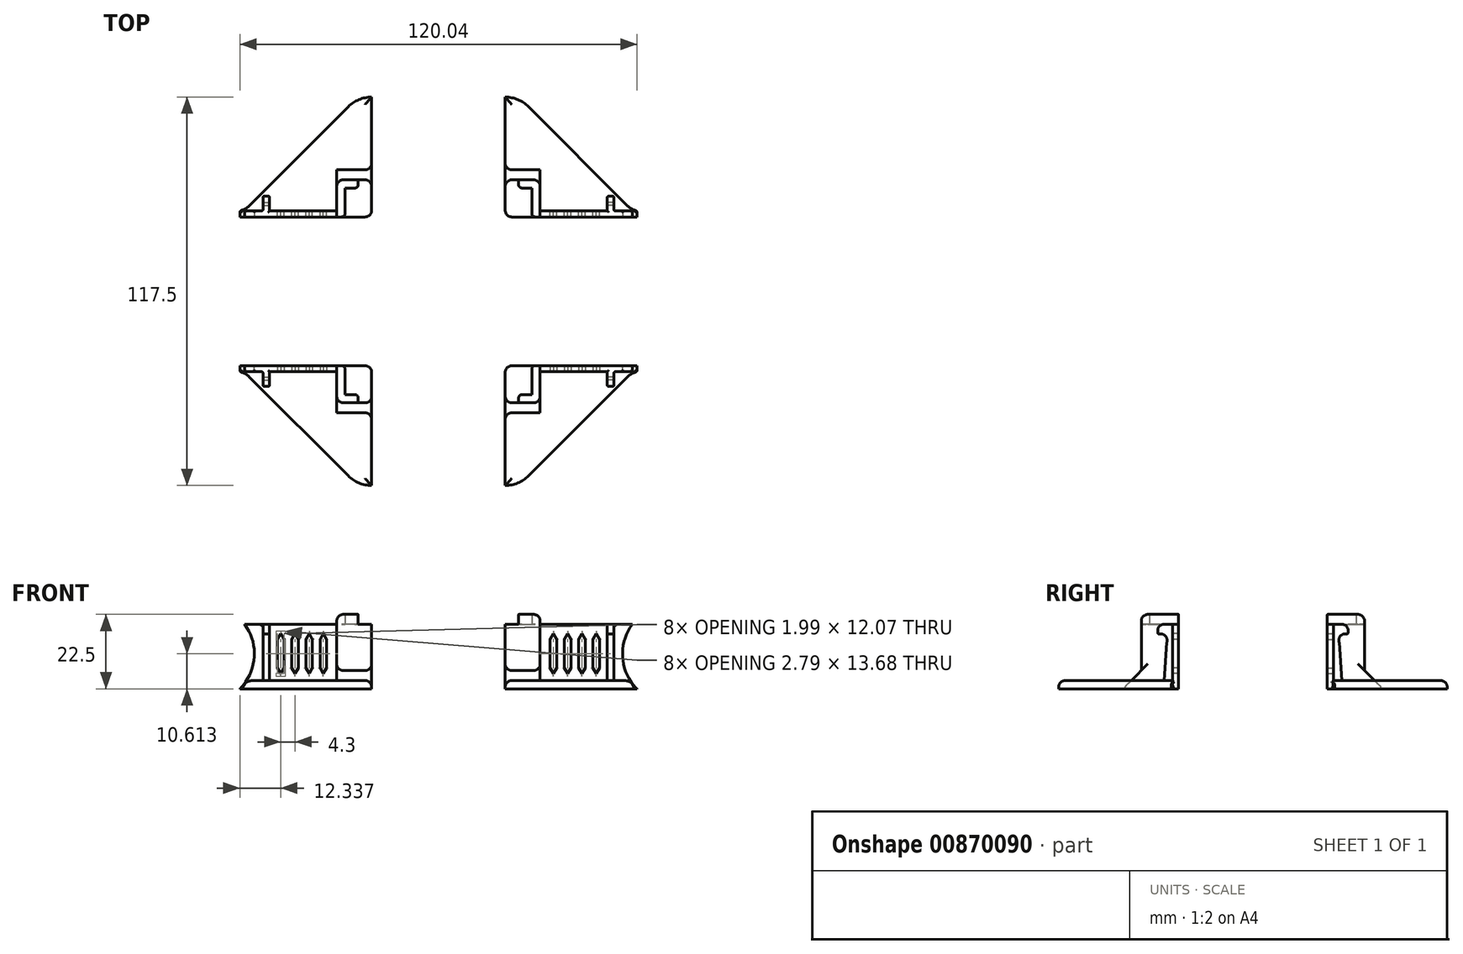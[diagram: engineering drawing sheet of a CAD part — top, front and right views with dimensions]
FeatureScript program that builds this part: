
annotation { "Feature Type Name" : "Feature", "Feature Type Description" : "" }
export const myFeature = defineFeature(function(context is Context, id is Id, definition is map)
    precondition{}
    {
        {
            var Q0;
            Q0=qCreatedBy(makeId("Top.planeOp"),FACE);
            var sketch = newSketch(context, id + "F0", { "sketchPlane" : qUnion([Q0])});
            skCircle(sketch, "E0.cCircle", {"center": v(0, 0) * mm, "radius": 58.75 * mm, "construction": true});
            skLineSegment(sketch, "E0.0", {"start": v(58.75, 24.34) * mm, "end": v(58.75, -24.34) * mm});
            skLineSegment(sketch, "E0.1", {"start": v(57.29, -25.8) * mm, "end": v(27.26, -55.82) * mm});
            skLineSegment(sketch, "E0.2", {"start": v(20.2, -58.75) * mm, "end": v(-20.2, -58.75) * mm});
            skLineSegment(sketch, "E0.3", {"start": v(-27.26, -55.82) * mm, "end": v(-57.29, -25.8) * mm});
            skLineSegment(sketch, "E0.4", {"start": v(-58.75, -24.34) * mm, "end": v(-58.75, 24.34) * mm});
            skLineSegment(sketch, "E0.5", {"start": v(-57.29, 25.8) * mm, "end": v(-27.26, 55.82) * mm});
            skLineSegment(sketch, "E0.6", {"start": v(-20.2, 58.75) * mm, "end": v(20.2, 58.75) * mm});
            skLineSegment(sketch, "E0.7", {"start": v(27.26, 55.82) * mm, "end": v(57.29, 25.8) * mm});
            skPoint(sketch, "E0.0.midPoint", {"position": v(58.75, 0) * mm});
            skLineSegment(sketch, "E1.bottom", {"start": v(60.82, 24.34) * mm, "end": v(85.75, 24.34) * mm});
            skLineSegment(sketch, "E1.top", {"start": v(60.82, -24.34) * mm, "end": v(85.75, -24.34) * mm});
            skLineSegment(sketch, "E1.right", {"start": v(90.75, 19.34) * mm, "end": v(90.75, -19.34) * mm});
            skLineSegment(sketch, "E2.bottom", {"start": v(-60.82, 24.34) * mm, "end": v(-85.75, 24.34) * mm});
            skLineSegment(sketch, "E2.top", {"start": v(-60.82, -24.34) * mm, "end": v(-85.75, -24.34) * mm});
            skLineSegment(sketch, "E2.left", {"start": v(-58.75, 24.34) * mm, "end": v(-58.75, -24.34) * mm});
            skLineSegment(sketch, "E2.right", {"start": v(-90.75, 19.34) * mm, "end": v(-90.75, -19.34) * mm});
            skPoint(sketch, "E3.visualSharp", {"position": v(-58.75, 24.34) * mm});
            skArc(sketch, "E3.filletArc", {"start": v(-60.82, 24.34) * mm, "mid": v(-58.9, 24.72) * mm, "end": v(-57.29, 25.8) * mm});
            skPoint(sketch, "E4.visualSharp", {"position": v(58.75, 24.34) * mm});
            skArc(sketch, "E4.filletArc", {"start": v(57.29, 25.8) * mm, "mid": v(58.9, 24.72) * mm, "end": v(60.82, 24.34) * mm});
            skPoint(sketch, "E5.visualSharp", {"position": v(24.34, 58.75) * mm});
            skArc(sketch, "E5.filletArc", {"start": v(27.26, 55.82) * mm, "mid": v(24.02, 57.99) * mm, "end": v(20.2, 58.75) * mm});
            skPoint(sketch, "E6.visualSharp", {"position": v(-24.34, 58.75) * mm});
            skArc(sketch, "E6.filletArc", {"start": v(-20.2, 58.75) * mm, "mid": v(-24.02, 57.99) * mm, "end": v(-27.26, 55.82) * mm});
            skPoint(sketch, "E7.visualSharp", {"position": v(24.34, -58.75) * mm});
            skArc(sketch, "E7.filletArc", {"start": v(20.2, -58.75) * mm, "mid": v(24.02, -57.99) * mm, "end": v(27.26, -55.82) * mm});
            skPoint(sketch, "E8.visualSharp", {"position": v(-24.34, -58.75) * mm});
            skArc(sketch, "E8.filletArc", {"start": v(-27.26, -55.82) * mm, "mid": v(-24.02, -57.99) * mm, "end": v(-20.2, -58.75) * mm});
            skPoint(sketch, "E9.visualSharp", {"position": v(-58.75, -24.34) * mm});
            skArc(sketch, "E9.filletArc", {"start": v(-57.29, -25.8) * mm, "mid": v(-58.9, -24.72) * mm, "end": v(-60.82, -24.34) * mm});
            skPoint(sketch, "E10.visualSharp", {"position": v(58.75, -24.34) * mm});
            skArc(sketch, "E10.filletArc", {"start": v(60.82, -24.34) * mm, "mid": v(58.9, -24.72) * mm, "end": v(57.29, -25.8) * mm});
            skPoint(sketch, "E11.visualSharp", {"position": v(90.75, -24.34) * mm});
            skArc(sketch, "E11.filletArc", {"start": v(85.75, -24.34) * mm, "mid": v(89.29, -22.87) * mm, "end": v(90.75, -19.34) * mm});
            skPoint(sketch, "E12.visualSharp", {"position": v(90.75, 24.34) * mm});
            skArc(sketch, "E12.filletArc", {"start": v(90.75, 19.34) * mm, "mid": v(89.29, 22.87) * mm, "end": v(85.75, 24.34) * mm});
            skPoint(sketch, "E13.visualSharp", {"position": v(-90.75, 24.34) * mm});
            skArc(sketch, "E13.filletArc", {"start": v(-85.75, 24.34) * mm, "mid": v(-89.29, 22.87) * mm, "end": v(-90.75, 19.34) * mm});
            skPoint(sketch, "E14.visualSharp", {"position": v(-90.75, -24.34) * mm});
            skArc(sketch, "E14.filletArc", {"start": v(-90.75, -19.34) * mm, "mid": v(-89.29, -22.87) * mm, "end": v(-85.75, -24.34) * mm});
            skLineSegment(sketch, "E15", {"start": v(-80.5, -24.34) * mm, "end": v(-80.5, -18.09) * mm});
            skLineSegment(sketch, "E16", {"start": v(-58.25, -18.09) * mm, "end": v(-84.25, -18.09) * mm});
            skLineSegment(sketch, "E17", {"start": v(-56.25, -16.09) * mm, "end": v(-56.25, -16.09) * mm});
            skLineSegment(sketch, "E18", {"start": v(-58.25, -14.09) * mm, "end": v(-84.25, -14.09) * mm});
            skLineSegment(sketch, "E19", {"start": v(-86.25, -16.09) * mm, "end": v(-86.25, -16.09) * mm});
            skLineSegment(sketch, "E20", {"start": v(-86.25, -14.09) * mm, "end": v(-90.75, -14.09) * mm});
            skLineSegment(sketch, "E21", {"start": v(-90.75, 0) * mm, "end": v(90.75, 0) * mm});
            skLineSegment(sketch, "E22", {"start": v(0, 58.75) * mm, "end": v(0, -58.75) * mm});
            skPoint(sketch, "E23.visualSharp", {"position": v(-86.25, -14.09) * mm});
            skArc(sketch, "E23.filletArc", {"start": v(-85.7, -14.09) * mm, "mid": v(-86.09, -14.25) * mm, "end": v(-86.25, -14.63) * mm});
            skArc(sketch, "E24.filletArc", {"start": v(-84.25, -14.09) * mm, "mid": v(-85.66, -14.67) * mm, "end": v(-86.25, -16.09) * mm});
            skPoint(sketch, "E25.visualSharp", {"position": v(-86.25, -18.09) * mm});
            skArc(sketch, "E25.filletArc", {"start": v(-86.25, -16.09) * mm, "mid": v(-85.66, -17.5) * mm, "end": v(-84.25, -18.09) * mm});
            skPoint(sketch, "E26.visualSharp", {"position": v(-56.25, -18.09) * mm});
            skArc(sketch, "E26.filletArc", {"start": v(-58.25, -18.09) * mm, "mid": v(-56.84, -17.5) * mm, "end": v(-56.25, -16.09) * mm});
            skPoint(sketch, "E27.visualSharp", {"position": v(-56.25, -14.09) * mm});
            skArc(sketch, "E27.filletArc", {"start": v(-56.25, -16.09) * mm, "mid": v(-56.84, -14.67) * mm, "end": v(-58.25, -14.09) * mm});
            skLineSegment(sketch, "E28.MirrorCS", {"start": v(-58.25, 14.09) * mm, "end": v(-84.25, 14.09) * mm});
            skArc(sketch, "E29.MirrorCS", {"start": v(-56.25, 16.09) * mm, "mid": v(-56.84, 14.67) * mm, "end": v(-58.25, 14.09) * mm});
            skArc(sketch, "E30.MirrorCS", {"start": v(-58.25, 18.09) * mm, "mid": v(-56.84, 17.5) * mm, "end": v(-56.25, 16.09) * mm});
            skLineSegment(sketch, "E31.MirrorCS", {"start": v(-58.25, 18.09) * mm, "end": v(-84.25, 18.09) * mm});
            skArc(sketch, "E32.MirrorCS", {"start": v(-86.25, 16.09) * mm, "mid": v(-85.66, 17.5) * mm, "end": v(-84.25, 18.09) * mm});
            skArc(sketch, "E33.MirrorCS", {"start": v(-84.25, 14.09) * mm, "mid": v(-85.66, 14.67) * mm, "end": v(-86.25, 16.09) * mm});
            skArc(sketch, "E34.MirrorCS", {"start": v(58.25, -18.09) * mm, "mid": v(56.84, -17.5) * mm, "end": v(56.25, -16.09) * mm});
            skArc(sketch, "E35.MirrorCS", {"start": v(56.25, -16.09) * mm, "mid": v(56.84, -14.67) * mm, "end": v(58.25, -14.09) * mm});
            skLineSegment(sketch, "E36.MirrorCS", {"start": v(58.25, -14.09) * mm, "end": v(84.25, -14.09) * mm});
            skArc(sketch, "E37.MirrorCS", {"start": v(84.25, -14.09) * mm, "mid": v(85.66, -14.67) * mm, "end": v(86.25, -16.09) * mm});
            skArc(sketch, "E38.MirrorCS", {"start": v(86.25, -16.09) * mm, "mid": v(85.66, -17.5) * mm, "end": v(84.25, -18.09) * mm});
            skLineSegment(sketch, "E39.MirrorCS", {"start": v(58.25, -18.09) * mm, "end": v(84.25, -18.09) * mm});
            skArc(sketch, "E40.MirrorCS", {"start": v(56.25, 16.09) * mm, "mid": v(56.84, 14.67) * mm, "end": v(58.25, 14.09) * mm});
            skArc(sketch, "E41.MirrorCS", {"start": v(58.25, 18.09) * mm, "mid": v(56.84, 17.5) * mm, "end": v(56.25, 16.09) * mm});
            skLineSegment(sketch, "E42.MirrorCS", {"start": v(58.25, 18.09) * mm, "end": v(84.25, 18.09) * mm});
            skArc(sketch, "E43.MirrorCS", {"start": v(86.25, 16.09) * mm, "mid": v(85.66, 17.5) * mm, "end": v(84.25, 18.09) * mm});
            skArc(sketch, "E44.MirrorCS", {"start": v(84.25, 14.09) * mm, "mid": v(85.66, 14.67) * mm, "end": v(86.25, 16.09) * mm});
            skLineSegment(sketch, "E45.MirrorCS", {"start": v(58.25, 14.09) * mm, "end": v(84.25, 14.09) * mm});
            skLineSegment(sketch, "E46.bottom", {"start": v(-41.75, -16) * mm, "end": v(-49.75, -16) * mm});
            skLineSegment(sketch, "E46.top", {"start": v(-41.75, 16) * mm, "end": v(-49.75, 16) * mm});
            skLineSegment(sketch, "E46.left", {"start": v(-39.75, -14) * mm, "end": v(-39.75, 14) * mm});
            skLineSegment(sketch, "E46.right", {"start": v(-51.75, -14) * mm, "end": v(-51.75, 14) * mm});
            skPoint(sketch, "E46.middle", {"position": v(-45.75, 0) * mm});
            skLineSegment(sketch, "E47", {"start": v(-51.75, 0) * mm, "end": v(-90.75, 0) * mm});
            skPoint(sketch, "E48.visualSharp", {"position": v(-51.75, 16) * mm});
            skArc(sketch, "E48.filletArc", {"start": v(-49.75, 16) * mm, "mid": v(-51.16, 15.41) * mm, "end": v(-51.75, 14) * mm});
            skPoint(sketch, "E49.visualSharp", {"position": v(-39.75, 16) * mm});
            skArc(sketch, "E49.filletArc", {"start": v(-39.75, 14) * mm, "mid": v(-40.34, 15.41) * mm, "end": v(-41.75, 16) * mm});
            skPoint(sketch, "E50.visualSharp", {"position": v(-39.75, -16) * mm});
            skArc(sketch, "E50.filletArc", {"start": v(-41.75, -16) * mm, "mid": v(-40.34, -15.41) * mm, "end": v(-39.75, -14) * mm});
            skPoint(sketch, "E51.visualSharp", {"position": v(-51.75, -16) * mm});
            skArc(sketch, "E51.filletArc", {"start": v(-51.75, -14) * mm, "mid": v(-51.16, -15.41) * mm, "end": v(-49.75, -16) * mm});
            skLineSegment(sketch, "E52.MirrorCS", {"start": v(39.75, -14) * mm, "end": v(39.75, 14) * mm});
            skArc(sketch, "E53.MirrorCS", {"start": v(39.75, 14) * mm, "mid": v(40.34, 15.41) * mm, "end": v(41.75, 16) * mm});
            skLineSegment(sketch, "E54.MirrorCS", {"start": v(41.75, 16) * mm, "end": v(49.75, 16) * mm});
            skArc(sketch, "E55.MirrorCS", {"start": v(49.75, 16) * mm, "mid": v(51.16, 15.41) * mm, "end": v(51.75, 14) * mm});
            skLineSegment(sketch, "E56.MirrorCS", {"start": v(51.75, -14) * mm, "end": v(51.75, 14) * mm});
            skArc(sketch, "E57.MirrorCS", {"start": v(51.75, -14) * mm, "mid": v(51.16, -15.41) * mm, "end": v(49.75, -16) * mm});
            skLineSegment(sketch, "E58.MirrorCS", {"start": v(41.75, -16) * mm, "end": v(49.75, -16) * mm});
            skArc(sketch, "E59.MirrorCS", {"start": v(41.75, -16) * mm, "mid": v(40.34, -15.41) * mm, "end": v(39.75, -14) * mm});
            skCircle(sketch, "E60", {"center": v(0, 0) * mm, "radius": 7.5 * mm});
            skLineSegment(sketch, "E61.bottom", {"start": v(68.5, -22.5) * mm, "end": v(-68.5, -22.5) * mm});
            skLineSegment(sketch, "E61.top", {"start": v(68.5, 22.5) * mm, "end": v(-68.5, 22.5) * mm});
            skLineSegment(sketch, "E61.left", {"start": v(68.5, -22.5) * mm, "end": v(68.5, 22.5) * mm});
            skLineSegment(sketch, "E61.right", {"start": v(-68.5, -22.5) * mm, "end": v(-68.5, 22.5) * mm});
            skLineSegment(sketch, "E62", {"start": v(-20.2, 58.75) * mm, "end": v(-20.2, -58.75) * mm});
            skLineSegment(sketch, "E63", {"start": v(20.2, 58.75) * mm, "end": v(20.2, -58.75) * mm});
            skLineSegment(sketch, "E64", {"start": v(-60.82, 24.34) * mm, "end": v(-20.2, 24.34) * mm});
            skLineSegment(sketch, "E65", {"start": v(-68.5, 22.5) * mm, "end": v(-71, 22.5) * mm});
            skLineSegment(sketch, "E66", {"start": v(-71, 22.5) * mm, "end": v(-71, 0) * mm});
            skLineSegment(sketch, "E67", {"start": v(-71, 22.34) * mm, "end": v(-71, 22.5) * mm});
            skLineSegment(sketch, "E68", {"start": v(-69, 24.34) * mm, "end": v(-60.82, 24.34) * mm});
            skPoint(sketch, "E69.visualSharp", {"position": v(-71, 24.34) * mm});
            skArc(sketch, "E69.filletArc", {"start": v(-69, 24.34) * mm, "mid": v(-70.41, 23.75) * mm, "end": v(-71, 22.34) * mm});
            skLineSegment(sketch, "E70.bottom", {"start": v(28.25, -31.25) * mm, "end": v(-28.25, -31.25) * mm});
            skLineSegment(sketch, "E70.top", {"start": v(28.25, 31.25) * mm, "end": v(-28.25, 31.25) * mm});
            skLineSegment(sketch, "E70.left", {"start": v(28.25, -31.25) * mm, "end": v(28.25, 31.25) * mm});
            skLineSegment(sketch, "E70.right", {"start": v(-28.25, -31.25) * mm, "end": v(-28.25, 31.25) * mm});
            skLineSegment(sketch, "E71", {"start": v(-28.25, 31.25) * mm, "end": v(-30.75, 31.25) * mm});
            skLineSegment(sketch, "E72", {"start": v(-28.25, 31.25) * mm, "end": v(-28.25, 33.75) * mm});
            skLineSegment(sketch, "E73", {"start": v(-30.75, 33.75) * mm, "end": v(-30.75, 24.34) * mm});
            skLineSegment(sketch, "E74", {"start": v(-30.75, 33.75) * mm, "end": v(0, 33.75) * mm});
            skLineSegment(sketch, "E75", {"start": v(-28.25, 34.5) * mm, "end": v(-24.25, 34.5) * mm});
            skLineSegment(sketch, "E76", {"start": v(-24.25, 33.75) * mm, "end": v(-24.25, 31.25) * mm});
            skLineSegment(sketch, "E77", {"start": v(-30.75, 24.34) * mm, "end": v(-30.75, 22.5) * mm});
            skLineSegment(sketch, "E78", {"start": v(-60.82, 24.34) * mm, "end": v(-60.82, 22.5) * mm});
            skSolve(sketch);
        }
        {
            var Q0;
            Q0=qCreatedBy(makeId("Top.planeOp"),FACE);
            var sketch = newSketch(context, id + "F1", { "sketchPlane" : qUnion([Q0])});
            skLineSegment(sketch, "E79.bottom", {"start": v(68.5, 22.5) * mm, "end": v(-68.5, 22.5) * mm});
            skLineSegment(sketch, "E79.top", {"start": v(68.5, -22.5) * mm, "end": v(-68.5, -22.5) * mm});
            skLineSegment(sketch, "E79.left", {"start": v(68.5, 22.5) * mm, "end": v(68.5, -22.5) * mm});
            skLineSegment(sketch, "E79.right", {"start": v(-68.5, 22.5) * mm, "end": v(-68.5, -22.5) * mm});
            skPoint(sketch, "E79.middle", {"position": v(0, 0) * mm});
            skSolve(sketch);
        }
        {
            var Q0;
            Q0=makeQuery(id+"F0.imprint","IMPRINT",FACE,{"disambiguationData":[TD([[makeQuery(id+"F0.imprint","IMPRINT",EDGE,{"derivedFrom":sQuery(id+"F0.wireOp",EDGE,"E0.5")}),-1.0]])]});
            extrude(context, id + "F2", {"entities" : qUnion([Q0]), "depth" : 2.5 * mm, "offsetDistance" : 25 * mm});
        }
        {
            var Q0;
            {var subQ5=sQuery(id+"F0.wireOp",EDGE,"E77");Q0=makeQuery(id+"F0.imprint","IMPRINT",FACE,{"disambiguationData":[TD([[makeQuery(id+"F0.imprint","IMPRINT",EDGE,{"derivedFrom":subQ5}),-1.0]])]});}
            var Q1;
            {var subQ4=sQuery(id+"F0.wireOp",EDGE,"E62");var subQ6=sQuery(id+"F0.wireOp",EDGE,"E64");var subQ8=makeQuery(id+"F0.imprint","INTERSECT",VERTEX,{"derivedFrom":[subQ4,subQ6]});Q1=makeQuery(id+"F0.imprint","IMPRINT",FACE,{"disambiguationData":[TD([[makeQuery(id+"F0.imprint","IMPRINT",EDGE,{"disambiguationData":[TD([[subQ8,1.0]])],"derivedFrom":subQ4}),-1.0]])]});}
            var Q2;
            {var subQ0=sQuery(id+"F0.wireOp",EDGE,"E62");var subQ1=sQuery(id+"F0.wireOp",EDGE,"E61.top");var subQ2=makeQuery(id+"F0.imprint","INTERSECT",VERTEX,{"derivedFrom":[subQ1,subQ0]});Q2=makeQuery(id+"F0.imprint","IMPRINT",FACE,{"disambiguationData":[TD([[makeQuery(id+"F0.imprint","IMPRINT",EDGE,{"disambiguationData":[TD([[subQ2,-1.0]])],"derivedFrom":subQ1}),-1.0]])]});}
            var Q3;
            {var subQ5=sQuery(id+"F0.wireOp",EDGE,"E76");Q3=makeQuery(id+"F0.imprint","IMPRINT",FACE,{"disambiguationData":[TD([[makeQuery(id+"F0.imprint","IMPRINT",EDGE,{"derivedFrom":subQ5}),1.0]])]});}
            var Q4;
            {var subQ5=sQuery(id+"F0.wireOp",EDGE,"E78");Q4=makeQuery(id+"F0.imprint","IMPRINT",FACE,{"disambiguationData":[TD([[makeQuery(id+"F0.imprint","IMPRINT",EDGE,{"derivedFrom":subQ5}),1.0]])]});}
            extrude(context, id + "F3", {"entities" : qUnion([Q0, Q1, Q2, Q3, Q4]), "operationType" : NewBodyOperationType.ADD, "depth" : 19.5 * mm, "offsetDistance" : 25 * mm});
        }
        {
            var Q0;
            {var subQ0=sQuery(id+"F0.wireOp",EDGE,"E72");Q0=makeQuery(id+"F0.imprint","IMPRINT",FACE,{"disambiguationData":[TD([[makeQuery(id+"F0.imprint","IMPRINT",EDGE,{"derivedFrom":subQ0}),-1.0]])]});}
            var Q1;
            {var subQ0=sQuery(id+"F0.wireOp",EDGE,"E71");Q1=makeQuery(id+"F0.imprint","IMPRINT",FACE,{"disambiguationData":[TD([[makeQuery(id+"F0.imprint","IMPRINT",EDGE,{"derivedFrom":subQ0}),-1.0]])]});}
            var Q2;
            {var subQ5=sQuery(id+"F0.wireOp",EDGE,"E71");Q2=makeQuery(id+"F0.imprint","IMPRINT",FACE,{"disambiguationData":[TD([[makeQuery(id+"F0.imprint","IMPRINT",EDGE,{"derivedFrom":subQ5}),1.0]])]});}
            var Q3;
            {var subQ0=sQuery(id+"F0.wireOp",EDGE,"E77");Q3=makeQuery(id+"F0.imprint","IMPRINT",FACE,{"disambiguationData":[TD([[makeQuery(id+"F0.imprint","IMPRINT",EDGE,{"derivedFrom":subQ0}),1.0]])]});}
            extrude(context, id + "F4", {"entities" : qUnion([Q0, Q1, Q2, Q3]), "operationType" : NewBodyOperationType.ADD, "depth" : 22.5 * mm, "offsetDistance" : 25 * mm});
        }
        {
            var Q0;
            Q0=makeQuery(id+"F4.opExtrude","SWEPT_FACE",FACE,{"disambiguationData":[OSD([sQuery(id+"F0.wireOp",EDGE,"E73"),sQuery(id+"F0.wireOp",EDGE,"E77")])]});
            var sketch = newSketch(context, id + "F5", { "sketchPlane" : qUnion([Q0])});
            skLineSegment(sketch, "E80", {"start": v(-24.34, 19.5) * mm, "end": v(-24.34, 0) * mm});
            skLineSegment(sketch, "E81", {"start": v(-24.34, 0) * mm, "end": v(-24.34, 0) * mm});
            skLineSegment(sketch, "E82", {"start": v(-28.78, 16.41) * mm, "end": v(-28.78, 19.5) * mm});
            skLineSegment(sketch, "E83", {"start": v(-28.78, 19.5) * mm, "end": v(-24.34, 19.5) * mm});
            skCircle(sketch, "E84", {"center": v(-27.9, 14.67) * mm, "radius": 1.95 * mm});
            skCircle(sketch, "E85", {"center": v(-26.92, 17.64) * mm, "radius": 1.86 * mm});
            skLineSegment(sketch, "E86", {"start": v(-26.06, 14.04) * mm, "end": v(-27.04, 0) * mm});
            skLineSegment(sketch, "E87", {"start": v(-27.04, 0) * mm, "end": v(-24.34, 0) * mm});
            skSolve(sketch);
        }
        {
            var Q0;
            {var subQ0=sQuery(id+"F5.wireOp",EDGE,"euI4lTT9-Io7a-ZlEk-LRN0-sRpwTMsxyult");var subQ1=sQuery(id+"F5.wireOp",EDGE,"E84");var subQ2=makeQuery(id+"F5.imprint","INTERSECT",VERTEX,{"derivedFrom":[subQ1,subQ0]});Q0=makeQuery(id+"F5.imprint","IMPRINT",FACE,{"disambiguationData":[TD([[makeQuery(id+"F5.imprint","IMPRINT",EDGE,{"disambiguationData":[TD([[subQ2,-1.0]])],"derivedFrom":subQ1}),-1.0]])]});}
            var Q1;
            {var subQ0=sQuery(id+"F5.wireOp",EDGE,"E85");var subQ1=sQuery(id+"F5.wireOp",EDGE,"E84");var subQ2=makeQuery(id+"F5.imprint","INTERSECT",VERTEX,{"disambiguationData":[OD(0.0)],"derivedFrom":[subQ1,subQ0]});Q1=makeQuery(id+"F5.imprint","IMPRINT",FACE,{"disambiguationData":[TD([[makeQuery(id+"F5.imprint","IMPRINT",EDGE,{"disambiguationData":[TD([[subQ2,1.0]])],"derivedFrom":subQ1}),-1.0]])]});}
            var Q2;
            {var subQ0=sQuery(id+"F5.wireOp",EDGE,"E85");var subQ1=sQuery(id+"F5.wireOp",EDGE,"E84");var subQ2=makeQuery(id+"F5.imprint","INTERSECT",VERTEX,{"disambiguationData":[OD(0.0)],"derivedFrom":[subQ1,subQ0]});Q2=makeQuery(id+"F5.imprint","IMPRINT",FACE,{"disambiguationData":[TD([[makeQuery(id+"F5.imprint","IMPRINT",EDGE,{"disambiguationData":[TD([[subQ2,-1.0]])],"derivedFrom":subQ1}),-1.0]])]});}
            var Q3;
            {var subQ3=sQuery(id+"F5.wireOp",EDGE,"E84");var subQ5=sQuery(id+"F5.wireOp",EDGE,"E86");var subQ6=makeQuery(id+"F5.imprint","INTERSECT",VERTEX,{"derivedFrom":[subQ3,subQ5]});Q3=makeQuery(id+"F5.imprint","IMPRINT",FACE,{"disambiguationData":[TD([[makeQuery(id+"F5.imprint","IMPRINT",EDGE,{"disambiguationData":[TD([[subQ6,-1.0]])],"derivedFrom":subQ3}),-1.0]])]});}
            extrude(context, id + "F6", {"entities" : qUnion([Q0, Q1, Q2, Q3]), "operationType" : NewBodyOperationType.ADD, "depth" : 22.3 * mm, "offsetDistance" : 25 * mm, "hasSecondDirection" : true, "secondDirectionOppositeDirection" : false, "secondDirectionDepth" : 20.3 * mm});
        }
        {
            var Q0;
            Q0=makeQuery(id+"F6.opExtrude","CAP_EDGE",EDGE,{"disambiguationData":[OSD([sQuery(id+"F5.wireOp",EDGE,"E85")])],"isStart":false});
            var Q1;
            Q1=makeQuery(id+"F6.opExtrude","CAP_EDGE",EDGE,{"disambiguationData":[OSD([sQuery(id+"F5.wireOp",EDGE,"E80")])],"isStart":false});
            var Q2;
            Q2=makeQuery(id+"F6.opExtrude","CAP_EDGE",EDGE,{"disambiguationData":[OSD([sQuery(id+"F5.wireOp",EDGE,"E86")])],"isStart":false});
            var Q3;
            Q3=makeQuery(id+"F6.opExtrude","CAP_EDGE",EDGE,{"disambiguationData":[OSD([sQuery(id+"F5.wireOp",EDGE,"E84")])],"isStart":false});
            var Q4;
            Q4=makeQuery(id+"F6.opExtrude","CAP_EDGE",EDGE,{"disambiguationData":[OSD([sQuery(id+"F5.wireOp",EDGE,"E84")])],"isStart":true});
            var Q5;
            Q5=makeQuery(id+"F6.opExtrude","CAP_EDGE",EDGE,{"disambiguationData":[OSD([sQuery(id+"F5.wireOp",EDGE,"E86")])],"isStart":true});
            var Q6;
            Q6=makeQuery(id+"F6.opExtrude","SWEPT_EDGE",EDGE,{"disambiguationData":[OSD([sQuery(id+"F0.wireOp",EDGE,"E73"),sQuery(id+"F5.wireOp",EDGE,"E86")])]});
            var Q7;
            Q7=makeQuery(id+"F6.opExtrude","SWEPT_EDGE",EDGE,{"disambiguationData":[OSD([sQuery(id+"F5.wireOp",EDGE,"E84"),sQuery(id+"F5.wireOp",EDGE,"E86")])]});
            var Q8;
            Q8=makeQuery(id+"F6.opExtrude","SWEPT_EDGE",EDGE,{"disambiguationData":[OSD([sQuery(id+"F5.wireOp",EDGE,"E82"),sQuery(id+"F5.wireOp",EDGE,"E84")])]});
            var Q9;
            Q9=makeQuery(id+"F6.opExtrude","CAP_EDGE",EDGE,{"disambiguationData":[OSD([sQuery(id+"F5.wireOp",EDGE,"E83")])],"isStart":true});
            var Q10;
            {var subQ1=sQuery(id+"F0.wireOp",EDGE,"E73");var subQ2=sQuery(id+"F0.wireOp",EDGE,"E77");var subQ3=sQuery(id+"F0.wireOp",EDGE,"E64");Q10=makeQuery(id+"F6.boolean.opBoolean","SPLIT",EDGE,{"disambiguationData":[TD([makeQuery(id+"F4.opExtrude","SWEPT_FACE",FACE,{"disambiguationData":[OSD([subQ1,subQ2])]})])],"derivedFrom":makeQuery(id+"F3.opExtrude","CAP_EDGE",EDGE,{"disambiguationData":[OSD([subQ3])],"isStart":false})});}
            fillet(context, id + "F7", {"entities" : qUnion([Q0, Q1, Q2, Q3, Q4, Q5, Q6, Q7, Q8, Q9, Q10]), "radius" : .4 * mm, "tangentPropagation" : true, "allowEdgeOverflow" : false});
        }
        {
            var Q0;
            {var subQ0=sQuery(id+"F0.wireOp",EDGE,"E74");var subQ2=makeQuery(id+"F2.opExtrude","CAP_EDGE",EDGE,{"disambiguationData":[OSD([subQ0])],"isStart":false});Q0=makeQuery(id+"F4.boolean.opBoolean","MERGE",EDGE,{"derivedFrom":[makeQuery(id+"F3.boolean.opBoolean","SPLIT",EDGE,{"disambiguationData":[topologyDisambiguationEdgeConnected([makeQuery(id+"F2.opExtrude","SWEPT_FACE",FACE,{"disambiguationData":[OSD([subQ0])]})])],"derivedFrom":subQ2}),makeQuery(id+"F3.boolean.opBoolean","SPLIT",EDGE,{"disambiguationData":[topologyDisambiguationEdgeConnected([makeQuery(id+"F3.opExtrude","SWEPT_FACE",FACE,{"disambiguationData":[OSD([subQ0])]})])],"derivedFrom":subQ2})]});}
            var Q1;
            Q1=makeQuery(id+"F2.opExtrude","CAP_EDGE",EDGE,{"disambiguationData":[OSD([sQuery(id+"F0.wireOp",EDGE,"E73")])],"isStart":false});
            var Q2;
            Q2=makeQuery(id+"FH1p5v7uj7fFukZ_1.opPattern","COPY",EDGE,{"derivedFrom":makeQuery(id+"F2.opExtrude","CAP_EDGE",EDGE,{"disambiguationData":[OSD([sQuery(id+"F0.wireOp",EDGE,"E73")])],"isStart":false}),"instanceName":"1"});
            var Q3;
            {var subQ0=sQuery(id+"F0.wireOp",EDGE,"E74");var subQ2=makeQuery(id+"F2.opExtrude","CAP_EDGE",EDGE,{"disambiguationData":[OSD([subQ0])],"isStart":false});Q3=makeQuery(id+"FH1p5v7uj7fFukZ_1.opPattern","COPY",EDGE,{"derivedFrom":makeQuery(id+"F4.boolean.opBoolean","MERGE",EDGE,{"derivedFrom":[makeQuery(id+"F3.boolean.opBoolean","SPLIT",EDGE,{"disambiguationData":[topologyDisambiguationEdgeConnected([makeQuery(id+"F2.opExtrude","SWEPT_FACE",FACE,{"disambiguationData":[OSD([subQ0])]})])],"derivedFrom":subQ2}),makeQuery(id+"F3.boolean.opBoolean","SPLIT",EDGE,{"disambiguationData":[topologyDisambiguationEdgeConnected([makeQuery(id+"F3.opExtrude","SWEPT_FACE",FACE,{"disambiguationData":[OSD([subQ0])]})])],"derivedFrom":subQ2})]}),"instanceName":"1"});}
            chamfer(context, id + "F8", {"entities" : qUnion([Q0, Q1, Q2, Q3]), "width" : 3 * mm, "tangentPropagation" : true});
        }
        {
            var Q0;
            Q0=makeQuery(id+"F4.opExtrude","SWEPT_EDGE",EDGE,{"disambiguationData":[OSD([sQuery(id+"F0.wireOp",EDGE,"E73"),sQuery(id+"F0.wireOp",EDGE,"E74")])]});
            var Q1;
            Q1=makeQuery(id+"F4.opExtrude","CAP_EDGE",EDGE,{"disambiguationData":[OSD([sQuery(id+"F0.wireOp",EDGE,"E73"),sQuery(id+"F0.wireOp",EDGE,"E77")])],"isStart":false});
            var Q2;
            Q2=makeQuery(id+"F4.opExtrude","CAP_EDGE",EDGE,{"disambiguationData":[OSD([sQuery(id+"F0.wireOp",EDGE,"E74")])],"isStart":false});
            var Q3;
            Q3=makeQuery(id+"F3.opExtrude","SWEPT_EDGE",EDGE,{"disambiguationData":[OSD([sQuery(id+"F0.wireOp",EDGE,"E62"),sQuery(id+"F0.wireOp",EDGE,"E74")])]});
            var Q4;
            Q4=makeQuery(id+"F3.opExtrude","SWEPT_EDGE",EDGE,{"disambiguationData":[OSD([sQuery(id+"F0.wireOp",EDGE,"E61.top"),sQuery(id+"F0.wireOp",EDGE,"E62")])]});
            var Q5;
            Q5=makeQuery(id+"F2.opExtrude","CAP_EDGE",EDGE,{"disambiguationData":[OSD([sQuery(id+"F0.wireOp",EDGE,"E62")])],"isStart":false});
            var Q6;
            Q6=makeQuery(id+"F2.opExtrude","CAP_EDGE",EDGE,{"disambiguationData":[OSD([sQuery(id+"F0.wireOp",EDGE,"E0.5")])],"isStart":false});
            fillet(context, id + "F9", {"entities" : qUnion([Q0, Q1, Q2, Q3, Q4, Q5, Q6]), "radius" : 2 * mm, "tangentPropagation" : true, "allowEdgeOverflow" : false});
        }
        {
            var Q0;
            Q0=makeQuery(id+"FH1p5v7uj7fFukZ_1.opPattern","COPY",EDGE,{"derivedFrom":makeQuery(id+"F3.opExtrude","CAP_EDGE",EDGE,{"disambiguationData":[OSD([sQuery(id+"F0.wireOp",EDGE,"E64"),sQuery(id+"F0.wireOp",EDGE,"E68")])],"isStart":false}),"instanceName":"1"});
            var Q1;
            Q1=makeQuery(id+"F3.opExtrude","CAP_EDGE",EDGE,{"disambiguationData":[OSD([sQuery(id+"F0.wireOp",EDGE,"E66")])],"isStart":false});
            var Q2;
            Q2=makeQuery(id+"FH1p5v7uj7fFukZ_1.opPattern","COPY",EDGE,{"derivedFrom":makeQuery(id+"F4.opExtrude","SWEPT_EDGE",EDGE,{"disambiguationData":[OSD([sQuery(id+"F0.wireOp",EDGE,"E61.top"),sQuery(id+"F0.wireOp",EDGE,"E70.right")])]}),"instanceName":"1"});
            var Q3;
            Q3=makeQuery(id+"F4.opExtrude","SWEPT_EDGE",EDGE,{"disambiguationData":[OSD([sQuery(id+"F0.wireOp",EDGE,"E61.top"),sQuery(id+"F0.wireOp",EDGE,"E70.right")])]});
            var Q4;
            Q4=makeQuery(id+"FH1p5v7uj7fFukZ_1.opPattern","COPY",EDGE,{"derivedFrom":makeQuery(id+"F4.opExtrude","SWEPT_EDGE",EDGE,{"disambiguationData":[OSD([sQuery(id+"F0.wireOp",EDGE,"E70.top"),sQuery(id+"F0.wireOp",EDGE,"E76")])]}),"instanceName":"1"});
            var Q5;
            Q5=makeQuery(id+"F4.opExtrude","SWEPT_EDGE",EDGE,{"disambiguationData":[OSD([sQuery(id+"F0.wireOp",EDGE,"E70.top"),sQuery(id+"F0.wireOp",EDGE,"E76")])]});
            fillet(context, id + "F10", {"entities" : qUnion([Q0, Q1, Q2, Q3, Q4, Q5]), "radius" : 1 * mm, "tangentPropagation" : true, "allowEdgeOverflow" : false});
        }
        {
            var Q0;
            {var subQ0=sQuery(id+"F0.wireOp",EDGE,"E61.top");Q0=makeQuery(id+"F4.boolean.opBoolean","MERGE",FACE,{"derivedFrom":[makeQuery(id+"F3.opExtrude","SWEPT_FACE",FACE,{"disambiguationData":[OSD([subQ0]),TDD([makeQuery(id+"F0.imprint","IMPRINT",EDGE,{"disambiguationData":[TD([[makeQuery(id+"F0.imprint","INTERSECT",VERTEX,{"derivedFrom":[subQ0,sQuery(id+"F0.wireOp",EDGE,"E77")]}),-1.0]])],"derivedFrom":subQ0}),makeQuery(id+"F0.imprint","IMPRINT",EDGE,{"disambiguationData":[TD([[makeQuery(id+"F0.imprint","INTERSECT",VERTEX,{"derivedFrom":[subQ0,sQuery(id+"F0.wireOp",EDGE,"E78")]}),1.0]])],"derivedFrom":subQ0})])]}),makeQuery(id+"F3.opExtrude","SWEPT_FACE",FACE,{"disambiguationData":[OSD([subQ0]),TDD([makeQuery(id+"F0.imprint","IMPRINT",EDGE,{"disambiguationData":[TD([[makeQuery(id+"F0.imprint","INTERSECT",VERTEX,{"derivedFrom":[subQ0,sQuery(id+"F0.wireOp",EDGE,"E62")]}),-1.0]])],"derivedFrom":subQ0})])]}),makeQuery(id+"F4.opExtrude","SWEPT_FACE",FACE,{"disambiguationData":[OSD([subQ0])]})]});}
            var sketch = newSketch(context, id + "F11", { "sketchPlane" : qUnion([Q0])});
            skCircle(sketch, "E88", {"center": v(-70.66, 10.57) * mm, "radius": 15 * mm});
            skPoint(sketch, "E88.centerSnap0", {"position": v(-70.66, 10.57) * mm});
            skSolve(sketch);
        }
        {
            var Q0;
            {var subQ1=sQuery(id+"F0.wireOp",EDGE,"E78");var subQ2=sQuery(id+"F0.wireOp",EDGE,"E61.top");var subQ10=makeQuery(id+"F3.opExtrude","SWEPT_EDGE",EDGE,{"disambiguationData":[OSD([subQ2,subQ1])]});Q0=makeQuery(id+"F11.imprint","IMPRINT",FACE,{"disambiguationData":[TD([[makeQuery(id+"F11.imprint","IMPRINT",EDGE,{"derivedFrom":subQ10}),1.0]])]});}
            extrude(context, id + "F12", {"entities" : qUnion([Q0]), "operationType" : NewBodyOperationType.REMOVE, "oppositeDirection" : true, "depth" : 2 * mm, "offsetDistance" : 25 * mm});
        }
        {
            var Q0;
            {var subQ1=sQuery(id+"F0.wireOp",EDGE,"E77");var subQ2=sQuery(id+"F0.wireOp",EDGE,"E64");var subQ4=sQuery(id+"F0.wireOp",EDGE,"E3.filletArc");var subQ5=sQuery(id+"F0.wireOp",EDGE,"E73");var subQ14=makeQuery(id+"F3.opExtrude","SWEPT_FACE",FACE,{"disambiguationData":[OSD([subQ2])]});Q0=qUnion([makeQuery(id+"F6.boolean.opBoolean","SPLIT",FACE,{"disambiguationData":[TD([makeQuery(id+"F4.opExtrude","SWEPT_FACE",FACE,{"disambiguationData":[OSD([subQ5,subQ1])]})])],"derivedFrom":subQ14}),makeQuery(id+"F6.boolean.opBoolean","SPLIT",FACE,{"disambiguationData":[TD([makeQuery(id+"F2.opExtrude","SWEPT_FACE",FACE,{"disambiguationData":[OSD([subQ4])]})])],"derivedFrom":subQ14})]);}
            var sketch = newSketch(context, id + "F13", { "sketchPlane" : qUnion([Q0])});
            skLineSegment(sketch, "E89", {"start": v(35.78, 14.91) * mm, "end": v(35.78, 6.31) * mm});
            skLineSegment(sketch, "E90", {"start": v(33.79, 14.91) * mm, "end": v(33.79, 6.31) * mm});
            skLineSegment(sketch, "E91", {"start": v(35.78, 14.91) * mm, "end": v(33.79, 14.91) * mm});
            skLineSegment(sketch, "E92", {"start": v(35.78, 14.91) * mm, "end": v(34.78, 16.65) * mm});
            skPoint(sketch, "E92.endSnap0", {"position": v(34.78, 14.91) * mm});
            skLineSegment(sketch, "E93", {"start": v(34.78, 16.65) * mm, "end": v(33.79, 14.91) * mm});
            skLineSegment(sketch, "E94", {"start": v(35.78, 6.31) * mm, "end": v(33.79, 6.31) * mm});
            skLineSegment(sketch, "E95", {"start": v(35.78, 6.31) * mm, "end": v(34.78, 6.31) * mm});
            skLineSegment(sketch, "E96", {"start": v(35.78, 6.31) * mm, "end": v(34.78, 4.58) * mm});
            skLineSegment(sketch, "E97", {"start": v(34.78, 4.58) * mm, "end": v(33.79, 6.31) * mm});
            skLineSegment(sketch, "E98.1.0.0", {"start": v(38.09, 14.91) * mm, "end": v(38.09, 6.31) * mm});
            skLineSegment(sketch, "E98.1.0.1", {"start": v(39.08, 4.58) * mm, "end": v(38.09, 6.31) * mm});
            skPoint(sketch, "E98.1.0.2", {"position": v(39.08, 14.91) * mm});
            skLineSegment(sketch, "E98.1.0.3", {"start": v(40.08, 14.91) * mm, "end": v(40.08, 6.31) * mm});
            skLineSegment(sketch, "E98.1.0.4", {"start": v(39.08, 16.65) * mm, "end": v(38.09, 14.91) * mm});
            skLineSegment(sketch, "E98.1.0.5", {"start": v(40.08, 6.31) * mm, "end": v(39.08, 4.58) * mm});
            skLineSegment(sketch, "E98.1.0.6", {"start": v(40.08, 14.91) * mm, "end": v(39.08, 16.65) * mm});
            skLineSegment(sketch, "E98.1.0.7", {"start": v(40.08, 6.31) * mm, "end": v(38.09, 6.31) * mm});
            skLineSegment(sketch, "E98.1.0.8", {"start": v(40.08, 6.31) * mm, "end": v(39.08, 6.31) * mm});
            skLineSegment(sketch, "E98.1.0.9", {"start": v(40.08, 14.91) * mm, "end": v(38.09, 14.91) * mm});
            skLineSegment(sketch, "E98.2.0.0", {"start": v(42.39, 14.91) * mm, "end": v(42.39, 6.31) * mm});
            skLineSegment(sketch, "E98.2.0.1", {"start": v(43.38, 4.58) * mm, "end": v(42.39, 6.31) * mm});
            skPoint(sketch, "E98.2.0.2", {"position": v(43.38, 14.91) * mm});
            skLineSegment(sketch, "E98.2.0.3", {"start": v(44.38, 14.91) * mm, "end": v(44.38, 6.31) * mm});
            skLineSegment(sketch, "E98.2.0.4", {"start": v(43.38, 16.65) * mm, "end": v(42.39, 14.91) * mm});
            skLineSegment(sketch, "E98.2.0.5", {"start": v(44.38, 6.31) * mm, "end": v(43.38, 4.58) * mm});
            skLineSegment(sketch, "E98.2.0.6", {"start": v(44.38, 14.91) * mm, "end": v(43.38, 16.65) * mm});
            skLineSegment(sketch, "E98.2.0.7", {"start": v(44.38, 6.31) * mm, "end": v(42.39, 6.31) * mm});
            skLineSegment(sketch, "E98.2.0.8", {"start": v(44.38, 6.31) * mm, "end": v(43.38, 6.31) * mm});
            skLineSegment(sketch, "E98.2.0.9", {"start": v(44.38, 14.91) * mm, "end": v(42.39, 14.91) * mm});
            skLineSegment(sketch, "E98.3.0.0", {"start": v(46.69, 14.91) * mm, "end": v(46.69, 6.31) * mm});
            skLineSegment(sketch, "E98.3.0.1", {"start": v(47.68, 4.58) * mm, "end": v(46.69, 6.31) * mm});
            skPoint(sketch, "E98.3.0.2", {"position": v(47.68, 14.91) * mm});
            skLineSegment(sketch, "E98.3.0.3", {"start": v(48.68, 14.91) * mm, "end": v(48.68, 6.31) * mm});
            skLineSegment(sketch, "E98.3.0.4", {"start": v(47.68, 16.65) * mm, "end": v(46.69, 14.91) * mm});
            skLineSegment(sketch, "E98.3.0.5", {"start": v(48.68, 6.31) * mm, "end": v(47.68, 4.58) * mm});
            skLineSegment(sketch, "E98.3.0.6", {"start": v(48.68, 14.91) * mm, "end": v(47.68, 16.65) * mm});
            skLineSegment(sketch, "E98.3.0.7", {"start": v(48.68, 6.31) * mm, "end": v(46.69, 6.31) * mm});
            skLineSegment(sketch, "E98.3.0.8", {"start": v(48.68, 6.31) * mm, "end": v(47.68, 6.31) * mm});
            skLineSegment(sketch, "E98.3.0.9", {"start": v(48.68, 14.91) * mm, "end": v(46.69, 14.91) * mm});
            skLineSegment(sketch, "E98.direction1", {"start": v(34.78, 4.58) * mm, "end": v(39.08, 4.58) * mm, "construction": true});
            skSolve(sketch);
        }
        {
            var Q0;
            Q0=makeQuery(id+"F13.imprint","IMPRINT",FACE,{"disambiguationData":[TD([[makeQuery(id+"F13.imprint","IMPRINT",EDGE,{"derivedFrom":sQuery(id+"F13.wireOp",EDGE,"E91")}),-1.0]])]});
            var Q1;
            {var subQ3=sQuery(id+"F13.wireOp",EDGE,"E89");Q1=makeQuery(id+"F13.imprint","IMPRINT",FACE,{"disambiguationData":[TD([[makeQuery(id+"F13.imprint","IMPRINT",EDGE,{"derivedFrom":subQ3}),-1.0]])]});}
            var Q2;
            {var subQ3=sQuery(id+"F13.wireOp",EDGE,"E96");Q2=makeQuery(id+"F13.imprint","IMPRINT",FACE,{"disambiguationData":[TD([[makeQuery(id+"F13.imprint","IMPRINT",EDGE,{"derivedFrom":subQ3}),-1.0]])]});}
            var Q3;
            Q3=makeQuery(id+"F13.imprint","IMPRINT",FACE,{"disambiguationData":[TD([[makeQuery(id+"F13.imprint","IMPRINT",EDGE,{"derivedFrom":sQuery(id+"F13.wireOp",EDGE,"d3e0095a-e30d-40a6-bb55-9c31538d2f1b.1.0.0")}),-1.0]])]});
            var Q4;
            Q4=makeQuery(id+"F13.imprint","IMPRINT",FACE,{"disambiguationData":[TD([[makeQuery(id+"F13.imprint","IMPRINT",EDGE,{"derivedFrom":sQuery(id+"F13.wireOp",EDGE,"d3e0095a-e30d-40a6-bb55-9c31538d2f1b.1.0.0")}),1.0]])]});
            var Q5;
            Q5=makeQuery(id+"F13.imprint","IMPRINT",FACE,{"disambiguationData":[TD([[makeQuery(id+"F13.imprint","IMPRINT",EDGE,{"derivedFrom":sQuery(id+"F13.wireOp",EDGE,"d3e0095a-e30d-40a6-bb55-9c31538d2f1b.1.0.1")}),-1.0]])]});
            var Q6;
            Q6=makeQuery(id+"F13.imprint","IMPRINT",FACE,{"disambiguationData":[TD([[makeQuery(id+"F13.imprint","IMPRINT",EDGE,{"derivedFrom":sQuery(id+"F13.wireOp",EDGE,"d3e0095a-e30d-40a6-bb55-9c31538d2f1b.2.0.1")}),-1.0]])]});
            var Q7;
            Q7=makeQuery(id+"F13.imprint","IMPRINT",FACE,{"disambiguationData":[TD([[makeQuery(id+"F13.imprint","IMPRINT",EDGE,{"derivedFrom":sQuery(id+"F13.wireOp",EDGE,"d3e0095a-e30d-40a6-bb55-9c31538d2f1b.2.0.0")}),1.0]])]});
            var Q8;
            Q8=makeQuery(id+"F13.imprint","IMPRINT",FACE,{"disambiguationData":[TD([[makeQuery(id+"F13.imprint","IMPRINT",EDGE,{"derivedFrom":sQuery(id+"F13.wireOp",EDGE,"d3e0095a-e30d-40a6-bb55-9c31538d2f1b.2.0.0")}),-1.0]])]});
            var Q9;
            Q9=makeQuery(id+"F13.imprint","IMPRINT",FACE,{"disambiguationData":[TD([[makeQuery(id+"F13.imprint","IMPRINT",EDGE,{"derivedFrom":sQuery(id+"F13.wireOp",EDGE,"d3e0095a-e30d-40a6-bb55-9c31538d2f1b.3.0.1")}),-1.0]])]});
            var Q10;
            Q10=makeQuery(id+"F13.imprint","IMPRINT",FACE,{"disambiguationData":[TD([[makeQuery(id+"F13.imprint","IMPRINT",EDGE,{"derivedFrom":sQuery(id+"F13.wireOp",EDGE,"d3e0095a-e30d-40a6-bb55-9c31538d2f1b.3.0.0")}),1.0]])]});
            var Q11;
            Q11=makeQuery(id+"F13.imprint","IMPRINT",FACE,{"disambiguationData":[TD([[makeQuery(id+"F13.imprint","IMPRINT",EDGE,{"derivedFrom":sQuery(id+"F13.wireOp",EDGE,"d3e0095a-e30d-40a6-bb55-9c31538d2f1b.3.0.0")}),-1.0]])]});
            var Q12;
            Q12=makeQuery(id+"F13.imprint","IMPRINT",FACE,{"disambiguationData":[TD([[makeQuery(id+"F13.imprint","IMPRINT",EDGE,{"derivedFrom":sQuery(id+"F13.wireOp",EDGE,"d3e0095a-e30d-40a6-bb55-9c31538d2f1b.4.0.1")}),-1.0]])]});
            var Q13;
            Q13=makeQuery(id+"F13.imprint","IMPRINT",FACE,{"disambiguationData":[TD([[makeQuery(id+"F13.imprint","IMPRINT",EDGE,{"derivedFrom":sQuery(id+"F13.wireOp",EDGE,"d3e0095a-e30d-40a6-bb55-9c31538d2f1b.4.0.0")}),1.0]])]});
            var Q14;
            Q14=makeQuery(id+"F13.imprint","IMPRINT",FACE,{"disambiguationData":[TD([[makeQuery(id+"F13.imprint","IMPRINT",EDGE,{"derivedFrom":sQuery(id+"F13.wireOp",EDGE,"d3e0095a-e30d-40a6-bb55-9c31538d2f1b.4.0.0")}),-1.0]])]});
            var Q15;
            Q15=makeQuery(id+"F13.imprint","IMPRINT",FACE,{"disambiguationData":[TD([[makeQuery(id+"F13.imprint","IMPRINT",EDGE,{"derivedFrom":sQuery(id+"F13.wireOp",EDGE,"54823be7-8fca-406a-8078-c69425b5e832.0.3.0")}),1.0]])]});
            var Q16;
            Q16=makeQuery(id+"F13.imprint","IMPRINT",FACE,{"disambiguationData":[TD([[makeQuery(id+"F13.imprint","IMPRINT",EDGE,{"derivedFrom":sQuery(id+"F13.wireOp",EDGE,"54823be7-8fca-406a-8078-c69425b5e832.0.3.0")}),-1.0]])]});
            var Q17;
            Q17=makeQuery(id+"F13.imprint","IMPRINT",FACE,{"disambiguationData":[TD([[makeQuery(id+"F13.imprint","IMPRINT",EDGE,{"derivedFrom":sQuery(id+"F13.wireOp",EDGE,"54823be7-8fca-406a-8078-c69425b5e832.3.3.0")}),-1.0]])]});
            var Q18;
            {var subQ1=sQuery(id+"F13.wireOp",EDGE,"E98.1.0.0");Q18=makeQuery(id+"F13.imprint","IMPRINT",FACE,{"disambiguationData":[TD([[makeQuery(id+"F13.imprint","IMPRINT",EDGE,{"derivedFrom":subQ1}),1.0]])]});}
            var Q19;
            Q19=makeQuery(id+"F13.imprint","IMPRINT",FACE,{"disambiguationData":[TD([[makeQuery(id+"F13.imprint","IMPRINT",EDGE,{"derivedFrom":sQuery(id+"F13.wireOp",EDGE,"E98.1.0.4")}),1.0]])]});
            var Q20;
            {var subQ0=sQuery(id+"F13.wireOp",EDGE,"E98.1.0.1");Q20=makeQuery(id+"F13.imprint","IMPRINT",FACE,{"disambiguationData":[TD([[makeQuery(id+"F13.imprint","IMPRINT",EDGE,{"derivedFrom":subQ0}),-1.0]])]});}
            var Q21;
            {var subQ0=sQuery(id+"F13.wireOp",EDGE,"E98.2.0.1");Q21=makeQuery(id+"F13.imprint","IMPRINT",FACE,{"disambiguationData":[TD([[makeQuery(id+"F13.imprint","IMPRINT",EDGE,{"derivedFrom":subQ0}),-1.0]])]});}
            var Q22;
            {var subQ1=sQuery(id+"F13.wireOp",EDGE,"E98.2.0.0");Q22=makeQuery(id+"F13.imprint","IMPRINT",FACE,{"disambiguationData":[TD([[makeQuery(id+"F13.imprint","IMPRINT",EDGE,{"derivedFrom":subQ1}),1.0]])]});}
            var Q23;
            Q23=makeQuery(id+"F13.imprint","IMPRINT",FACE,{"disambiguationData":[TD([[makeQuery(id+"F13.imprint","IMPRINT",EDGE,{"derivedFrom":sQuery(id+"F13.wireOp",EDGE,"E98.2.0.4")}),1.0]])]});
            var Q24;
            Q24=makeQuery(id+"F13.imprint","IMPRINT",FACE,{"disambiguationData":[TD([[makeQuery(id+"F13.imprint","IMPRINT",EDGE,{"derivedFrom":sQuery(id+"F13.wireOp",EDGE,"E98.3.0.4")}),1.0]])]});
            var Q25;
            {var subQ1=sQuery(id+"F13.wireOp",EDGE,"E98.3.0.0");Q25=makeQuery(id+"F13.imprint","IMPRINT",FACE,{"disambiguationData":[TD([[makeQuery(id+"F13.imprint","IMPRINT",EDGE,{"derivedFrom":subQ1}),1.0]])]});}
            var Q26;
            {var subQ0=sQuery(id+"F13.wireOp",EDGE,"E98.3.0.1");Q26=makeQuery(id+"F13.imprint","IMPRINT",FACE,{"disambiguationData":[TD([[makeQuery(id+"F13.imprint","IMPRINT",EDGE,{"derivedFrom":subQ0}),-1.0]])]});}
            var Q27;
            Q27=makeQuery(id+"F13.imprint","IMPRINT",FACE,{"disambiguationData":[TD([[makeQuery(id+"F13.imprint","IMPRINT",EDGE,{"derivedFrom":sQuery(id+"F13.wireOp",EDGE,"E98.4.0.1")}),-1.0]])]});
            var Q28;
            Q28=makeQuery(id+"F13.imprint","IMPRINT",FACE,{"disambiguationData":[TD([[makeQuery(id+"F13.imprint","IMPRINT",EDGE,{"derivedFrom":sQuery(id+"F13.wireOp",EDGE,"E98.4.0.0")}),1.0]])]});
            var Q29;
            Q29=makeQuery(id+"F13.imprint","IMPRINT",FACE,{"disambiguationData":[TD([[makeQuery(id+"F13.imprint","IMPRINT",EDGE,{"derivedFrom":sQuery(id+"F13.wireOp",EDGE,"E98.4.0.4")}),1.0]])]});
            extrude(context, id + "F14", {"entities" : qUnion([Q0, Q1, Q2, Q3, Q4, Q5, Q6, Q7, Q8, Q9, Q10, Q11, Q12, Q13, Q14, Q15, Q16, Q17, Q18, Q19, Q20, Q21, Q22, Q23, Q24, Q25, Q26, Q27, Q28, Q29]), "operationType" : NewBodyOperationType.REMOVE, "oppositeDirection" : true, "depth" : 2 * mm, "offsetDistance" : 25 * mm});
        }
        {
            var Q0;
            Q0=makeQuery(id+"F14.boolean.opBoolean","COPY",EDGE,{"derivedFrom":makeQuery(id+"F14.opExtrude","CAP_EDGE",EDGE,{"disambiguationData":[OSD([sQuery(id+"F13.wireOp",EDGE,"E90")])],"isStart":true})});
            var Q1;
            Q1=makeQuery(id+"F14.boolean.opBoolean","COPY",EDGE,{"derivedFrom":makeQuery(id+"F14.opExtrude","CAP_EDGE",EDGE,{"disambiguationData":[OSD([sQuery(id+"F13.wireOp",EDGE,"E93")])],"isStart":true})});
            var Q2;
            Q2=makeQuery(id+"F14.boolean.opBoolean","COPY",EDGE,{"derivedFrom":makeQuery(id+"F14.opExtrude","CAP_EDGE",EDGE,{"disambiguationData":[OSD([sQuery(id+"F13.wireOp",EDGE,"E92")])],"isStart":true})});
            var Q3;
            Q3=makeQuery(id+"F14.boolean.opBoolean","COPY",EDGE,{"derivedFrom":makeQuery(id+"F14.opExtrude","CAP_EDGE",EDGE,{"disambiguationData":[OSD([sQuery(id+"F13.wireOp",EDGE,"E89")])],"isStart":true})});
            var Q4;
            Q4=makeQuery(id+"F14.boolean.opBoolean","COPY",EDGE,{"derivedFrom":makeQuery(id+"F14.opExtrude","CAP_EDGE",EDGE,{"disambiguationData":[OSD([sQuery(id+"F13.wireOp",EDGE,"E96")])],"isStart":true})});
            var Q5;
            Q5=makeQuery(id+"F14.boolean.opBoolean","COPY",EDGE,{"derivedFrom":makeQuery(id+"F14.opExtrude","CAP_EDGE",EDGE,{"disambiguationData":[OSD([sQuery(id+"F13.wireOp",EDGE,"E97")])],"isStart":true})});
            var Q6;
            Q6=makeQuery(id+"F14.boolean.opBoolean","COPY",EDGE,{"derivedFrom":makeQuery(id+"F14.opExtrude","CAP_EDGE",EDGE,{"disambiguationData":[OSD([sQuery(id+"F13.wireOp",EDGE,"d3e0095a-e30d-40a6-bb55-9c31538d2f1b.1.0.3")])],"isStart":true})});
            var Q7;
            Q7=makeQuery(id+"F14.boolean.opBoolean","COPY",EDGE,{"derivedFrom":makeQuery(id+"F14.opExtrude","CAP_EDGE",EDGE,{"disambiguationData":[OSD([sQuery(id+"F13.wireOp",EDGE,"d3e0095a-e30d-40a6-bb55-9c31538d2f1b.1.0.7")])],"isStart":true})});
            var Q8;
            Q8=makeQuery(id+"F14.boolean.opBoolean","COPY",EDGE,{"derivedFrom":makeQuery(id+"F14.opExtrude","CAP_EDGE",EDGE,{"disambiguationData":[OSD([sQuery(id+"F13.wireOp",EDGE,"d3e0095a-e30d-40a6-bb55-9c31538d2f1b.1.0.2")])],"isStart":true})});
            var Q9;
            Q9=makeQuery(id+"F14.boolean.opBoolean","COPY",EDGE,{"derivedFrom":makeQuery(id+"F14.opExtrude","CAP_EDGE",EDGE,{"disambiguationData":[OSD([sQuery(id+"F13.wireOp",EDGE,"d3e0095a-e30d-40a6-bb55-9c31538d2f1b.1.0.4")])],"isStart":true})});
            var Q10;
            Q10=makeQuery(id+"F14.boolean.opBoolean","COPY",EDGE,{"derivedFrom":makeQuery(id+"F14.opExtrude","CAP_EDGE",EDGE,{"disambiguationData":[OSD([sQuery(id+"F13.wireOp",EDGE,"d3e0095a-e30d-40a6-bb55-9c31538d2f1b.1.0.1")])],"isStart":true})});
            var Q11;
            Q11=makeQuery(id+"F14.boolean.opBoolean","COPY",EDGE,{"derivedFrom":makeQuery(id+"F14.opExtrude","CAP_EDGE",EDGE,{"disambiguationData":[OSD([sQuery(id+"F13.wireOp",EDGE,"d3e0095a-e30d-40a6-bb55-9c31538d2f1b.1.0.5")])],"isStart":true})});
            var Q12;
            Q12=makeQuery(id+"F14.boolean.opBoolean","COPY",EDGE,{"derivedFrom":makeQuery(id+"F14.opExtrude","CAP_EDGE",EDGE,{"disambiguationData":[OSD([sQuery(id+"F13.wireOp",EDGE,"d3e0095a-e30d-40a6-bb55-9c31538d2f1b.2.0.5")])],"isStart":true})});
            var Q13;
            Q13=makeQuery(id+"F14.boolean.opBoolean","COPY",EDGE,{"derivedFrom":makeQuery(id+"F14.opExtrude","CAP_EDGE",EDGE,{"disambiguationData":[OSD([sQuery(id+"F13.wireOp",EDGE,"d3e0095a-e30d-40a6-bb55-9c31538d2f1b.2.0.3")])],"isStart":true})});
            var Q14;
            Q14=makeQuery(id+"F14.boolean.opBoolean","COPY",EDGE,{"derivedFrom":makeQuery(id+"F14.opExtrude","CAP_EDGE",EDGE,{"disambiguationData":[OSD([sQuery(id+"F13.wireOp",EDGE,"d3e0095a-e30d-40a6-bb55-9c31538d2f1b.2.0.4")])],"isStart":true})});
            var Q15;
            Q15=makeQuery(id+"F14.boolean.opBoolean","COPY",EDGE,{"derivedFrom":makeQuery(id+"F14.opExtrude","CAP_EDGE",EDGE,{"disambiguationData":[OSD([sQuery(id+"F13.wireOp",EDGE,"d3e0095a-e30d-40a6-bb55-9c31538d2f1b.2.0.2")])],"isStart":true})});
            var Q16;
            Q16=makeQuery(id+"F14.boolean.opBoolean","COPY",EDGE,{"derivedFrom":makeQuery(id+"F14.opExtrude","CAP_EDGE",EDGE,{"disambiguationData":[OSD([sQuery(id+"F13.wireOp",EDGE,"d3e0095a-e30d-40a6-bb55-9c31538d2f1b.2.0.7")])],"isStart":true})});
            var Q17;
            Q17=makeQuery(id+"F14.boolean.opBoolean","COPY",EDGE,{"derivedFrom":makeQuery(id+"F14.opExtrude","CAP_EDGE",EDGE,{"disambiguationData":[OSD([sQuery(id+"F13.wireOp",EDGE,"d3e0095a-e30d-40a6-bb55-9c31538d2f1b.2.0.1")])],"isStart":true})});
            var Q18;
            Q18=makeQuery(id+"F14.boolean.opBoolean","COPY",EDGE,{"derivedFrom":makeQuery(id+"F14.opExtrude","CAP_EDGE",EDGE,{"disambiguationData":[OSD([sQuery(id+"F13.wireOp",EDGE,"d3e0095a-e30d-40a6-bb55-9c31538d2f1b.3.0.5")])],"isStart":true})});
            var Q19;
            Q19=makeQuery(id+"F14.boolean.opBoolean","COPY",EDGE,{"derivedFrom":makeQuery(id+"F14.opExtrude","CAP_EDGE",EDGE,{"disambiguationData":[OSD([sQuery(id+"F13.wireOp",EDGE,"d3e0095a-e30d-40a6-bb55-9c31538d2f1b.3.0.3")])],"isStart":true})});
            var Q20;
            Q20=makeQuery(id+"F14.boolean.opBoolean","COPY",EDGE,{"derivedFrom":makeQuery(id+"F14.opExtrude","CAP_EDGE",EDGE,{"disambiguationData":[OSD([sQuery(id+"F13.wireOp",EDGE,"d3e0095a-e30d-40a6-bb55-9c31538d2f1b.3.0.4")])],"isStart":true})});
            var Q21;
            Q21=makeQuery(id+"F14.boolean.opBoolean","COPY",EDGE,{"derivedFrom":makeQuery(id+"F14.opExtrude","CAP_EDGE",EDGE,{"disambiguationData":[OSD([sQuery(id+"F13.wireOp",EDGE,"d3e0095a-e30d-40a6-bb55-9c31538d2f1b.3.0.2")])],"isStart":true})});
            var Q22;
            Q22=makeQuery(id+"F14.boolean.opBoolean","COPY",EDGE,{"derivedFrom":makeQuery(id+"F14.opExtrude","CAP_EDGE",EDGE,{"disambiguationData":[OSD([sQuery(id+"F13.wireOp",EDGE,"d3e0095a-e30d-40a6-bb55-9c31538d2f1b.3.0.7")])],"isStart":true})});
            var Q23;
            Q23=makeQuery(id+"F14.boolean.opBoolean","COPY",EDGE,{"derivedFrom":makeQuery(id+"F14.opExtrude","CAP_EDGE",EDGE,{"disambiguationData":[OSD([sQuery(id+"F13.wireOp",EDGE,"d3e0095a-e30d-40a6-bb55-9c31538d2f1b.3.0.1")])],"isStart":true})});
            var Q24;
            Q24=makeQuery(id+"F14.boolean.opBoolean","COPY",EDGE,{"derivedFrom":makeQuery(id+"F14.opExtrude","CAP_EDGE",EDGE,{"disambiguationData":[OSD([sQuery(id+"F13.wireOp",EDGE,"d3e0095a-e30d-40a6-bb55-9c31538d2f1b.4.0.5")])],"isStart":true})});
            var Q25;
            Q25=makeQuery(id+"F14.boolean.opBoolean","COPY",EDGE,{"derivedFrom":makeQuery(id+"F14.opExtrude","CAP_EDGE",EDGE,{"disambiguationData":[OSD([sQuery(id+"F13.wireOp",EDGE,"d3e0095a-e30d-40a6-bb55-9c31538d2f1b.4.0.1")])],"isStart":true})});
            var Q26;
            Q26=makeQuery(id+"F14.boolean.opBoolean","COPY",EDGE,{"derivedFrom":makeQuery(id+"F14.opExtrude","CAP_EDGE",EDGE,{"disambiguationData":[OSD([sQuery(id+"F13.wireOp",EDGE,"d3e0095a-e30d-40a6-bb55-9c31538d2f1b.4.0.7")])],"isStart":true})});
            var Q27;
            Q27=makeQuery(id+"F14.boolean.opBoolean","COPY",EDGE,{"derivedFrom":makeQuery(id+"F14.opExtrude","CAP_EDGE",EDGE,{"disambiguationData":[OSD([sQuery(id+"F13.wireOp",EDGE,"d3e0095a-e30d-40a6-bb55-9c31538d2f1b.4.0.3")])],"isStart":true})});
            var Q28;
            Q28=makeQuery(id+"F14.boolean.opBoolean","COPY",EDGE,{"derivedFrom":makeQuery(id+"F14.opExtrude","CAP_EDGE",EDGE,{"disambiguationData":[OSD([sQuery(id+"F13.wireOp",EDGE,"d3e0095a-e30d-40a6-bb55-9c31538d2f1b.4.0.4")])],"isStart":true})});
            var Q29;
            Q29=makeQuery(id+"F14.boolean.opBoolean","COPY",EDGE,{"derivedFrom":makeQuery(id+"F14.opExtrude","CAP_EDGE",EDGE,{"disambiguationData":[OSD([sQuery(id+"F13.wireOp",EDGE,"d3e0095a-e30d-40a6-bb55-9c31538d2f1b.4.0.2")])],"isStart":true})});
            var Q30;
            {var subQ0=sQuery(id+"F0.wireOp",EDGE,"E61.top");Q30=makeQuery(id+"F14.boolean.opBoolean","INTERSECT",EDGE,{"derivedFrom":[makeQuery(id+"F4.boolean.opBoolean","MERGE",FACE,{"derivedFrom":[makeQuery(id+"F3.opExtrude","SWEPT_FACE",FACE,{"disambiguationData":[OSD([subQ0]),TDD([makeQuery(id+"F0.imprint","IMPRINT",EDGE,{"disambiguationData":[TD([[makeQuery(id+"F0.imprint","INTERSECT",VERTEX,{"derivedFrom":[subQ0,sQuery(id+"F0.wireOp",EDGE,"E77")]}),-1.0]])],"derivedFrom":subQ0}),makeQuery(id+"F0.imprint","IMPRINT",EDGE,{"disambiguationData":[TD([[makeQuery(id+"F0.imprint","INTERSECT",VERTEX,{"derivedFrom":[subQ0,sQuery(id+"F0.wireOp",EDGE,"E78")]}),1.0]])],"derivedFrom":subQ0})])]}),makeQuery(id+"F3.opExtrude","SWEPT_FACE",FACE,{"disambiguationData":[OSD([subQ0]),TDD([makeQuery(id+"F0.imprint","IMPRINT",EDGE,{"disambiguationData":[TD([[makeQuery(id+"F0.imprint","INTERSECT",VERTEX,{"derivedFrom":[subQ0,sQuery(id+"F0.wireOp",EDGE,"E62")]}),-1.0]])],"derivedFrom":subQ0})])]}),makeQuery(id+"F4.opExtrude","SWEPT_FACE",FACE,{"disambiguationData":[OSD([subQ0])]})]}),makeQuery(id+"F14.opExtrude","SWEPT_FACE",FACE,{"disambiguationData":[OSD([sQuery(id+"F13.wireOp",EDGE,"E90")])]})]});}
            var Q31;
            {var subQ0=sQuery(id+"F0.wireOp",EDGE,"E61.top");Q31=makeQuery(id+"F14.boolean.opBoolean","INTERSECT",EDGE,{"derivedFrom":[makeQuery(id+"F4.boolean.opBoolean","MERGE",FACE,{"derivedFrom":[makeQuery(id+"F3.opExtrude","SWEPT_FACE",FACE,{"disambiguationData":[OSD([subQ0]),TDD([makeQuery(id+"F0.imprint","IMPRINT",EDGE,{"disambiguationData":[TD([[makeQuery(id+"F0.imprint","INTERSECT",VERTEX,{"derivedFrom":[subQ0,sQuery(id+"F0.wireOp",EDGE,"E77")]}),-1.0]])],"derivedFrom":subQ0}),makeQuery(id+"F0.imprint","IMPRINT",EDGE,{"disambiguationData":[TD([[makeQuery(id+"F0.imprint","INTERSECT",VERTEX,{"derivedFrom":[subQ0,sQuery(id+"F0.wireOp",EDGE,"E78")]}),1.0]])],"derivedFrom":subQ0})])]}),makeQuery(id+"F3.opExtrude","SWEPT_FACE",FACE,{"disambiguationData":[OSD([subQ0]),TDD([makeQuery(id+"F0.imprint","IMPRINT",EDGE,{"disambiguationData":[TD([[makeQuery(id+"F0.imprint","INTERSECT",VERTEX,{"derivedFrom":[subQ0,sQuery(id+"F0.wireOp",EDGE,"E62")]}),-1.0]])],"derivedFrom":subQ0})])]}),makeQuery(id+"F4.opExtrude","SWEPT_FACE",FACE,{"disambiguationData":[OSD([subQ0])]})]}),makeQuery(id+"F14.opExtrude","SWEPT_FACE",FACE,{"disambiguationData":[OSD([sQuery(id+"F13.wireOp",EDGE,"E93")])]})]});}
            var Q32;
            {var subQ0=sQuery(id+"F0.wireOp",EDGE,"E61.top");Q32=makeQuery(id+"F14.boolean.opBoolean","INTERSECT",EDGE,{"derivedFrom":[makeQuery(id+"F4.boolean.opBoolean","MERGE",FACE,{"derivedFrom":[makeQuery(id+"F3.opExtrude","SWEPT_FACE",FACE,{"disambiguationData":[OSD([subQ0]),TDD([makeQuery(id+"F0.imprint","IMPRINT",EDGE,{"disambiguationData":[TD([[makeQuery(id+"F0.imprint","INTERSECT",VERTEX,{"derivedFrom":[subQ0,sQuery(id+"F0.wireOp",EDGE,"E77")]}),-1.0]])],"derivedFrom":subQ0}),makeQuery(id+"F0.imprint","IMPRINT",EDGE,{"disambiguationData":[TD([[makeQuery(id+"F0.imprint","INTERSECT",VERTEX,{"derivedFrom":[subQ0,sQuery(id+"F0.wireOp",EDGE,"E78")]}),1.0]])],"derivedFrom":subQ0})])]}),makeQuery(id+"F3.opExtrude","SWEPT_FACE",FACE,{"disambiguationData":[OSD([subQ0]),TDD([makeQuery(id+"F0.imprint","IMPRINT",EDGE,{"disambiguationData":[TD([[makeQuery(id+"F0.imprint","INTERSECT",VERTEX,{"derivedFrom":[subQ0,sQuery(id+"F0.wireOp",EDGE,"E62")]}),-1.0]])],"derivedFrom":subQ0})])]}),makeQuery(id+"F4.opExtrude","SWEPT_FACE",FACE,{"disambiguationData":[OSD([subQ0])]})]}),makeQuery(id+"F14.opExtrude","SWEPT_FACE",FACE,{"disambiguationData":[OSD([sQuery(id+"F13.wireOp",EDGE,"E92")])]})]});}
            var Q33;
            {var subQ0=sQuery(id+"F0.wireOp",EDGE,"E61.top");Q33=makeQuery(id+"F14.boolean.opBoolean","INTERSECT",EDGE,{"derivedFrom":[makeQuery(id+"F4.boolean.opBoolean","MERGE",FACE,{"derivedFrom":[makeQuery(id+"F3.opExtrude","SWEPT_FACE",FACE,{"disambiguationData":[OSD([subQ0]),TDD([makeQuery(id+"F0.imprint","IMPRINT",EDGE,{"disambiguationData":[TD([[makeQuery(id+"F0.imprint","INTERSECT",VERTEX,{"derivedFrom":[subQ0,sQuery(id+"F0.wireOp",EDGE,"E77")]}),-1.0]])],"derivedFrom":subQ0}),makeQuery(id+"F0.imprint","IMPRINT",EDGE,{"disambiguationData":[TD([[makeQuery(id+"F0.imprint","INTERSECT",VERTEX,{"derivedFrom":[subQ0,sQuery(id+"F0.wireOp",EDGE,"E78")]}),1.0]])],"derivedFrom":subQ0})])]}),makeQuery(id+"F3.opExtrude","SWEPT_FACE",FACE,{"disambiguationData":[OSD([subQ0]),TDD([makeQuery(id+"F0.imprint","IMPRINT",EDGE,{"disambiguationData":[TD([[makeQuery(id+"F0.imprint","INTERSECT",VERTEX,{"derivedFrom":[subQ0,sQuery(id+"F0.wireOp",EDGE,"E62")]}),-1.0]])],"derivedFrom":subQ0})])]}),makeQuery(id+"F4.opExtrude","SWEPT_FACE",FACE,{"disambiguationData":[OSD([subQ0])]})]}),makeQuery(id+"F14.opExtrude","SWEPT_FACE",FACE,{"disambiguationData":[OSD([sQuery(id+"F13.wireOp",EDGE,"E97")])]})]});}
            var Q34;
            {var subQ0=sQuery(id+"F0.wireOp",EDGE,"E61.top");Q34=makeQuery(id+"F14.boolean.opBoolean","INTERSECT",EDGE,{"derivedFrom":[makeQuery(id+"F4.boolean.opBoolean","MERGE",FACE,{"derivedFrom":[makeQuery(id+"F3.opExtrude","SWEPT_FACE",FACE,{"disambiguationData":[OSD([subQ0]),TDD([makeQuery(id+"F0.imprint","IMPRINT",EDGE,{"disambiguationData":[TD([[makeQuery(id+"F0.imprint","INTERSECT",VERTEX,{"derivedFrom":[subQ0,sQuery(id+"F0.wireOp",EDGE,"E77")]}),-1.0]])],"derivedFrom":subQ0}),makeQuery(id+"F0.imprint","IMPRINT",EDGE,{"disambiguationData":[TD([[makeQuery(id+"F0.imprint","INTERSECT",VERTEX,{"derivedFrom":[subQ0,sQuery(id+"F0.wireOp",EDGE,"E78")]}),1.0]])],"derivedFrom":subQ0})])]}),makeQuery(id+"F3.opExtrude","SWEPT_FACE",FACE,{"disambiguationData":[OSD([subQ0]),TDD([makeQuery(id+"F0.imprint","IMPRINT",EDGE,{"disambiguationData":[TD([[makeQuery(id+"F0.imprint","INTERSECT",VERTEX,{"derivedFrom":[subQ0,sQuery(id+"F0.wireOp",EDGE,"E62")]}),-1.0]])],"derivedFrom":subQ0})])]}),makeQuery(id+"F4.opExtrude","SWEPT_FACE",FACE,{"disambiguationData":[OSD([subQ0])]})]}),makeQuery(id+"F14.opExtrude","SWEPT_FACE",FACE,{"disambiguationData":[OSD([sQuery(id+"F13.wireOp",EDGE,"E96")])]})]});}
            var Q35;
            {var subQ0=sQuery(id+"F0.wireOp",EDGE,"E61.top");Q35=makeQuery(id+"F14.boolean.opBoolean","INTERSECT",EDGE,{"derivedFrom":[makeQuery(id+"F4.boolean.opBoolean","MERGE",FACE,{"derivedFrom":[makeQuery(id+"F3.opExtrude","SWEPT_FACE",FACE,{"disambiguationData":[OSD([subQ0]),TDD([makeQuery(id+"F0.imprint","IMPRINT",EDGE,{"disambiguationData":[TD([[makeQuery(id+"F0.imprint","INTERSECT",VERTEX,{"derivedFrom":[subQ0,sQuery(id+"F0.wireOp",EDGE,"E77")]}),-1.0]])],"derivedFrom":subQ0}),makeQuery(id+"F0.imprint","IMPRINT",EDGE,{"disambiguationData":[TD([[makeQuery(id+"F0.imprint","INTERSECT",VERTEX,{"derivedFrom":[subQ0,sQuery(id+"F0.wireOp",EDGE,"E78")]}),1.0]])],"derivedFrom":subQ0})])]}),makeQuery(id+"F3.opExtrude","SWEPT_FACE",FACE,{"disambiguationData":[OSD([subQ0]),TDD([makeQuery(id+"F0.imprint","IMPRINT",EDGE,{"disambiguationData":[TD([[makeQuery(id+"F0.imprint","INTERSECT",VERTEX,{"derivedFrom":[subQ0,sQuery(id+"F0.wireOp",EDGE,"E62")]}),-1.0]])],"derivedFrom":subQ0})])]}),makeQuery(id+"F4.opExtrude","SWEPT_FACE",FACE,{"disambiguationData":[OSD([subQ0])]})]}),makeQuery(id+"F14.opExtrude","SWEPT_FACE",FACE,{"disambiguationData":[OSD([sQuery(id+"F13.wireOp",EDGE,"E89")])]})]});}
            var Q36;
            {var subQ0=sQuery(id+"F0.wireOp",EDGE,"E61.top");var subQ2=makeQuery(id+"F4.boolean.opBoolean","MERGE",FACE,{"derivedFrom":[makeQuery(id+"F3.opExtrude","SWEPT_FACE",FACE,{"disambiguationData":[OSD([subQ0]),TDD([makeQuery(id+"F0.imprint","IMPRINT",EDGE,{"disambiguationData":[TD([[makeQuery(id+"F0.imprint","INTERSECT",VERTEX,{"derivedFrom":[subQ0,sQuery(id+"F0.wireOp",EDGE,"E77")]}),-1.0]])],"derivedFrom":subQ0}),makeQuery(id+"F0.imprint","IMPRINT",EDGE,{"disambiguationData":[TD([[makeQuery(id+"F0.imprint","INTERSECT",VERTEX,{"derivedFrom":[subQ0,sQuery(id+"F0.wireOp",EDGE,"E78")]}),1.0]])],"derivedFrom":subQ0})])]}),makeQuery(id+"F3.opExtrude","SWEPT_FACE",FACE,{"disambiguationData":[OSD([subQ0]),TDD([makeQuery(id+"F0.imprint","IMPRINT",EDGE,{"disambiguationData":[TD([[makeQuery(id+"F0.imprint","INTERSECT",VERTEX,{"derivedFrom":[subQ0,sQuery(id+"F0.wireOp",EDGE,"E62")]}),-1.0]])],"derivedFrom":subQ0})])]}),makeQuery(id+"F4.opExtrude","SWEPT_FACE",FACE,{"disambiguationData":[OSD([subQ0])]})]});Q36=qUnion([makeQuery(id+"F14.boolean.opBoolean","INTERSECT",EDGE,{"derivedFrom":[subQ2,makeQuery(id+"F14.opExtrude","SWEPT_FACE",FACE,{"disambiguationData":[OSD([sQuery(id+"F13.wireOp",EDGE,"E89")])]})]}),makeQuery(id+"F14.boolean.opBoolean","INTERSECT",EDGE,{"derivedFrom":[subQ2,makeQuery(id+"F14.opExtrude","SWEPT_FACE",FACE,{"disambiguationData":[OSD([sQuery(id+"F13.wireOp",EDGE,"E90")])]})]}),makeQuery(id+"F14.boolean.opBoolean","INTERSECT",EDGE,{"derivedFrom":[subQ2,makeQuery(id+"F14.opExtrude","SWEPT_FACE",FACE,{"disambiguationData":[OSD([sQuery(id+"F13.wireOp",EDGE,"E92")])]})]}),makeQuery(id+"F14.boolean.opBoolean","INTERSECT",EDGE,{"derivedFrom":[subQ2,makeQuery(id+"F14.opExtrude","SWEPT_FACE",FACE,{"disambiguationData":[OSD([sQuery(id+"F13.wireOp",EDGE,"E93")])]})]}),makeQuery(id+"F14.boolean.opBoolean","INTERSECT",EDGE,{"derivedFrom":[subQ2,makeQuery(id+"F14.opExtrude","SWEPT_FACE",FACE,{"disambiguationData":[OSD([sQuery(id+"F13.wireOp",EDGE,"E96")])]})]}),makeQuery(id+"F14.boolean.opBoolean","INTERSECT",EDGE,{"derivedFrom":[subQ2,makeQuery(id+"F14.opExtrude","SWEPT_FACE",FACE,{"disambiguationData":[OSD([sQuery(id+"F13.wireOp",EDGE,"E97")])]})]}),makeQuery(id+"F14.boolean.opBoolean","INTERSECT",EDGE,{"derivedFrom":[subQ2,makeQuery(id+"F14.opExtrude","SWEPT_FACE",FACE,{"disambiguationData":[OSD([sQuery(id+"F13.wireOp",EDGE,"E98.1.0.0")])]})]}),makeQuery(id+"F14.boolean.opBoolean","INTERSECT",EDGE,{"derivedFrom":[subQ2,makeQuery(id+"F14.opExtrude","SWEPT_FACE",FACE,{"disambiguationData":[OSD([sQuery(id+"F13.wireOp",EDGE,"E98.1.0.1")])]})]}),makeQuery(id+"F14.boolean.opBoolean","INTERSECT",EDGE,{"derivedFrom":[subQ2,makeQuery(id+"F14.opExtrude","SWEPT_FACE",FACE,{"disambiguationData":[OSD([sQuery(id+"F13.wireOp",EDGE,"E98.1.0.3")])]})]}),makeQuery(id+"F14.boolean.opBoolean","INTERSECT",EDGE,{"derivedFrom":[subQ2,makeQuery(id+"F14.opExtrude","SWEPT_FACE",FACE,{"disambiguationData":[OSD([sQuery(id+"F13.wireOp",EDGE,"E98.1.0.4")])]})]}),makeQuery(id+"F14.boolean.opBoolean","INTERSECT",EDGE,{"derivedFrom":[subQ2,makeQuery(id+"F14.opExtrude","SWEPT_FACE",FACE,{"disambiguationData":[OSD([sQuery(id+"F13.wireOp",EDGE,"E98.1.0.5")])]})]}),makeQuery(id+"F14.boolean.opBoolean","INTERSECT",EDGE,{"derivedFrom":[subQ2,makeQuery(id+"F14.opExtrude","SWEPT_FACE",FACE,{"disambiguationData":[OSD([sQuery(id+"F13.wireOp",EDGE,"E98.1.0.6")])]})]}),makeQuery(id+"F14.boolean.opBoolean","INTERSECT",EDGE,{"derivedFrom":[subQ2,makeQuery(id+"F14.opExtrude","SWEPT_FACE",FACE,{"disambiguationData":[OSD([sQuery(id+"F13.wireOp",EDGE,"E98.2.0.0")])]})]}),makeQuery(id+"F14.boolean.opBoolean","INTERSECT",EDGE,{"derivedFrom":[subQ2,makeQuery(id+"F14.opExtrude","SWEPT_FACE",FACE,{"disambiguationData":[OSD([sQuery(id+"F13.wireOp",EDGE,"E98.2.0.1")])]})]}),makeQuery(id+"F14.boolean.opBoolean","INTERSECT",EDGE,{"derivedFrom":[subQ2,makeQuery(id+"F14.opExtrude","SWEPT_FACE",FACE,{"disambiguationData":[OSD([sQuery(id+"F13.wireOp",EDGE,"E98.2.0.3")])]})]}),makeQuery(id+"F14.boolean.opBoolean","INTERSECT",EDGE,{"derivedFrom":[subQ2,makeQuery(id+"F14.opExtrude","SWEPT_FACE",FACE,{"disambiguationData":[OSD([sQuery(id+"F13.wireOp",EDGE,"E98.2.0.4")])]})]}),makeQuery(id+"F14.boolean.opBoolean","INTERSECT",EDGE,{"derivedFrom":[subQ2,makeQuery(id+"F14.opExtrude","SWEPT_FACE",FACE,{"disambiguationData":[OSD([sQuery(id+"F13.wireOp",EDGE,"E98.2.0.5")])]})]}),makeQuery(id+"F14.boolean.opBoolean","INTERSECT",EDGE,{"derivedFrom":[subQ2,makeQuery(id+"F14.opExtrude","SWEPT_FACE",FACE,{"disambiguationData":[OSD([sQuery(id+"F13.wireOp",EDGE,"E98.2.0.6")])]})]}),makeQuery(id+"F14.boolean.opBoolean","INTERSECT",EDGE,{"derivedFrom":[subQ2,makeQuery(id+"F14.opExtrude","SWEPT_FACE",FACE,{"disambiguationData":[OSD([sQuery(id+"F13.wireOp",EDGE,"E98.3.0.0")])]})]}),makeQuery(id+"F14.boolean.opBoolean","INTERSECT",EDGE,{"derivedFrom":[subQ2,makeQuery(id+"F14.opExtrude","SWEPT_FACE",FACE,{"disambiguationData":[OSD([sQuery(id+"F13.wireOp",EDGE,"E98.3.0.1")])]})]}),makeQuery(id+"F14.boolean.opBoolean","INTERSECT",EDGE,{"derivedFrom":[subQ2,makeQuery(id+"F14.opExtrude","SWEPT_FACE",FACE,{"disambiguationData":[OSD([sQuery(id+"F13.wireOp",EDGE,"E98.3.0.3")])]})]}),makeQuery(id+"F14.boolean.opBoolean","INTERSECT",EDGE,{"derivedFrom":[subQ2,makeQuery(id+"F14.opExtrude","SWEPT_FACE",FACE,{"disambiguationData":[OSD([sQuery(id+"F13.wireOp",EDGE,"E98.3.0.4")])]})]}),makeQuery(id+"F14.boolean.opBoolean","INTERSECT",EDGE,{"derivedFrom":[subQ2,makeQuery(id+"F14.opExtrude","SWEPT_FACE",FACE,{"disambiguationData":[OSD([sQuery(id+"F13.wireOp",EDGE,"E98.3.0.5")])]})]}),makeQuery(id+"F14.boolean.opBoolean","INTERSECT",EDGE,{"derivedFrom":[subQ2,makeQuery(id+"F14.opExtrude","SWEPT_FACE",FACE,{"disambiguationData":[OSD([sQuery(id+"F13.wireOp",EDGE,"E98.3.0.6")])]})]})]);}
            var Q37;
            {var subQ0=sQuery(id+"F0.wireOp",EDGE,"E61.top");var subQ2=makeQuery(id+"F4.boolean.opBoolean","MERGE",FACE,{"derivedFrom":[makeQuery(id+"F3.opExtrude","SWEPT_FACE",FACE,{"disambiguationData":[OSD([subQ0]),TDD([makeQuery(id+"F0.imprint","IMPRINT",EDGE,{"disambiguationData":[TD([[makeQuery(id+"F0.imprint","INTERSECT",VERTEX,{"derivedFrom":[subQ0,sQuery(id+"F0.wireOp",EDGE,"E77")]}),-1.0]])],"derivedFrom":subQ0}),makeQuery(id+"F0.imprint","IMPRINT",EDGE,{"disambiguationData":[TD([[makeQuery(id+"F0.imprint","INTERSECT",VERTEX,{"derivedFrom":[subQ0,sQuery(id+"F0.wireOp",EDGE,"E78")]}),1.0]])],"derivedFrom":subQ0})])]}),makeQuery(id+"F3.opExtrude","SWEPT_FACE",FACE,{"disambiguationData":[OSD([subQ0]),TDD([makeQuery(id+"F0.imprint","IMPRINT",EDGE,{"disambiguationData":[TD([[makeQuery(id+"F0.imprint","INTERSECT",VERTEX,{"derivedFrom":[subQ0,sQuery(id+"F0.wireOp",EDGE,"E62")]}),-1.0]])],"derivedFrom":subQ0})])]}),makeQuery(id+"F4.opExtrude","SWEPT_FACE",FACE,{"disambiguationData":[OSD([subQ0])]})]});Q37=qUnion([makeQuery(id+"F14.boolean.opBoolean","INTERSECT",EDGE,{"derivedFrom":[subQ2,makeQuery(id+"F14.opExtrude","SWEPT_FACE",FACE,{"disambiguationData":[OSD([sQuery(id+"F13.wireOp",EDGE,"E89")])]})]}),makeQuery(id+"F14.boolean.opBoolean","INTERSECT",EDGE,{"derivedFrom":[subQ2,makeQuery(id+"F14.opExtrude","SWEPT_FACE",FACE,{"disambiguationData":[OSD([sQuery(id+"F13.wireOp",EDGE,"E90")])]})]}),makeQuery(id+"F14.boolean.opBoolean","INTERSECT",EDGE,{"derivedFrom":[subQ2,makeQuery(id+"F14.opExtrude","SWEPT_FACE",FACE,{"disambiguationData":[OSD([sQuery(id+"F13.wireOp",EDGE,"E92")])]})]}),makeQuery(id+"F14.boolean.opBoolean","INTERSECT",EDGE,{"derivedFrom":[subQ2,makeQuery(id+"F14.opExtrude","SWEPT_FACE",FACE,{"disambiguationData":[OSD([sQuery(id+"F13.wireOp",EDGE,"E93")])]})]}),makeQuery(id+"F14.boolean.opBoolean","INTERSECT",EDGE,{"derivedFrom":[subQ2,makeQuery(id+"F14.opExtrude","SWEPT_FACE",FACE,{"disambiguationData":[OSD([sQuery(id+"F13.wireOp",EDGE,"E96")])]})]}),makeQuery(id+"F14.boolean.opBoolean","INTERSECT",EDGE,{"derivedFrom":[subQ2,makeQuery(id+"F14.opExtrude","SWEPT_FACE",FACE,{"disambiguationData":[OSD([sQuery(id+"F13.wireOp",EDGE,"E97")])]})]}),makeQuery(id+"F14.boolean.opBoolean","INTERSECT",EDGE,{"derivedFrom":[subQ2,makeQuery(id+"F14.opExtrude","SWEPT_FACE",FACE,{"disambiguationData":[OSD([sQuery(id+"F13.wireOp",EDGE,"E98.1.0.0")])]})]}),makeQuery(id+"F14.boolean.opBoolean","INTERSECT",EDGE,{"derivedFrom":[subQ2,makeQuery(id+"F14.opExtrude","SWEPT_FACE",FACE,{"disambiguationData":[OSD([sQuery(id+"F13.wireOp",EDGE,"E98.1.0.1")])]})]}),makeQuery(id+"F14.boolean.opBoolean","INTERSECT",EDGE,{"derivedFrom":[subQ2,makeQuery(id+"F14.opExtrude","SWEPT_FACE",FACE,{"disambiguationData":[OSD([sQuery(id+"F13.wireOp",EDGE,"E98.1.0.3")])]})]}),makeQuery(id+"F14.boolean.opBoolean","INTERSECT",EDGE,{"derivedFrom":[subQ2,makeQuery(id+"F14.opExtrude","SWEPT_FACE",FACE,{"disambiguationData":[OSD([sQuery(id+"F13.wireOp",EDGE,"E98.1.0.4")])]})]}),makeQuery(id+"F14.boolean.opBoolean","INTERSECT",EDGE,{"derivedFrom":[subQ2,makeQuery(id+"F14.opExtrude","SWEPT_FACE",FACE,{"disambiguationData":[OSD([sQuery(id+"F13.wireOp",EDGE,"E98.1.0.5")])]})]}),makeQuery(id+"F14.boolean.opBoolean","INTERSECT",EDGE,{"derivedFrom":[subQ2,makeQuery(id+"F14.opExtrude","SWEPT_FACE",FACE,{"disambiguationData":[OSD([sQuery(id+"F13.wireOp",EDGE,"E98.1.0.6")])]})]}),makeQuery(id+"F14.boolean.opBoolean","INTERSECT",EDGE,{"derivedFrom":[subQ2,makeQuery(id+"F14.opExtrude","SWEPT_FACE",FACE,{"disambiguationData":[OSD([sQuery(id+"F13.wireOp",EDGE,"E98.2.0.0")])]})]}),makeQuery(id+"F14.boolean.opBoolean","INTERSECT",EDGE,{"derivedFrom":[subQ2,makeQuery(id+"F14.opExtrude","SWEPT_FACE",FACE,{"disambiguationData":[OSD([sQuery(id+"F13.wireOp",EDGE,"E98.2.0.1")])]})]}),makeQuery(id+"F14.boolean.opBoolean","INTERSECT",EDGE,{"derivedFrom":[subQ2,makeQuery(id+"F14.opExtrude","SWEPT_FACE",FACE,{"disambiguationData":[OSD([sQuery(id+"F13.wireOp",EDGE,"E98.2.0.3")])]})]}),makeQuery(id+"F14.boolean.opBoolean","INTERSECT",EDGE,{"derivedFrom":[subQ2,makeQuery(id+"F14.opExtrude","SWEPT_FACE",FACE,{"disambiguationData":[OSD([sQuery(id+"F13.wireOp",EDGE,"E98.2.0.4")])]})]}),makeQuery(id+"F14.boolean.opBoolean","INTERSECT",EDGE,{"derivedFrom":[subQ2,makeQuery(id+"F14.opExtrude","SWEPT_FACE",FACE,{"disambiguationData":[OSD([sQuery(id+"F13.wireOp",EDGE,"E98.2.0.5")])]})]}),makeQuery(id+"F14.boolean.opBoolean","INTERSECT",EDGE,{"derivedFrom":[subQ2,makeQuery(id+"F14.opExtrude","SWEPT_FACE",FACE,{"disambiguationData":[OSD([sQuery(id+"F13.wireOp",EDGE,"E98.2.0.6")])]})]}),makeQuery(id+"F14.boolean.opBoolean","INTERSECT",EDGE,{"derivedFrom":[subQ2,makeQuery(id+"F14.opExtrude","SWEPT_FACE",FACE,{"disambiguationData":[OSD([sQuery(id+"F13.wireOp",EDGE,"E98.3.0.0")])]})]}),makeQuery(id+"F14.boolean.opBoolean","INTERSECT",EDGE,{"derivedFrom":[subQ2,makeQuery(id+"F14.opExtrude","SWEPT_FACE",FACE,{"disambiguationData":[OSD([sQuery(id+"F13.wireOp",EDGE,"E98.3.0.1")])]})]}),makeQuery(id+"F14.boolean.opBoolean","INTERSECT",EDGE,{"derivedFrom":[subQ2,makeQuery(id+"F14.opExtrude","SWEPT_FACE",FACE,{"disambiguationData":[OSD([sQuery(id+"F13.wireOp",EDGE,"E98.3.0.3")])]})]}),makeQuery(id+"F14.boolean.opBoolean","INTERSECT",EDGE,{"derivedFrom":[subQ2,makeQuery(id+"F14.opExtrude","SWEPT_FACE",FACE,{"disambiguationData":[OSD([sQuery(id+"F13.wireOp",EDGE,"E98.3.0.4")])]})]}),makeQuery(id+"F14.boolean.opBoolean","INTERSECT",EDGE,{"derivedFrom":[subQ2,makeQuery(id+"F14.opExtrude","SWEPT_FACE",FACE,{"disambiguationData":[OSD([sQuery(id+"F13.wireOp",EDGE,"E98.3.0.5")])]})]}),makeQuery(id+"F14.boolean.opBoolean","INTERSECT",EDGE,{"derivedFrom":[subQ2,makeQuery(id+"F14.opExtrude","SWEPT_FACE",FACE,{"disambiguationData":[OSD([sQuery(id+"F13.wireOp",EDGE,"E98.3.0.6")])]})]})]);}
            var Q38;
            {var subQ0=sQuery(id+"F0.wireOp",EDGE,"E61.top");var subQ2=makeQuery(id+"F4.boolean.opBoolean","MERGE",FACE,{"derivedFrom":[makeQuery(id+"F3.opExtrude","SWEPT_FACE",FACE,{"disambiguationData":[OSD([subQ0]),TDD([makeQuery(id+"F0.imprint","IMPRINT",EDGE,{"disambiguationData":[TD([[makeQuery(id+"F0.imprint","INTERSECT",VERTEX,{"derivedFrom":[subQ0,sQuery(id+"F0.wireOp",EDGE,"E77")]}),-1.0]])],"derivedFrom":subQ0}),makeQuery(id+"F0.imprint","IMPRINT",EDGE,{"disambiguationData":[TD([[makeQuery(id+"F0.imprint","INTERSECT",VERTEX,{"derivedFrom":[subQ0,sQuery(id+"F0.wireOp",EDGE,"E78")]}),1.0]])],"derivedFrom":subQ0})])]}),makeQuery(id+"F3.opExtrude","SWEPT_FACE",FACE,{"disambiguationData":[OSD([subQ0]),TDD([makeQuery(id+"F0.imprint","IMPRINT",EDGE,{"disambiguationData":[TD([[makeQuery(id+"F0.imprint","INTERSECT",VERTEX,{"derivedFrom":[subQ0,sQuery(id+"F0.wireOp",EDGE,"E62")]}),-1.0]])],"derivedFrom":subQ0})])]}),makeQuery(id+"F4.opExtrude","SWEPT_FACE",FACE,{"disambiguationData":[OSD([subQ0])]})]});Q38=qUnion([makeQuery(id+"F14.boolean.opBoolean","INTERSECT",EDGE,{"derivedFrom":[subQ2,makeQuery(id+"F14.opExtrude","SWEPT_FACE",FACE,{"disambiguationData":[OSD([sQuery(id+"F13.wireOp",EDGE,"E89")])]})]}),makeQuery(id+"F14.boolean.opBoolean","INTERSECT",EDGE,{"derivedFrom":[subQ2,makeQuery(id+"F14.opExtrude","SWEPT_FACE",FACE,{"disambiguationData":[OSD([sQuery(id+"F13.wireOp",EDGE,"E90")])]})]}),makeQuery(id+"F14.boolean.opBoolean","INTERSECT",EDGE,{"derivedFrom":[subQ2,makeQuery(id+"F14.opExtrude","SWEPT_FACE",FACE,{"disambiguationData":[OSD([sQuery(id+"F13.wireOp",EDGE,"E92")])]})]}),makeQuery(id+"F14.boolean.opBoolean","INTERSECT",EDGE,{"derivedFrom":[subQ2,makeQuery(id+"F14.opExtrude","SWEPT_FACE",FACE,{"disambiguationData":[OSD([sQuery(id+"F13.wireOp",EDGE,"E93")])]})]}),makeQuery(id+"F14.boolean.opBoolean","INTERSECT",EDGE,{"derivedFrom":[subQ2,makeQuery(id+"F14.opExtrude","SWEPT_FACE",FACE,{"disambiguationData":[OSD([sQuery(id+"F13.wireOp",EDGE,"E96")])]})]}),makeQuery(id+"F14.boolean.opBoolean","INTERSECT",EDGE,{"derivedFrom":[subQ2,makeQuery(id+"F14.opExtrude","SWEPT_FACE",FACE,{"disambiguationData":[OSD([sQuery(id+"F13.wireOp",EDGE,"E97")])]})]}),makeQuery(id+"F14.boolean.opBoolean","INTERSECT",EDGE,{"derivedFrom":[subQ2,makeQuery(id+"F14.opExtrude","SWEPT_FACE",FACE,{"disambiguationData":[OSD([sQuery(id+"F13.wireOp",EDGE,"E98.1.0.0")])]})]}),makeQuery(id+"F14.boolean.opBoolean","INTERSECT",EDGE,{"derivedFrom":[subQ2,makeQuery(id+"F14.opExtrude","SWEPT_FACE",FACE,{"disambiguationData":[OSD([sQuery(id+"F13.wireOp",EDGE,"E98.1.0.1")])]})]}),makeQuery(id+"F14.boolean.opBoolean","INTERSECT",EDGE,{"derivedFrom":[subQ2,makeQuery(id+"F14.opExtrude","SWEPT_FACE",FACE,{"disambiguationData":[OSD([sQuery(id+"F13.wireOp",EDGE,"E98.1.0.3")])]})]}),makeQuery(id+"F14.boolean.opBoolean","INTERSECT",EDGE,{"derivedFrom":[subQ2,makeQuery(id+"F14.opExtrude","SWEPT_FACE",FACE,{"disambiguationData":[OSD([sQuery(id+"F13.wireOp",EDGE,"E98.1.0.4")])]})]}),makeQuery(id+"F14.boolean.opBoolean","INTERSECT",EDGE,{"derivedFrom":[subQ2,makeQuery(id+"F14.opExtrude","SWEPT_FACE",FACE,{"disambiguationData":[OSD([sQuery(id+"F13.wireOp",EDGE,"E98.1.0.5")])]})]}),makeQuery(id+"F14.boolean.opBoolean","INTERSECT",EDGE,{"derivedFrom":[subQ2,makeQuery(id+"F14.opExtrude","SWEPT_FACE",FACE,{"disambiguationData":[OSD([sQuery(id+"F13.wireOp",EDGE,"E98.1.0.6")])]})]}),makeQuery(id+"F14.boolean.opBoolean","INTERSECT",EDGE,{"derivedFrom":[subQ2,makeQuery(id+"F14.opExtrude","SWEPT_FACE",FACE,{"disambiguationData":[OSD([sQuery(id+"F13.wireOp",EDGE,"E98.2.0.0")])]})]}),makeQuery(id+"F14.boolean.opBoolean","INTERSECT",EDGE,{"derivedFrom":[subQ2,makeQuery(id+"F14.opExtrude","SWEPT_FACE",FACE,{"disambiguationData":[OSD([sQuery(id+"F13.wireOp",EDGE,"E98.2.0.1")])]})]}),makeQuery(id+"F14.boolean.opBoolean","INTERSECT",EDGE,{"derivedFrom":[subQ2,makeQuery(id+"F14.opExtrude","SWEPT_FACE",FACE,{"disambiguationData":[OSD([sQuery(id+"F13.wireOp",EDGE,"E98.2.0.3")])]})]}),makeQuery(id+"F14.boolean.opBoolean","INTERSECT",EDGE,{"derivedFrom":[subQ2,makeQuery(id+"F14.opExtrude","SWEPT_FACE",FACE,{"disambiguationData":[OSD([sQuery(id+"F13.wireOp",EDGE,"E98.2.0.4")])]})]}),makeQuery(id+"F14.boolean.opBoolean","INTERSECT",EDGE,{"derivedFrom":[subQ2,makeQuery(id+"F14.opExtrude","SWEPT_FACE",FACE,{"disambiguationData":[OSD([sQuery(id+"F13.wireOp",EDGE,"E98.2.0.5")])]})]}),makeQuery(id+"F14.boolean.opBoolean","INTERSECT",EDGE,{"derivedFrom":[subQ2,makeQuery(id+"F14.opExtrude","SWEPT_FACE",FACE,{"disambiguationData":[OSD([sQuery(id+"F13.wireOp",EDGE,"E98.2.0.6")])]})]}),makeQuery(id+"F14.boolean.opBoolean","INTERSECT",EDGE,{"derivedFrom":[subQ2,makeQuery(id+"F14.opExtrude","SWEPT_FACE",FACE,{"disambiguationData":[OSD([sQuery(id+"F13.wireOp",EDGE,"E98.3.0.0")])]})]}),makeQuery(id+"F14.boolean.opBoolean","INTERSECT",EDGE,{"derivedFrom":[subQ2,makeQuery(id+"F14.opExtrude","SWEPT_FACE",FACE,{"disambiguationData":[OSD([sQuery(id+"F13.wireOp",EDGE,"E98.3.0.1")])]})]}),makeQuery(id+"F14.boolean.opBoolean","INTERSECT",EDGE,{"derivedFrom":[subQ2,makeQuery(id+"F14.opExtrude","SWEPT_FACE",FACE,{"disambiguationData":[OSD([sQuery(id+"F13.wireOp",EDGE,"E98.3.0.3")])]})]}),makeQuery(id+"F14.boolean.opBoolean","INTERSECT",EDGE,{"derivedFrom":[subQ2,makeQuery(id+"F14.opExtrude","SWEPT_FACE",FACE,{"disambiguationData":[OSD([sQuery(id+"F13.wireOp",EDGE,"E98.3.0.4")])]})]}),makeQuery(id+"F14.boolean.opBoolean","INTERSECT",EDGE,{"derivedFrom":[subQ2,makeQuery(id+"F14.opExtrude","SWEPT_FACE",FACE,{"disambiguationData":[OSD([sQuery(id+"F13.wireOp",EDGE,"E98.3.0.5")])]})]}),makeQuery(id+"F14.boolean.opBoolean","INTERSECT",EDGE,{"derivedFrom":[subQ2,makeQuery(id+"F14.opExtrude","SWEPT_FACE",FACE,{"disambiguationData":[OSD([sQuery(id+"F13.wireOp",EDGE,"E98.3.0.6")])]})]})]);}
            var Q39;
            {var subQ0=sQuery(id+"F0.wireOp",EDGE,"E61.top");var subQ2=makeQuery(id+"F4.boolean.opBoolean","MERGE",FACE,{"derivedFrom":[makeQuery(id+"F3.opExtrude","SWEPT_FACE",FACE,{"disambiguationData":[OSD([subQ0]),TDD([makeQuery(id+"F0.imprint","IMPRINT",EDGE,{"disambiguationData":[TD([[makeQuery(id+"F0.imprint","INTERSECT",VERTEX,{"derivedFrom":[subQ0,sQuery(id+"F0.wireOp",EDGE,"E77")]}),-1.0]])],"derivedFrom":subQ0}),makeQuery(id+"F0.imprint","IMPRINT",EDGE,{"disambiguationData":[TD([[makeQuery(id+"F0.imprint","INTERSECT",VERTEX,{"derivedFrom":[subQ0,sQuery(id+"F0.wireOp",EDGE,"E78")]}),1.0]])],"derivedFrom":subQ0})])]}),makeQuery(id+"F3.opExtrude","SWEPT_FACE",FACE,{"disambiguationData":[OSD([subQ0]),TDD([makeQuery(id+"F0.imprint","IMPRINT",EDGE,{"disambiguationData":[TD([[makeQuery(id+"F0.imprint","INTERSECT",VERTEX,{"derivedFrom":[subQ0,sQuery(id+"F0.wireOp",EDGE,"E62")]}),-1.0]])],"derivedFrom":subQ0})])]}),makeQuery(id+"F4.opExtrude","SWEPT_FACE",FACE,{"disambiguationData":[OSD([subQ0])]})]});Q39=qUnion([makeQuery(id+"F14.boolean.opBoolean","INTERSECT",EDGE,{"derivedFrom":[subQ2,makeQuery(id+"F14.opExtrude","SWEPT_FACE",FACE,{"disambiguationData":[OSD([sQuery(id+"F13.wireOp",EDGE,"E89")])]})]}),makeQuery(id+"F14.boolean.opBoolean","INTERSECT",EDGE,{"derivedFrom":[subQ2,makeQuery(id+"F14.opExtrude","SWEPT_FACE",FACE,{"disambiguationData":[OSD([sQuery(id+"F13.wireOp",EDGE,"E90")])]})]}),makeQuery(id+"F14.boolean.opBoolean","INTERSECT",EDGE,{"derivedFrom":[subQ2,makeQuery(id+"F14.opExtrude","SWEPT_FACE",FACE,{"disambiguationData":[OSD([sQuery(id+"F13.wireOp",EDGE,"E92")])]})]}),makeQuery(id+"F14.boolean.opBoolean","INTERSECT",EDGE,{"derivedFrom":[subQ2,makeQuery(id+"F14.opExtrude","SWEPT_FACE",FACE,{"disambiguationData":[OSD([sQuery(id+"F13.wireOp",EDGE,"E93")])]})]}),makeQuery(id+"F14.boolean.opBoolean","INTERSECT",EDGE,{"derivedFrom":[subQ2,makeQuery(id+"F14.opExtrude","SWEPT_FACE",FACE,{"disambiguationData":[OSD([sQuery(id+"F13.wireOp",EDGE,"E96")])]})]}),makeQuery(id+"F14.boolean.opBoolean","INTERSECT",EDGE,{"derivedFrom":[subQ2,makeQuery(id+"F14.opExtrude","SWEPT_FACE",FACE,{"disambiguationData":[OSD([sQuery(id+"F13.wireOp",EDGE,"E97")])]})]}),makeQuery(id+"F14.boolean.opBoolean","INTERSECT",EDGE,{"derivedFrom":[subQ2,makeQuery(id+"F14.opExtrude","SWEPT_FACE",FACE,{"disambiguationData":[OSD([sQuery(id+"F13.wireOp",EDGE,"E98.1.0.0")])]})]}),makeQuery(id+"F14.boolean.opBoolean","INTERSECT",EDGE,{"derivedFrom":[subQ2,makeQuery(id+"F14.opExtrude","SWEPT_FACE",FACE,{"disambiguationData":[OSD([sQuery(id+"F13.wireOp",EDGE,"E98.1.0.1")])]})]}),makeQuery(id+"F14.boolean.opBoolean","INTERSECT",EDGE,{"derivedFrom":[subQ2,makeQuery(id+"F14.opExtrude","SWEPT_FACE",FACE,{"disambiguationData":[OSD([sQuery(id+"F13.wireOp",EDGE,"E98.1.0.3")])]})]}),makeQuery(id+"F14.boolean.opBoolean","INTERSECT",EDGE,{"derivedFrom":[subQ2,makeQuery(id+"F14.opExtrude","SWEPT_FACE",FACE,{"disambiguationData":[OSD([sQuery(id+"F13.wireOp",EDGE,"E98.1.0.4")])]})]}),makeQuery(id+"F14.boolean.opBoolean","INTERSECT",EDGE,{"derivedFrom":[subQ2,makeQuery(id+"F14.opExtrude","SWEPT_FACE",FACE,{"disambiguationData":[OSD([sQuery(id+"F13.wireOp",EDGE,"E98.1.0.5")])]})]}),makeQuery(id+"F14.boolean.opBoolean","INTERSECT",EDGE,{"derivedFrom":[subQ2,makeQuery(id+"F14.opExtrude","SWEPT_FACE",FACE,{"disambiguationData":[OSD([sQuery(id+"F13.wireOp",EDGE,"E98.1.0.6")])]})]}),makeQuery(id+"F14.boolean.opBoolean","INTERSECT",EDGE,{"derivedFrom":[subQ2,makeQuery(id+"F14.opExtrude","SWEPT_FACE",FACE,{"disambiguationData":[OSD([sQuery(id+"F13.wireOp",EDGE,"E98.2.0.0")])]})]}),makeQuery(id+"F14.boolean.opBoolean","INTERSECT",EDGE,{"derivedFrom":[subQ2,makeQuery(id+"F14.opExtrude","SWEPT_FACE",FACE,{"disambiguationData":[OSD([sQuery(id+"F13.wireOp",EDGE,"E98.2.0.1")])]})]}),makeQuery(id+"F14.boolean.opBoolean","INTERSECT",EDGE,{"derivedFrom":[subQ2,makeQuery(id+"F14.opExtrude","SWEPT_FACE",FACE,{"disambiguationData":[OSD([sQuery(id+"F13.wireOp",EDGE,"E98.2.0.3")])]})]}),makeQuery(id+"F14.boolean.opBoolean","INTERSECT",EDGE,{"derivedFrom":[subQ2,makeQuery(id+"F14.opExtrude","SWEPT_FACE",FACE,{"disambiguationData":[OSD([sQuery(id+"F13.wireOp",EDGE,"E98.2.0.4")])]})]}),makeQuery(id+"F14.boolean.opBoolean","INTERSECT",EDGE,{"derivedFrom":[subQ2,makeQuery(id+"F14.opExtrude","SWEPT_FACE",FACE,{"disambiguationData":[OSD([sQuery(id+"F13.wireOp",EDGE,"E98.2.0.5")])]})]}),makeQuery(id+"F14.boolean.opBoolean","INTERSECT",EDGE,{"derivedFrom":[subQ2,makeQuery(id+"F14.opExtrude","SWEPT_FACE",FACE,{"disambiguationData":[OSD([sQuery(id+"F13.wireOp",EDGE,"E98.2.0.6")])]})]}),makeQuery(id+"F14.boolean.opBoolean","INTERSECT",EDGE,{"derivedFrom":[subQ2,makeQuery(id+"F14.opExtrude","SWEPT_FACE",FACE,{"disambiguationData":[OSD([sQuery(id+"F13.wireOp",EDGE,"E98.3.0.0")])]})]}),makeQuery(id+"F14.boolean.opBoolean","INTERSECT",EDGE,{"derivedFrom":[subQ2,makeQuery(id+"F14.opExtrude","SWEPT_FACE",FACE,{"disambiguationData":[OSD([sQuery(id+"F13.wireOp",EDGE,"E98.3.0.1")])]})]}),makeQuery(id+"F14.boolean.opBoolean","INTERSECT",EDGE,{"derivedFrom":[subQ2,makeQuery(id+"F14.opExtrude","SWEPT_FACE",FACE,{"disambiguationData":[OSD([sQuery(id+"F13.wireOp",EDGE,"E98.3.0.3")])]})]}),makeQuery(id+"F14.boolean.opBoolean","INTERSECT",EDGE,{"derivedFrom":[subQ2,makeQuery(id+"F14.opExtrude","SWEPT_FACE",FACE,{"disambiguationData":[OSD([sQuery(id+"F13.wireOp",EDGE,"E98.3.0.4")])]})]}),makeQuery(id+"F14.boolean.opBoolean","INTERSECT",EDGE,{"derivedFrom":[subQ2,makeQuery(id+"F14.opExtrude","SWEPT_FACE",FACE,{"disambiguationData":[OSD([sQuery(id+"F13.wireOp",EDGE,"E98.3.0.5")])]})]}),makeQuery(id+"F14.boolean.opBoolean","INTERSECT",EDGE,{"derivedFrom":[subQ2,makeQuery(id+"F14.opExtrude","SWEPT_FACE",FACE,{"disambiguationData":[OSD([sQuery(id+"F13.wireOp",EDGE,"E98.3.0.6")])]})]})]);}
            var Q40;
            {var subQ0=sQuery(id+"F0.wireOp",EDGE,"E61.top");var subQ2=makeQuery(id+"F4.boolean.opBoolean","MERGE",FACE,{"derivedFrom":[makeQuery(id+"F3.opExtrude","SWEPT_FACE",FACE,{"disambiguationData":[OSD([subQ0]),TDD([makeQuery(id+"F0.imprint","IMPRINT",EDGE,{"disambiguationData":[TD([[makeQuery(id+"F0.imprint","INTERSECT",VERTEX,{"derivedFrom":[subQ0,sQuery(id+"F0.wireOp",EDGE,"E77")]}),-1.0]])],"derivedFrom":subQ0}),makeQuery(id+"F0.imprint","IMPRINT",EDGE,{"disambiguationData":[TD([[makeQuery(id+"F0.imprint","INTERSECT",VERTEX,{"derivedFrom":[subQ0,sQuery(id+"F0.wireOp",EDGE,"E78")]}),1.0]])],"derivedFrom":subQ0})])]}),makeQuery(id+"F3.opExtrude","SWEPT_FACE",FACE,{"disambiguationData":[OSD([subQ0]),TDD([makeQuery(id+"F0.imprint","IMPRINT",EDGE,{"disambiguationData":[TD([[makeQuery(id+"F0.imprint","INTERSECT",VERTEX,{"derivedFrom":[subQ0,sQuery(id+"F0.wireOp",EDGE,"E62")]}),-1.0]])],"derivedFrom":subQ0})])]}),makeQuery(id+"F4.opExtrude","SWEPT_FACE",FACE,{"disambiguationData":[OSD([subQ0])]})]});Q40=qUnion([makeQuery(id+"F14.boolean.opBoolean","INTERSECT",EDGE,{"derivedFrom":[subQ2,makeQuery(id+"F14.opExtrude","SWEPT_FACE",FACE,{"disambiguationData":[OSD([sQuery(id+"F13.wireOp",EDGE,"E89")])]})]}),makeQuery(id+"F14.boolean.opBoolean","INTERSECT",EDGE,{"derivedFrom":[subQ2,makeQuery(id+"F14.opExtrude","SWEPT_FACE",FACE,{"disambiguationData":[OSD([sQuery(id+"F13.wireOp",EDGE,"E90")])]})]}),makeQuery(id+"F14.boolean.opBoolean","INTERSECT",EDGE,{"derivedFrom":[subQ2,makeQuery(id+"F14.opExtrude","SWEPT_FACE",FACE,{"disambiguationData":[OSD([sQuery(id+"F13.wireOp",EDGE,"E92")])]})]}),makeQuery(id+"F14.boolean.opBoolean","INTERSECT",EDGE,{"derivedFrom":[subQ2,makeQuery(id+"F14.opExtrude","SWEPT_FACE",FACE,{"disambiguationData":[OSD([sQuery(id+"F13.wireOp",EDGE,"E93")])]})]}),makeQuery(id+"F14.boolean.opBoolean","INTERSECT",EDGE,{"derivedFrom":[subQ2,makeQuery(id+"F14.opExtrude","SWEPT_FACE",FACE,{"disambiguationData":[OSD([sQuery(id+"F13.wireOp",EDGE,"E96")])]})]}),makeQuery(id+"F14.boolean.opBoolean","INTERSECT",EDGE,{"derivedFrom":[subQ2,makeQuery(id+"F14.opExtrude","SWEPT_FACE",FACE,{"disambiguationData":[OSD([sQuery(id+"F13.wireOp",EDGE,"E97")])]})]}),makeQuery(id+"F14.boolean.opBoolean","INTERSECT",EDGE,{"derivedFrom":[subQ2,makeQuery(id+"F14.opExtrude","SWEPT_FACE",FACE,{"disambiguationData":[OSD([sQuery(id+"F13.wireOp",EDGE,"E98.1.0.0")])]})]}),makeQuery(id+"F14.boolean.opBoolean","INTERSECT",EDGE,{"derivedFrom":[subQ2,makeQuery(id+"F14.opExtrude","SWEPT_FACE",FACE,{"disambiguationData":[OSD([sQuery(id+"F13.wireOp",EDGE,"E98.1.0.1")])]})]}),makeQuery(id+"F14.boolean.opBoolean","INTERSECT",EDGE,{"derivedFrom":[subQ2,makeQuery(id+"F14.opExtrude","SWEPT_FACE",FACE,{"disambiguationData":[OSD([sQuery(id+"F13.wireOp",EDGE,"E98.1.0.3")])]})]}),makeQuery(id+"F14.boolean.opBoolean","INTERSECT",EDGE,{"derivedFrom":[subQ2,makeQuery(id+"F14.opExtrude","SWEPT_FACE",FACE,{"disambiguationData":[OSD([sQuery(id+"F13.wireOp",EDGE,"E98.1.0.4")])]})]}),makeQuery(id+"F14.boolean.opBoolean","INTERSECT",EDGE,{"derivedFrom":[subQ2,makeQuery(id+"F14.opExtrude","SWEPT_FACE",FACE,{"disambiguationData":[OSD([sQuery(id+"F13.wireOp",EDGE,"E98.1.0.5")])]})]}),makeQuery(id+"F14.boolean.opBoolean","INTERSECT",EDGE,{"derivedFrom":[subQ2,makeQuery(id+"F14.opExtrude","SWEPT_FACE",FACE,{"disambiguationData":[OSD([sQuery(id+"F13.wireOp",EDGE,"E98.1.0.6")])]})]}),makeQuery(id+"F14.boolean.opBoolean","INTERSECT",EDGE,{"derivedFrom":[subQ2,makeQuery(id+"F14.opExtrude","SWEPT_FACE",FACE,{"disambiguationData":[OSD([sQuery(id+"F13.wireOp",EDGE,"E98.2.0.0")])]})]}),makeQuery(id+"F14.boolean.opBoolean","INTERSECT",EDGE,{"derivedFrom":[subQ2,makeQuery(id+"F14.opExtrude","SWEPT_FACE",FACE,{"disambiguationData":[OSD([sQuery(id+"F13.wireOp",EDGE,"E98.2.0.1")])]})]}),makeQuery(id+"F14.boolean.opBoolean","INTERSECT",EDGE,{"derivedFrom":[subQ2,makeQuery(id+"F14.opExtrude","SWEPT_FACE",FACE,{"disambiguationData":[OSD([sQuery(id+"F13.wireOp",EDGE,"E98.2.0.3")])]})]}),makeQuery(id+"F14.boolean.opBoolean","INTERSECT",EDGE,{"derivedFrom":[subQ2,makeQuery(id+"F14.opExtrude","SWEPT_FACE",FACE,{"disambiguationData":[OSD([sQuery(id+"F13.wireOp",EDGE,"E98.2.0.4")])]})]}),makeQuery(id+"F14.boolean.opBoolean","INTERSECT",EDGE,{"derivedFrom":[subQ2,makeQuery(id+"F14.opExtrude","SWEPT_FACE",FACE,{"disambiguationData":[OSD([sQuery(id+"F13.wireOp",EDGE,"E98.2.0.5")])]})]}),makeQuery(id+"F14.boolean.opBoolean","INTERSECT",EDGE,{"derivedFrom":[subQ2,makeQuery(id+"F14.opExtrude","SWEPT_FACE",FACE,{"disambiguationData":[OSD([sQuery(id+"F13.wireOp",EDGE,"E98.2.0.6")])]})]}),makeQuery(id+"F14.boolean.opBoolean","INTERSECT",EDGE,{"derivedFrom":[subQ2,makeQuery(id+"F14.opExtrude","SWEPT_FACE",FACE,{"disambiguationData":[OSD([sQuery(id+"F13.wireOp",EDGE,"E98.3.0.0")])]})]}),makeQuery(id+"F14.boolean.opBoolean","INTERSECT",EDGE,{"derivedFrom":[subQ2,makeQuery(id+"F14.opExtrude","SWEPT_FACE",FACE,{"disambiguationData":[OSD([sQuery(id+"F13.wireOp",EDGE,"E98.3.0.1")])]})]}),makeQuery(id+"F14.boolean.opBoolean","INTERSECT",EDGE,{"derivedFrom":[subQ2,makeQuery(id+"F14.opExtrude","SWEPT_FACE",FACE,{"disambiguationData":[OSD([sQuery(id+"F13.wireOp",EDGE,"E98.3.0.3")])]})]}),makeQuery(id+"F14.boolean.opBoolean","INTERSECT",EDGE,{"derivedFrom":[subQ2,makeQuery(id+"F14.opExtrude","SWEPT_FACE",FACE,{"disambiguationData":[OSD([sQuery(id+"F13.wireOp",EDGE,"E98.3.0.4")])]})]}),makeQuery(id+"F14.boolean.opBoolean","INTERSECT",EDGE,{"derivedFrom":[subQ2,makeQuery(id+"F14.opExtrude","SWEPT_FACE",FACE,{"disambiguationData":[OSD([sQuery(id+"F13.wireOp",EDGE,"E98.3.0.5")])]})]}),makeQuery(id+"F14.boolean.opBoolean","INTERSECT",EDGE,{"derivedFrom":[subQ2,makeQuery(id+"F14.opExtrude","SWEPT_FACE",FACE,{"disambiguationData":[OSD([sQuery(id+"F13.wireOp",EDGE,"E98.3.0.6")])]})]})]);}
            var Q41;
            {var subQ0=sQuery(id+"F0.wireOp",EDGE,"E61.top");var subQ2=makeQuery(id+"F4.boolean.opBoolean","MERGE",FACE,{"derivedFrom":[makeQuery(id+"F3.opExtrude","SWEPT_FACE",FACE,{"disambiguationData":[OSD([subQ0]),TDD([makeQuery(id+"F0.imprint","IMPRINT",EDGE,{"disambiguationData":[TD([[makeQuery(id+"F0.imprint","INTERSECT",VERTEX,{"derivedFrom":[subQ0,sQuery(id+"F0.wireOp",EDGE,"E77")]}),-1.0]])],"derivedFrom":subQ0}),makeQuery(id+"F0.imprint","IMPRINT",EDGE,{"disambiguationData":[TD([[makeQuery(id+"F0.imprint","INTERSECT",VERTEX,{"derivedFrom":[subQ0,sQuery(id+"F0.wireOp",EDGE,"E78")]}),1.0]])],"derivedFrom":subQ0})])]}),makeQuery(id+"F3.opExtrude","SWEPT_FACE",FACE,{"disambiguationData":[OSD([subQ0]),TDD([makeQuery(id+"F0.imprint","IMPRINT",EDGE,{"disambiguationData":[TD([[makeQuery(id+"F0.imprint","INTERSECT",VERTEX,{"derivedFrom":[subQ0,sQuery(id+"F0.wireOp",EDGE,"E62")]}),-1.0]])],"derivedFrom":subQ0})])]}),makeQuery(id+"F4.opExtrude","SWEPT_FACE",FACE,{"disambiguationData":[OSD([subQ0])]})]});Q41=qUnion([makeQuery(id+"F14.boolean.opBoolean","INTERSECT",EDGE,{"derivedFrom":[subQ2,makeQuery(id+"F14.opExtrude","SWEPT_FACE",FACE,{"disambiguationData":[OSD([sQuery(id+"F13.wireOp",EDGE,"E89")])]})]}),makeQuery(id+"F14.boolean.opBoolean","INTERSECT",EDGE,{"derivedFrom":[subQ2,makeQuery(id+"F14.opExtrude","SWEPT_FACE",FACE,{"disambiguationData":[OSD([sQuery(id+"F13.wireOp",EDGE,"E90")])]})]}),makeQuery(id+"F14.boolean.opBoolean","INTERSECT",EDGE,{"derivedFrom":[subQ2,makeQuery(id+"F14.opExtrude","SWEPT_FACE",FACE,{"disambiguationData":[OSD([sQuery(id+"F13.wireOp",EDGE,"E92")])]})]}),makeQuery(id+"F14.boolean.opBoolean","INTERSECT",EDGE,{"derivedFrom":[subQ2,makeQuery(id+"F14.opExtrude","SWEPT_FACE",FACE,{"disambiguationData":[OSD([sQuery(id+"F13.wireOp",EDGE,"E93")])]})]}),makeQuery(id+"F14.boolean.opBoolean","INTERSECT",EDGE,{"derivedFrom":[subQ2,makeQuery(id+"F14.opExtrude","SWEPT_FACE",FACE,{"disambiguationData":[OSD([sQuery(id+"F13.wireOp",EDGE,"E96")])]})]}),makeQuery(id+"F14.boolean.opBoolean","INTERSECT",EDGE,{"derivedFrom":[subQ2,makeQuery(id+"F14.opExtrude","SWEPT_FACE",FACE,{"disambiguationData":[OSD([sQuery(id+"F13.wireOp",EDGE,"E97")])]})]}),makeQuery(id+"F14.boolean.opBoolean","INTERSECT",EDGE,{"derivedFrom":[subQ2,makeQuery(id+"F14.opExtrude","SWEPT_FACE",FACE,{"disambiguationData":[OSD([sQuery(id+"F13.wireOp",EDGE,"E98.1.0.0")])]})]}),makeQuery(id+"F14.boolean.opBoolean","INTERSECT",EDGE,{"derivedFrom":[subQ2,makeQuery(id+"F14.opExtrude","SWEPT_FACE",FACE,{"disambiguationData":[OSD([sQuery(id+"F13.wireOp",EDGE,"E98.1.0.1")])]})]}),makeQuery(id+"F14.boolean.opBoolean","INTERSECT",EDGE,{"derivedFrom":[subQ2,makeQuery(id+"F14.opExtrude","SWEPT_FACE",FACE,{"disambiguationData":[OSD([sQuery(id+"F13.wireOp",EDGE,"E98.1.0.3")])]})]}),makeQuery(id+"F14.boolean.opBoolean","INTERSECT",EDGE,{"derivedFrom":[subQ2,makeQuery(id+"F14.opExtrude","SWEPT_FACE",FACE,{"disambiguationData":[OSD([sQuery(id+"F13.wireOp",EDGE,"E98.1.0.4")])]})]}),makeQuery(id+"F14.boolean.opBoolean","INTERSECT",EDGE,{"derivedFrom":[subQ2,makeQuery(id+"F14.opExtrude","SWEPT_FACE",FACE,{"disambiguationData":[OSD([sQuery(id+"F13.wireOp",EDGE,"E98.1.0.5")])]})]}),makeQuery(id+"F14.boolean.opBoolean","INTERSECT",EDGE,{"derivedFrom":[subQ2,makeQuery(id+"F14.opExtrude","SWEPT_FACE",FACE,{"disambiguationData":[OSD([sQuery(id+"F13.wireOp",EDGE,"E98.1.0.6")])]})]}),makeQuery(id+"F14.boolean.opBoolean","INTERSECT",EDGE,{"derivedFrom":[subQ2,makeQuery(id+"F14.opExtrude","SWEPT_FACE",FACE,{"disambiguationData":[OSD([sQuery(id+"F13.wireOp",EDGE,"E98.2.0.0")])]})]}),makeQuery(id+"F14.boolean.opBoolean","INTERSECT",EDGE,{"derivedFrom":[subQ2,makeQuery(id+"F14.opExtrude","SWEPT_FACE",FACE,{"disambiguationData":[OSD([sQuery(id+"F13.wireOp",EDGE,"E98.2.0.1")])]})]}),makeQuery(id+"F14.boolean.opBoolean","INTERSECT",EDGE,{"derivedFrom":[subQ2,makeQuery(id+"F14.opExtrude","SWEPT_FACE",FACE,{"disambiguationData":[OSD([sQuery(id+"F13.wireOp",EDGE,"E98.2.0.3")])]})]}),makeQuery(id+"F14.boolean.opBoolean","INTERSECT",EDGE,{"derivedFrom":[subQ2,makeQuery(id+"F14.opExtrude","SWEPT_FACE",FACE,{"disambiguationData":[OSD([sQuery(id+"F13.wireOp",EDGE,"E98.2.0.4")])]})]}),makeQuery(id+"F14.boolean.opBoolean","INTERSECT",EDGE,{"derivedFrom":[subQ2,makeQuery(id+"F14.opExtrude","SWEPT_FACE",FACE,{"disambiguationData":[OSD([sQuery(id+"F13.wireOp",EDGE,"E98.2.0.5")])]})]}),makeQuery(id+"F14.boolean.opBoolean","INTERSECT",EDGE,{"derivedFrom":[subQ2,makeQuery(id+"F14.opExtrude","SWEPT_FACE",FACE,{"disambiguationData":[OSD([sQuery(id+"F13.wireOp",EDGE,"E98.2.0.6")])]})]}),makeQuery(id+"F14.boolean.opBoolean","INTERSECT",EDGE,{"derivedFrom":[subQ2,makeQuery(id+"F14.opExtrude","SWEPT_FACE",FACE,{"disambiguationData":[OSD([sQuery(id+"F13.wireOp",EDGE,"E98.3.0.0")])]})]}),makeQuery(id+"F14.boolean.opBoolean","INTERSECT",EDGE,{"derivedFrom":[subQ2,makeQuery(id+"F14.opExtrude","SWEPT_FACE",FACE,{"disambiguationData":[OSD([sQuery(id+"F13.wireOp",EDGE,"E98.3.0.1")])]})]}),makeQuery(id+"F14.boolean.opBoolean","INTERSECT",EDGE,{"derivedFrom":[subQ2,makeQuery(id+"F14.opExtrude","SWEPT_FACE",FACE,{"disambiguationData":[OSD([sQuery(id+"F13.wireOp",EDGE,"E98.3.0.3")])]})]}),makeQuery(id+"F14.boolean.opBoolean","INTERSECT",EDGE,{"derivedFrom":[subQ2,makeQuery(id+"F14.opExtrude","SWEPT_FACE",FACE,{"disambiguationData":[OSD([sQuery(id+"F13.wireOp",EDGE,"E98.3.0.4")])]})]}),makeQuery(id+"F14.boolean.opBoolean","INTERSECT",EDGE,{"derivedFrom":[subQ2,makeQuery(id+"F14.opExtrude","SWEPT_FACE",FACE,{"disambiguationData":[OSD([sQuery(id+"F13.wireOp",EDGE,"E98.3.0.5")])]})]}),makeQuery(id+"F14.boolean.opBoolean","INTERSECT",EDGE,{"derivedFrom":[subQ2,makeQuery(id+"F14.opExtrude","SWEPT_FACE",FACE,{"disambiguationData":[OSD([sQuery(id+"F13.wireOp",EDGE,"E98.3.0.6")])]})]})]);}
            var Q42;
            {var subQ0=sQuery(id+"F0.wireOp",EDGE,"E61.top");var subQ2=makeQuery(id+"F4.boolean.opBoolean","MERGE",FACE,{"derivedFrom":[makeQuery(id+"F3.opExtrude","SWEPT_FACE",FACE,{"disambiguationData":[OSD([subQ0]),TDD([makeQuery(id+"F0.imprint","IMPRINT",EDGE,{"disambiguationData":[TD([[makeQuery(id+"F0.imprint","INTERSECT",VERTEX,{"derivedFrom":[subQ0,sQuery(id+"F0.wireOp",EDGE,"E77")]}),-1.0]])],"derivedFrom":subQ0}),makeQuery(id+"F0.imprint","IMPRINT",EDGE,{"disambiguationData":[TD([[makeQuery(id+"F0.imprint","INTERSECT",VERTEX,{"derivedFrom":[subQ0,sQuery(id+"F0.wireOp",EDGE,"E78")]}),1.0]])],"derivedFrom":subQ0})])]}),makeQuery(id+"F3.opExtrude","SWEPT_FACE",FACE,{"disambiguationData":[OSD([subQ0]),TDD([makeQuery(id+"F0.imprint","IMPRINT",EDGE,{"disambiguationData":[TD([[makeQuery(id+"F0.imprint","INTERSECT",VERTEX,{"derivedFrom":[subQ0,sQuery(id+"F0.wireOp",EDGE,"E62")]}),-1.0]])],"derivedFrom":subQ0})])]}),makeQuery(id+"F4.opExtrude","SWEPT_FACE",FACE,{"disambiguationData":[OSD([subQ0])]})]});Q42=qUnion([makeQuery(id+"F14.boolean.opBoolean","INTERSECT",EDGE,{"derivedFrom":[subQ2,makeQuery(id+"F14.opExtrude","SWEPT_FACE",FACE,{"disambiguationData":[OSD([sQuery(id+"F13.wireOp",EDGE,"E89")])]})]}),makeQuery(id+"F14.boolean.opBoolean","INTERSECT",EDGE,{"derivedFrom":[subQ2,makeQuery(id+"F14.opExtrude","SWEPT_FACE",FACE,{"disambiguationData":[OSD([sQuery(id+"F13.wireOp",EDGE,"E90")])]})]}),makeQuery(id+"F14.boolean.opBoolean","INTERSECT",EDGE,{"derivedFrom":[subQ2,makeQuery(id+"F14.opExtrude","SWEPT_FACE",FACE,{"disambiguationData":[OSD([sQuery(id+"F13.wireOp",EDGE,"E92")])]})]}),makeQuery(id+"F14.boolean.opBoolean","INTERSECT",EDGE,{"derivedFrom":[subQ2,makeQuery(id+"F14.opExtrude","SWEPT_FACE",FACE,{"disambiguationData":[OSD([sQuery(id+"F13.wireOp",EDGE,"E93")])]})]}),makeQuery(id+"F14.boolean.opBoolean","INTERSECT",EDGE,{"derivedFrom":[subQ2,makeQuery(id+"F14.opExtrude","SWEPT_FACE",FACE,{"disambiguationData":[OSD([sQuery(id+"F13.wireOp",EDGE,"E96")])]})]}),makeQuery(id+"F14.boolean.opBoolean","INTERSECT",EDGE,{"derivedFrom":[subQ2,makeQuery(id+"F14.opExtrude","SWEPT_FACE",FACE,{"disambiguationData":[OSD([sQuery(id+"F13.wireOp",EDGE,"E97")])]})]}),makeQuery(id+"F14.boolean.opBoolean","INTERSECT",EDGE,{"derivedFrom":[subQ2,makeQuery(id+"F14.opExtrude","SWEPT_FACE",FACE,{"disambiguationData":[OSD([sQuery(id+"F13.wireOp",EDGE,"E98.1.0.0")])]})]}),makeQuery(id+"F14.boolean.opBoolean","INTERSECT",EDGE,{"derivedFrom":[subQ2,makeQuery(id+"F14.opExtrude","SWEPT_FACE",FACE,{"disambiguationData":[OSD([sQuery(id+"F13.wireOp",EDGE,"E98.1.0.1")])]})]}),makeQuery(id+"F14.boolean.opBoolean","INTERSECT",EDGE,{"derivedFrom":[subQ2,makeQuery(id+"F14.opExtrude","SWEPT_FACE",FACE,{"disambiguationData":[OSD([sQuery(id+"F13.wireOp",EDGE,"E98.1.0.3")])]})]}),makeQuery(id+"F14.boolean.opBoolean","INTERSECT",EDGE,{"derivedFrom":[subQ2,makeQuery(id+"F14.opExtrude","SWEPT_FACE",FACE,{"disambiguationData":[OSD([sQuery(id+"F13.wireOp",EDGE,"E98.1.0.4")])]})]}),makeQuery(id+"F14.boolean.opBoolean","INTERSECT",EDGE,{"derivedFrom":[subQ2,makeQuery(id+"F14.opExtrude","SWEPT_FACE",FACE,{"disambiguationData":[OSD([sQuery(id+"F13.wireOp",EDGE,"E98.1.0.5")])]})]}),makeQuery(id+"F14.boolean.opBoolean","INTERSECT",EDGE,{"derivedFrom":[subQ2,makeQuery(id+"F14.opExtrude","SWEPT_FACE",FACE,{"disambiguationData":[OSD([sQuery(id+"F13.wireOp",EDGE,"E98.1.0.6")])]})]}),makeQuery(id+"F14.boolean.opBoolean","INTERSECT",EDGE,{"derivedFrom":[subQ2,makeQuery(id+"F14.opExtrude","SWEPT_FACE",FACE,{"disambiguationData":[OSD([sQuery(id+"F13.wireOp",EDGE,"E98.2.0.0")])]})]}),makeQuery(id+"F14.boolean.opBoolean","INTERSECT",EDGE,{"derivedFrom":[subQ2,makeQuery(id+"F14.opExtrude","SWEPT_FACE",FACE,{"disambiguationData":[OSD([sQuery(id+"F13.wireOp",EDGE,"E98.2.0.1")])]})]}),makeQuery(id+"F14.boolean.opBoolean","INTERSECT",EDGE,{"derivedFrom":[subQ2,makeQuery(id+"F14.opExtrude","SWEPT_FACE",FACE,{"disambiguationData":[OSD([sQuery(id+"F13.wireOp",EDGE,"E98.2.0.3")])]})]}),makeQuery(id+"F14.boolean.opBoolean","INTERSECT",EDGE,{"derivedFrom":[subQ2,makeQuery(id+"F14.opExtrude","SWEPT_FACE",FACE,{"disambiguationData":[OSD([sQuery(id+"F13.wireOp",EDGE,"E98.2.0.4")])]})]}),makeQuery(id+"F14.boolean.opBoolean","INTERSECT",EDGE,{"derivedFrom":[subQ2,makeQuery(id+"F14.opExtrude","SWEPT_FACE",FACE,{"disambiguationData":[OSD([sQuery(id+"F13.wireOp",EDGE,"E98.2.0.5")])]})]}),makeQuery(id+"F14.boolean.opBoolean","INTERSECT",EDGE,{"derivedFrom":[subQ2,makeQuery(id+"F14.opExtrude","SWEPT_FACE",FACE,{"disambiguationData":[OSD([sQuery(id+"F13.wireOp",EDGE,"E98.2.0.6")])]})]}),makeQuery(id+"F14.boolean.opBoolean","INTERSECT",EDGE,{"derivedFrom":[subQ2,makeQuery(id+"F14.opExtrude","SWEPT_FACE",FACE,{"disambiguationData":[OSD([sQuery(id+"F13.wireOp",EDGE,"E98.3.0.0")])]})]}),makeQuery(id+"F14.boolean.opBoolean","INTERSECT",EDGE,{"derivedFrom":[subQ2,makeQuery(id+"F14.opExtrude","SWEPT_FACE",FACE,{"disambiguationData":[OSD([sQuery(id+"F13.wireOp",EDGE,"E98.3.0.1")])]})]}),makeQuery(id+"F14.boolean.opBoolean","INTERSECT",EDGE,{"derivedFrom":[subQ2,makeQuery(id+"F14.opExtrude","SWEPT_FACE",FACE,{"disambiguationData":[OSD([sQuery(id+"F13.wireOp",EDGE,"E98.3.0.3")])]})]}),makeQuery(id+"F14.boolean.opBoolean","INTERSECT",EDGE,{"derivedFrom":[subQ2,makeQuery(id+"F14.opExtrude","SWEPT_FACE",FACE,{"disambiguationData":[OSD([sQuery(id+"F13.wireOp",EDGE,"E98.3.0.4")])]})]}),makeQuery(id+"F14.boolean.opBoolean","INTERSECT",EDGE,{"derivedFrom":[subQ2,makeQuery(id+"F14.opExtrude","SWEPT_FACE",FACE,{"disambiguationData":[OSD([sQuery(id+"F13.wireOp",EDGE,"E98.3.0.5")])]})]}),makeQuery(id+"F14.boolean.opBoolean","INTERSECT",EDGE,{"derivedFrom":[subQ2,makeQuery(id+"F14.opExtrude","SWEPT_FACE",FACE,{"disambiguationData":[OSD([sQuery(id+"F13.wireOp",EDGE,"E98.3.0.6")])]})]})]);}
            var Q43;
            {var subQ0=sQuery(id+"F0.wireOp",EDGE,"E61.top");var subQ2=makeQuery(id+"F4.boolean.opBoolean","MERGE",FACE,{"derivedFrom":[makeQuery(id+"F3.opExtrude","SWEPT_FACE",FACE,{"disambiguationData":[OSD([subQ0]),TDD([makeQuery(id+"F0.imprint","IMPRINT",EDGE,{"disambiguationData":[TD([[makeQuery(id+"F0.imprint","INTERSECT",VERTEX,{"derivedFrom":[subQ0,sQuery(id+"F0.wireOp",EDGE,"E77")]}),-1.0]])],"derivedFrom":subQ0}),makeQuery(id+"F0.imprint","IMPRINT",EDGE,{"disambiguationData":[TD([[makeQuery(id+"F0.imprint","INTERSECT",VERTEX,{"derivedFrom":[subQ0,sQuery(id+"F0.wireOp",EDGE,"E78")]}),1.0]])],"derivedFrom":subQ0})])]}),makeQuery(id+"F3.opExtrude","SWEPT_FACE",FACE,{"disambiguationData":[OSD([subQ0]),TDD([makeQuery(id+"F0.imprint","IMPRINT",EDGE,{"disambiguationData":[TD([[makeQuery(id+"F0.imprint","INTERSECT",VERTEX,{"derivedFrom":[subQ0,sQuery(id+"F0.wireOp",EDGE,"E62")]}),-1.0]])],"derivedFrom":subQ0})])]}),makeQuery(id+"F4.opExtrude","SWEPT_FACE",FACE,{"disambiguationData":[OSD([subQ0])]})]});Q43=qUnion([makeQuery(id+"F14.boolean.opBoolean","INTERSECT",EDGE,{"derivedFrom":[subQ2,makeQuery(id+"F14.opExtrude","SWEPT_FACE",FACE,{"disambiguationData":[OSD([sQuery(id+"F13.wireOp",EDGE,"E89")])]})]}),makeQuery(id+"F14.boolean.opBoolean","INTERSECT",EDGE,{"derivedFrom":[subQ2,makeQuery(id+"F14.opExtrude","SWEPT_FACE",FACE,{"disambiguationData":[OSD([sQuery(id+"F13.wireOp",EDGE,"E90")])]})]}),makeQuery(id+"F14.boolean.opBoolean","INTERSECT",EDGE,{"derivedFrom":[subQ2,makeQuery(id+"F14.opExtrude","SWEPT_FACE",FACE,{"disambiguationData":[OSD([sQuery(id+"F13.wireOp",EDGE,"E92")])]})]}),makeQuery(id+"F14.boolean.opBoolean","INTERSECT",EDGE,{"derivedFrom":[subQ2,makeQuery(id+"F14.opExtrude","SWEPT_FACE",FACE,{"disambiguationData":[OSD([sQuery(id+"F13.wireOp",EDGE,"E93")])]})]}),makeQuery(id+"F14.boolean.opBoolean","INTERSECT",EDGE,{"derivedFrom":[subQ2,makeQuery(id+"F14.opExtrude","SWEPT_FACE",FACE,{"disambiguationData":[OSD([sQuery(id+"F13.wireOp",EDGE,"E96")])]})]}),makeQuery(id+"F14.boolean.opBoolean","INTERSECT",EDGE,{"derivedFrom":[subQ2,makeQuery(id+"F14.opExtrude","SWEPT_FACE",FACE,{"disambiguationData":[OSD([sQuery(id+"F13.wireOp",EDGE,"E97")])]})]}),makeQuery(id+"F14.boolean.opBoolean","INTERSECT",EDGE,{"derivedFrom":[subQ2,makeQuery(id+"F14.opExtrude","SWEPT_FACE",FACE,{"disambiguationData":[OSD([sQuery(id+"F13.wireOp",EDGE,"E98.1.0.0")])]})]}),makeQuery(id+"F14.boolean.opBoolean","INTERSECT",EDGE,{"derivedFrom":[subQ2,makeQuery(id+"F14.opExtrude","SWEPT_FACE",FACE,{"disambiguationData":[OSD([sQuery(id+"F13.wireOp",EDGE,"E98.1.0.1")])]})]}),makeQuery(id+"F14.boolean.opBoolean","INTERSECT",EDGE,{"derivedFrom":[subQ2,makeQuery(id+"F14.opExtrude","SWEPT_FACE",FACE,{"disambiguationData":[OSD([sQuery(id+"F13.wireOp",EDGE,"E98.1.0.3")])]})]}),makeQuery(id+"F14.boolean.opBoolean","INTERSECT",EDGE,{"derivedFrom":[subQ2,makeQuery(id+"F14.opExtrude","SWEPT_FACE",FACE,{"disambiguationData":[OSD([sQuery(id+"F13.wireOp",EDGE,"E98.1.0.4")])]})]}),makeQuery(id+"F14.boolean.opBoolean","INTERSECT",EDGE,{"derivedFrom":[subQ2,makeQuery(id+"F14.opExtrude","SWEPT_FACE",FACE,{"disambiguationData":[OSD([sQuery(id+"F13.wireOp",EDGE,"E98.1.0.5")])]})]}),makeQuery(id+"F14.boolean.opBoolean","INTERSECT",EDGE,{"derivedFrom":[subQ2,makeQuery(id+"F14.opExtrude","SWEPT_FACE",FACE,{"disambiguationData":[OSD([sQuery(id+"F13.wireOp",EDGE,"E98.1.0.6")])]})]}),makeQuery(id+"F14.boolean.opBoolean","INTERSECT",EDGE,{"derivedFrom":[subQ2,makeQuery(id+"F14.opExtrude","SWEPT_FACE",FACE,{"disambiguationData":[OSD([sQuery(id+"F13.wireOp",EDGE,"E98.2.0.0")])]})]}),makeQuery(id+"F14.boolean.opBoolean","INTERSECT",EDGE,{"derivedFrom":[subQ2,makeQuery(id+"F14.opExtrude","SWEPT_FACE",FACE,{"disambiguationData":[OSD([sQuery(id+"F13.wireOp",EDGE,"E98.2.0.1")])]})]}),makeQuery(id+"F14.boolean.opBoolean","INTERSECT",EDGE,{"derivedFrom":[subQ2,makeQuery(id+"F14.opExtrude","SWEPT_FACE",FACE,{"disambiguationData":[OSD([sQuery(id+"F13.wireOp",EDGE,"E98.2.0.3")])]})]}),makeQuery(id+"F14.boolean.opBoolean","INTERSECT",EDGE,{"derivedFrom":[subQ2,makeQuery(id+"F14.opExtrude","SWEPT_FACE",FACE,{"disambiguationData":[OSD([sQuery(id+"F13.wireOp",EDGE,"E98.2.0.4")])]})]}),makeQuery(id+"F14.boolean.opBoolean","INTERSECT",EDGE,{"derivedFrom":[subQ2,makeQuery(id+"F14.opExtrude","SWEPT_FACE",FACE,{"disambiguationData":[OSD([sQuery(id+"F13.wireOp",EDGE,"E98.2.0.5")])]})]}),makeQuery(id+"F14.boolean.opBoolean","INTERSECT",EDGE,{"derivedFrom":[subQ2,makeQuery(id+"F14.opExtrude","SWEPT_FACE",FACE,{"disambiguationData":[OSD([sQuery(id+"F13.wireOp",EDGE,"E98.2.0.6")])]})]}),makeQuery(id+"F14.boolean.opBoolean","INTERSECT",EDGE,{"derivedFrom":[subQ2,makeQuery(id+"F14.opExtrude","SWEPT_FACE",FACE,{"disambiguationData":[OSD([sQuery(id+"F13.wireOp",EDGE,"E98.3.0.0")])]})]}),makeQuery(id+"F14.boolean.opBoolean","INTERSECT",EDGE,{"derivedFrom":[subQ2,makeQuery(id+"F14.opExtrude","SWEPT_FACE",FACE,{"disambiguationData":[OSD([sQuery(id+"F13.wireOp",EDGE,"E98.3.0.1")])]})]}),makeQuery(id+"F14.boolean.opBoolean","INTERSECT",EDGE,{"derivedFrom":[subQ2,makeQuery(id+"F14.opExtrude","SWEPT_FACE",FACE,{"disambiguationData":[OSD([sQuery(id+"F13.wireOp",EDGE,"E98.3.0.3")])]})]}),makeQuery(id+"F14.boolean.opBoolean","INTERSECT",EDGE,{"derivedFrom":[subQ2,makeQuery(id+"F14.opExtrude","SWEPT_FACE",FACE,{"disambiguationData":[OSD([sQuery(id+"F13.wireOp",EDGE,"E98.3.0.4")])]})]}),makeQuery(id+"F14.boolean.opBoolean","INTERSECT",EDGE,{"derivedFrom":[subQ2,makeQuery(id+"F14.opExtrude","SWEPT_FACE",FACE,{"disambiguationData":[OSD([sQuery(id+"F13.wireOp",EDGE,"E98.3.0.5")])]})]}),makeQuery(id+"F14.boolean.opBoolean","INTERSECT",EDGE,{"derivedFrom":[subQ2,makeQuery(id+"F14.opExtrude","SWEPT_FACE",FACE,{"disambiguationData":[OSD([sQuery(id+"F13.wireOp",EDGE,"E98.3.0.6")])]})]})]);}
            var Q44;
            {var subQ0=sQuery(id+"F0.wireOp",EDGE,"E61.top");var subQ2=makeQuery(id+"F4.boolean.opBoolean","MERGE",FACE,{"derivedFrom":[makeQuery(id+"F3.opExtrude","SWEPT_FACE",FACE,{"disambiguationData":[OSD([subQ0]),TDD([makeQuery(id+"F0.imprint","IMPRINT",EDGE,{"disambiguationData":[TD([[makeQuery(id+"F0.imprint","INTERSECT",VERTEX,{"derivedFrom":[subQ0,sQuery(id+"F0.wireOp",EDGE,"E77")]}),-1.0]])],"derivedFrom":subQ0}),makeQuery(id+"F0.imprint","IMPRINT",EDGE,{"disambiguationData":[TD([[makeQuery(id+"F0.imprint","INTERSECT",VERTEX,{"derivedFrom":[subQ0,sQuery(id+"F0.wireOp",EDGE,"E78")]}),1.0]])],"derivedFrom":subQ0})])]}),makeQuery(id+"F3.opExtrude","SWEPT_FACE",FACE,{"disambiguationData":[OSD([subQ0]),TDD([makeQuery(id+"F0.imprint","IMPRINT",EDGE,{"disambiguationData":[TD([[makeQuery(id+"F0.imprint","INTERSECT",VERTEX,{"derivedFrom":[subQ0,sQuery(id+"F0.wireOp",EDGE,"E62")]}),-1.0]])],"derivedFrom":subQ0})])]}),makeQuery(id+"F4.opExtrude","SWEPT_FACE",FACE,{"disambiguationData":[OSD([subQ0])]})]});Q44=qUnion([makeQuery(id+"F14.boolean.opBoolean","INTERSECT",EDGE,{"derivedFrom":[subQ2,makeQuery(id+"F14.opExtrude","SWEPT_FACE",FACE,{"disambiguationData":[OSD([sQuery(id+"F13.wireOp",EDGE,"E89")])]})]}),makeQuery(id+"F14.boolean.opBoolean","INTERSECT",EDGE,{"derivedFrom":[subQ2,makeQuery(id+"F14.opExtrude","SWEPT_FACE",FACE,{"disambiguationData":[OSD([sQuery(id+"F13.wireOp",EDGE,"E90")])]})]}),makeQuery(id+"F14.boolean.opBoolean","INTERSECT",EDGE,{"derivedFrom":[subQ2,makeQuery(id+"F14.opExtrude","SWEPT_FACE",FACE,{"disambiguationData":[OSD([sQuery(id+"F13.wireOp",EDGE,"E92")])]})]}),makeQuery(id+"F14.boolean.opBoolean","INTERSECT",EDGE,{"derivedFrom":[subQ2,makeQuery(id+"F14.opExtrude","SWEPT_FACE",FACE,{"disambiguationData":[OSD([sQuery(id+"F13.wireOp",EDGE,"E93")])]})]}),makeQuery(id+"F14.boolean.opBoolean","INTERSECT",EDGE,{"derivedFrom":[subQ2,makeQuery(id+"F14.opExtrude","SWEPT_FACE",FACE,{"disambiguationData":[OSD([sQuery(id+"F13.wireOp",EDGE,"E96")])]})]}),makeQuery(id+"F14.boolean.opBoolean","INTERSECT",EDGE,{"derivedFrom":[subQ2,makeQuery(id+"F14.opExtrude","SWEPT_FACE",FACE,{"disambiguationData":[OSD([sQuery(id+"F13.wireOp",EDGE,"E97")])]})]}),makeQuery(id+"F14.boolean.opBoolean","INTERSECT",EDGE,{"derivedFrom":[subQ2,makeQuery(id+"F14.opExtrude","SWEPT_FACE",FACE,{"disambiguationData":[OSD([sQuery(id+"F13.wireOp",EDGE,"E98.1.0.0")])]})]}),makeQuery(id+"F14.boolean.opBoolean","INTERSECT",EDGE,{"derivedFrom":[subQ2,makeQuery(id+"F14.opExtrude","SWEPT_FACE",FACE,{"disambiguationData":[OSD([sQuery(id+"F13.wireOp",EDGE,"E98.1.0.1")])]})]}),makeQuery(id+"F14.boolean.opBoolean","INTERSECT",EDGE,{"derivedFrom":[subQ2,makeQuery(id+"F14.opExtrude","SWEPT_FACE",FACE,{"disambiguationData":[OSD([sQuery(id+"F13.wireOp",EDGE,"E98.1.0.3")])]})]}),makeQuery(id+"F14.boolean.opBoolean","INTERSECT",EDGE,{"derivedFrom":[subQ2,makeQuery(id+"F14.opExtrude","SWEPT_FACE",FACE,{"disambiguationData":[OSD([sQuery(id+"F13.wireOp",EDGE,"E98.1.0.4")])]})]}),makeQuery(id+"F14.boolean.opBoolean","INTERSECT",EDGE,{"derivedFrom":[subQ2,makeQuery(id+"F14.opExtrude","SWEPT_FACE",FACE,{"disambiguationData":[OSD([sQuery(id+"F13.wireOp",EDGE,"E98.1.0.5")])]})]}),makeQuery(id+"F14.boolean.opBoolean","INTERSECT",EDGE,{"derivedFrom":[subQ2,makeQuery(id+"F14.opExtrude","SWEPT_FACE",FACE,{"disambiguationData":[OSD([sQuery(id+"F13.wireOp",EDGE,"E98.1.0.6")])]})]}),makeQuery(id+"F14.boolean.opBoolean","INTERSECT",EDGE,{"derivedFrom":[subQ2,makeQuery(id+"F14.opExtrude","SWEPT_FACE",FACE,{"disambiguationData":[OSD([sQuery(id+"F13.wireOp",EDGE,"E98.2.0.0")])]})]}),makeQuery(id+"F14.boolean.opBoolean","INTERSECT",EDGE,{"derivedFrom":[subQ2,makeQuery(id+"F14.opExtrude","SWEPT_FACE",FACE,{"disambiguationData":[OSD([sQuery(id+"F13.wireOp",EDGE,"E98.2.0.1")])]})]}),makeQuery(id+"F14.boolean.opBoolean","INTERSECT",EDGE,{"derivedFrom":[subQ2,makeQuery(id+"F14.opExtrude","SWEPT_FACE",FACE,{"disambiguationData":[OSD([sQuery(id+"F13.wireOp",EDGE,"E98.2.0.3")])]})]}),makeQuery(id+"F14.boolean.opBoolean","INTERSECT",EDGE,{"derivedFrom":[subQ2,makeQuery(id+"F14.opExtrude","SWEPT_FACE",FACE,{"disambiguationData":[OSD([sQuery(id+"F13.wireOp",EDGE,"E98.2.0.4")])]})]}),makeQuery(id+"F14.boolean.opBoolean","INTERSECT",EDGE,{"derivedFrom":[subQ2,makeQuery(id+"F14.opExtrude","SWEPT_FACE",FACE,{"disambiguationData":[OSD([sQuery(id+"F13.wireOp",EDGE,"E98.2.0.5")])]})]}),makeQuery(id+"F14.boolean.opBoolean","INTERSECT",EDGE,{"derivedFrom":[subQ2,makeQuery(id+"F14.opExtrude","SWEPT_FACE",FACE,{"disambiguationData":[OSD([sQuery(id+"F13.wireOp",EDGE,"E98.2.0.6")])]})]}),makeQuery(id+"F14.boolean.opBoolean","INTERSECT",EDGE,{"derivedFrom":[subQ2,makeQuery(id+"F14.opExtrude","SWEPT_FACE",FACE,{"disambiguationData":[OSD([sQuery(id+"F13.wireOp",EDGE,"E98.3.0.0")])]})]}),makeQuery(id+"F14.boolean.opBoolean","INTERSECT",EDGE,{"derivedFrom":[subQ2,makeQuery(id+"F14.opExtrude","SWEPT_FACE",FACE,{"disambiguationData":[OSD([sQuery(id+"F13.wireOp",EDGE,"E98.3.0.1")])]})]}),makeQuery(id+"F14.boolean.opBoolean","INTERSECT",EDGE,{"derivedFrom":[subQ2,makeQuery(id+"F14.opExtrude","SWEPT_FACE",FACE,{"disambiguationData":[OSD([sQuery(id+"F13.wireOp",EDGE,"E98.3.0.3")])]})]}),makeQuery(id+"F14.boolean.opBoolean","INTERSECT",EDGE,{"derivedFrom":[subQ2,makeQuery(id+"F14.opExtrude","SWEPT_FACE",FACE,{"disambiguationData":[OSD([sQuery(id+"F13.wireOp",EDGE,"E98.3.0.4")])]})]}),makeQuery(id+"F14.boolean.opBoolean","INTERSECT",EDGE,{"derivedFrom":[subQ2,makeQuery(id+"F14.opExtrude","SWEPT_FACE",FACE,{"disambiguationData":[OSD([sQuery(id+"F13.wireOp",EDGE,"E98.3.0.5")])]})]}),makeQuery(id+"F14.boolean.opBoolean","INTERSECT",EDGE,{"derivedFrom":[subQ2,makeQuery(id+"F14.opExtrude","SWEPT_FACE",FACE,{"disambiguationData":[OSD([sQuery(id+"F13.wireOp",EDGE,"E98.3.0.6")])]})]})]);}
            var Q45;
            {var subQ0=sQuery(id+"F0.wireOp",EDGE,"E61.top");var subQ2=makeQuery(id+"F4.boolean.opBoolean","MERGE",FACE,{"derivedFrom":[makeQuery(id+"F3.opExtrude","SWEPT_FACE",FACE,{"disambiguationData":[OSD([subQ0]),TDD([makeQuery(id+"F0.imprint","IMPRINT",EDGE,{"disambiguationData":[TD([[makeQuery(id+"F0.imprint","INTERSECT",VERTEX,{"derivedFrom":[subQ0,sQuery(id+"F0.wireOp",EDGE,"E77")]}),-1.0]])],"derivedFrom":subQ0}),makeQuery(id+"F0.imprint","IMPRINT",EDGE,{"disambiguationData":[TD([[makeQuery(id+"F0.imprint","INTERSECT",VERTEX,{"derivedFrom":[subQ0,sQuery(id+"F0.wireOp",EDGE,"E78")]}),1.0]])],"derivedFrom":subQ0})])]}),makeQuery(id+"F3.opExtrude","SWEPT_FACE",FACE,{"disambiguationData":[OSD([subQ0]),TDD([makeQuery(id+"F0.imprint","IMPRINT",EDGE,{"disambiguationData":[TD([[makeQuery(id+"F0.imprint","INTERSECT",VERTEX,{"derivedFrom":[subQ0,sQuery(id+"F0.wireOp",EDGE,"E62")]}),-1.0]])],"derivedFrom":subQ0})])]}),makeQuery(id+"F4.opExtrude","SWEPT_FACE",FACE,{"disambiguationData":[OSD([subQ0])]})]});Q45=qUnion([makeQuery(id+"F14.boolean.opBoolean","INTERSECT",EDGE,{"derivedFrom":[subQ2,makeQuery(id+"F14.opExtrude","SWEPT_FACE",FACE,{"disambiguationData":[OSD([sQuery(id+"F13.wireOp",EDGE,"E89")])]})]}),makeQuery(id+"F14.boolean.opBoolean","INTERSECT",EDGE,{"derivedFrom":[subQ2,makeQuery(id+"F14.opExtrude","SWEPT_FACE",FACE,{"disambiguationData":[OSD([sQuery(id+"F13.wireOp",EDGE,"E90")])]})]}),makeQuery(id+"F14.boolean.opBoolean","INTERSECT",EDGE,{"derivedFrom":[subQ2,makeQuery(id+"F14.opExtrude","SWEPT_FACE",FACE,{"disambiguationData":[OSD([sQuery(id+"F13.wireOp",EDGE,"E92")])]})]}),makeQuery(id+"F14.boolean.opBoolean","INTERSECT",EDGE,{"derivedFrom":[subQ2,makeQuery(id+"F14.opExtrude","SWEPT_FACE",FACE,{"disambiguationData":[OSD([sQuery(id+"F13.wireOp",EDGE,"E93")])]})]}),makeQuery(id+"F14.boolean.opBoolean","INTERSECT",EDGE,{"derivedFrom":[subQ2,makeQuery(id+"F14.opExtrude","SWEPT_FACE",FACE,{"disambiguationData":[OSD([sQuery(id+"F13.wireOp",EDGE,"E96")])]})]}),makeQuery(id+"F14.boolean.opBoolean","INTERSECT",EDGE,{"derivedFrom":[subQ2,makeQuery(id+"F14.opExtrude","SWEPT_FACE",FACE,{"disambiguationData":[OSD([sQuery(id+"F13.wireOp",EDGE,"E97")])]})]}),makeQuery(id+"F14.boolean.opBoolean","INTERSECT",EDGE,{"derivedFrom":[subQ2,makeQuery(id+"F14.opExtrude","SWEPT_FACE",FACE,{"disambiguationData":[OSD([sQuery(id+"F13.wireOp",EDGE,"E98.1.0.0")])]})]}),makeQuery(id+"F14.boolean.opBoolean","INTERSECT",EDGE,{"derivedFrom":[subQ2,makeQuery(id+"F14.opExtrude","SWEPT_FACE",FACE,{"disambiguationData":[OSD([sQuery(id+"F13.wireOp",EDGE,"E98.1.0.1")])]})]}),makeQuery(id+"F14.boolean.opBoolean","INTERSECT",EDGE,{"derivedFrom":[subQ2,makeQuery(id+"F14.opExtrude","SWEPT_FACE",FACE,{"disambiguationData":[OSD([sQuery(id+"F13.wireOp",EDGE,"E98.1.0.3")])]})]}),makeQuery(id+"F14.boolean.opBoolean","INTERSECT",EDGE,{"derivedFrom":[subQ2,makeQuery(id+"F14.opExtrude","SWEPT_FACE",FACE,{"disambiguationData":[OSD([sQuery(id+"F13.wireOp",EDGE,"E98.1.0.4")])]})]}),makeQuery(id+"F14.boolean.opBoolean","INTERSECT",EDGE,{"derivedFrom":[subQ2,makeQuery(id+"F14.opExtrude","SWEPT_FACE",FACE,{"disambiguationData":[OSD([sQuery(id+"F13.wireOp",EDGE,"E98.1.0.5")])]})]}),makeQuery(id+"F14.boolean.opBoolean","INTERSECT",EDGE,{"derivedFrom":[subQ2,makeQuery(id+"F14.opExtrude","SWEPT_FACE",FACE,{"disambiguationData":[OSD([sQuery(id+"F13.wireOp",EDGE,"E98.1.0.6")])]})]}),makeQuery(id+"F14.boolean.opBoolean","INTERSECT",EDGE,{"derivedFrom":[subQ2,makeQuery(id+"F14.opExtrude","SWEPT_FACE",FACE,{"disambiguationData":[OSD([sQuery(id+"F13.wireOp",EDGE,"E98.2.0.0")])]})]}),makeQuery(id+"F14.boolean.opBoolean","INTERSECT",EDGE,{"derivedFrom":[subQ2,makeQuery(id+"F14.opExtrude","SWEPT_FACE",FACE,{"disambiguationData":[OSD([sQuery(id+"F13.wireOp",EDGE,"E98.2.0.1")])]})]}),makeQuery(id+"F14.boolean.opBoolean","INTERSECT",EDGE,{"derivedFrom":[subQ2,makeQuery(id+"F14.opExtrude","SWEPT_FACE",FACE,{"disambiguationData":[OSD([sQuery(id+"F13.wireOp",EDGE,"E98.2.0.3")])]})]}),makeQuery(id+"F14.boolean.opBoolean","INTERSECT",EDGE,{"derivedFrom":[subQ2,makeQuery(id+"F14.opExtrude","SWEPT_FACE",FACE,{"disambiguationData":[OSD([sQuery(id+"F13.wireOp",EDGE,"E98.2.0.4")])]})]}),makeQuery(id+"F14.boolean.opBoolean","INTERSECT",EDGE,{"derivedFrom":[subQ2,makeQuery(id+"F14.opExtrude","SWEPT_FACE",FACE,{"disambiguationData":[OSD([sQuery(id+"F13.wireOp",EDGE,"E98.2.0.5")])]})]}),makeQuery(id+"F14.boolean.opBoolean","INTERSECT",EDGE,{"derivedFrom":[subQ2,makeQuery(id+"F14.opExtrude","SWEPT_FACE",FACE,{"disambiguationData":[OSD([sQuery(id+"F13.wireOp",EDGE,"E98.2.0.6")])]})]}),makeQuery(id+"F14.boolean.opBoolean","INTERSECT",EDGE,{"derivedFrom":[subQ2,makeQuery(id+"F14.opExtrude","SWEPT_FACE",FACE,{"disambiguationData":[OSD([sQuery(id+"F13.wireOp",EDGE,"E98.3.0.0")])]})]}),makeQuery(id+"F14.boolean.opBoolean","INTERSECT",EDGE,{"derivedFrom":[subQ2,makeQuery(id+"F14.opExtrude","SWEPT_FACE",FACE,{"disambiguationData":[OSD([sQuery(id+"F13.wireOp",EDGE,"E98.3.0.1")])]})]}),makeQuery(id+"F14.boolean.opBoolean","INTERSECT",EDGE,{"derivedFrom":[subQ2,makeQuery(id+"F14.opExtrude","SWEPT_FACE",FACE,{"disambiguationData":[OSD([sQuery(id+"F13.wireOp",EDGE,"E98.3.0.3")])]})]}),makeQuery(id+"F14.boolean.opBoolean","INTERSECT",EDGE,{"derivedFrom":[subQ2,makeQuery(id+"F14.opExtrude","SWEPT_FACE",FACE,{"disambiguationData":[OSD([sQuery(id+"F13.wireOp",EDGE,"E98.3.0.4")])]})]}),makeQuery(id+"F14.boolean.opBoolean","INTERSECT",EDGE,{"derivedFrom":[subQ2,makeQuery(id+"F14.opExtrude","SWEPT_FACE",FACE,{"disambiguationData":[OSD([sQuery(id+"F13.wireOp",EDGE,"E98.3.0.5")])]})]}),makeQuery(id+"F14.boolean.opBoolean","INTERSECT",EDGE,{"derivedFrom":[subQ2,makeQuery(id+"F14.opExtrude","SWEPT_FACE",FACE,{"disambiguationData":[OSD([sQuery(id+"F13.wireOp",EDGE,"E98.3.0.6")])]})]})]);}
            var Q46;
            {var subQ0=sQuery(id+"F0.wireOp",EDGE,"E61.top");var subQ2=makeQuery(id+"F4.boolean.opBoolean","MERGE",FACE,{"derivedFrom":[makeQuery(id+"F3.opExtrude","SWEPT_FACE",FACE,{"disambiguationData":[OSD([subQ0]),TDD([makeQuery(id+"F0.imprint","IMPRINT",EDGE,{"disambiguationData":[TD([[makeQuery(id+"F0.imprint","INTERSECT",VERTEX,{"derivedFrom":[subQ0,sQuery(id+"F0.wireOp",EDGE,"E77")]}),-1.0]])],"derivedFrom":subQ0}),makeQuery(id+"F0.imprint","IMPRINT",EDGE,{"disambiguationData":[TD([[makeQuery(id+"F0.imprint","INTERSECT",VERTEX,{"derivedFrom":[subQ0,sQuery(id+"F0.wireOp",EDGE,"E78")]}),1.0]])],"derivedFrom":subQ0})])]}),makeQuery(id+"F3.opExtrude","SWEPT_FACE",FACE,{"disambiguationData":[OSD([subQ0]),TDD([makeQuery(id+"F0.imprint","IMPRINT",EDGE,{"disambiguationData":[TD([[makeQuery(id+"F0.imprint","INTERSECT",VERTEX,{"derivedFrom":[subQ0,sQuery(id+"F0.wireOp",EDGE,"E62")]}),-1.0]])],"derivedFrom":subQ0})])]}),makeQuery(id+"F4.opExtrude","SWEPT_FACE",FACE,{"disambiguationData":[OSD([subQ0])]})]});Q46=qUnion([makeQuery(id+"F14.boolean.opBoolean","INTERSECT",EDGE,{"derivedFrom":[subQ2,makeQuery(id+"F14.opExtrude","SWEPT_FACE",FACE,{"disambiguationData":[OSD([sQuery(id+"F13.wireOp",EDGE,"E89")])]})]}),makeQuery(id+"F14.boolean.opBoolean","INTERSECT",EDGE,{"derivedFrom":[subQ2,makeQuery(id+"F14.opExtrude","SWEPT_FACE",FACE,{"disambiguationData":[OSD([sQuery(id+"F13.wireOp",EDGE,"E90")])]})]}),makeQuery(id+"F14.boolean.opBoolean","INTERSECT",EDGE,{"derivedFrom":[subQ2,makeQuery(id+"F14.opExtrude","SWEPT_FACE",FACE,{"disambiguationData":[OSD([sQuery(id+"F13.wireOp",EDGE,"E92")])]})]}),makeQuery(id+"F14.boolean.opBoolean","INTERSECT",EDGE,{"derivedFrom":[subQ2,makeQuery(id+"F14.opExtrude","SWEPT_FACE",FACE,{"disambiguationData":[OSD([sQuery(id+"F13.wireOp",EDGE,"E93")])]})]}),makeQuery(id+"F14.boolean.opBoolean","INTERSECT",EDGE,{"derivedFrom":[subQ2,makeQuery(id+"F14.opExtrude","SWEPT_FACE",FACE,{"disambiguationData":[OSD([sQuery(id+"F13.wireOp",EDGE,"E96")])]})]}),makeQuery(id+"F14.boolean.opBoolean","INTERSECT",EDGE,{"derivedFrom":[subQ2,makeQuery(id+"F14.opExtrude","SWEPT_FACE",FACE,{"disambiguationData":[OSD([sQuery(id+"F13.wireOp",EDGE,"E97")])]})]}),makeQuery(id+"F14.boolean.opBoolean","INTERSECT",EDGE,{"derivedFrom":[subQ2,makeQuery(id+"F14.opExtrude","SWEPT_FACE",FACE,{"disambiguationData":[OSD([sQuery(id+"F13.wireOp",EDGE,"E98.1.0.0")])]})]}),makeQuery(id+"F14.boolean.opBoolean","INTERSECT",EDGE,{"derivedFrom":[subQ2,makeQuery(id+"F14.opExtrude","SWEPT_FACE",FACE,{"disambiguationData":[OSD([sQuery(id+"F13.wireOp",EDGE,"E98.1.0.1")])]})]}),makeQuery(id+"F14.boolean.opBoolean","INTERSECT",EDGE,{"derivedFrom":[subQ2,makeQuery(id+"F14.opExtrude","SWEPT_FACE",FACE,{"disambiguationData":[OSD([sQuery(id+"F13.wireOp",EDGE,"E98.1.0.3")])]})]}),makeQuery(id+"F14.boolean.opBoolean","INTERSECT",EDGE,{"derivedFrom":[subQ2,makeQuery(id+"F14.opExtrude","SWEPT_FACE",FACE,{"disambiguationData":[OSD([sQuery(id+"F13.wireOp",EDGE,"E98.1.0.4")])]})]}),makeQuery(id+"F14.boolean.opBoolean","INTERSECT",EDGE,{"derivedFrom":[subQ2,makeQuery(id+"F14.opExtrude","SWEPT_FACE",FACE,{"disambiguationData":[OSD([sQuery(id+"F13.wireOp",EDGE,"E98.1.0.5")])]})]}),makeQuery(id+"F14.boolean.opBoolean","INTERSECT",EDGE,{"derivedFrom":[subQ2,makeQuery(id+"F14.opExtrude","SWEPT_FACE",FACE,{"disambiguationData":[OSD([sQuery(id+"F13.wireOp",EDGE,"E98.1.0.6")])]})]}),makeQuery(id+"F14.boolean.opBoolean","INTERSECT",EDGE,{"derivedFrom":[subQ2,makeQuery(id+"F14.opExtrude","SWEPT_FACE",FACE,{"disambiguationData":[OSD([sQuery(id+"F13.wireOp",EDGE,"E98.2.0.0")])]})]}),makeQuery(id+"F14.boolean.opBoolean","INTERSECT",EDGE,{"derivedFrom":[subQ2,makeQuery(id+"F14.opExtrude","SWEPT_FACE",FACE,{"disambiguationData":[OSD([sQuery(id+"F13.wireOp",EDGE,"E98.2.0.1")])]})]}),makeQuery(id+"F14.boolean.opBoolean","INTERSECT",EDGE,{"derivedFrom":[subQ2,makeQuery(id+"F14.opExtrude","SWEPT_FACE",FACE,{"disambiguationData":[OSD([sQuery(id+"F13.wireOp",EDGE,"E98.2.0.3")])]})]}),makeQuery(id+"F14.boolean.opBoolean","INTERSECT",EDGE,{"derivedFrom":[subQ2,makeQuery(id+"F14.opExtrude","SWEPT_FACE",FACE,{"disambiguationData":[OSD([sQuery(id+"F13.wireOp",EDGE,"E98.2.0.4")])]})]}),makeQuery(id+"F14.boolean.opBoolean","INTERSECT",EDGE,{"derivedFrom":[subQ2,makeQuery(id+"F14.opExtrude","SWEPT_FACE",FACE,{"disambiguationData":[OSD([sQuery(id+"F13.wireOp",EDGE,"E98.2.0.5")])]})]}),makeQuery(id+"F14.boolean.opBoolean","INTERSECT",EDGE,{"derivedFrom":[subQ2,makeQuery(id+"F14.opExtrude","SWEPT_FACE",FACE,{"disambiguationData":[OSD([sQuery(id+"F13.wireOp",EDGE,"E98.2.0.6")])]})]}),makeQuery(id+"F14.boolean.opBoolean","INTERSECT",EDGE,{"derivedFrom":[subQ2,makeQuery(id+"F14.opExtrude","SWEPT_FACE",FACE,{"disambiguationData":[OSD([sQuery(id+"F13.wireOp",EDGE,"E98.3.0.0")])]})]}),makeQuery(id+"F14.boolean.opBoolean","INTERSECT",EDGE,{"derivedFrom":[subQ2,makeQuery(id+"F14.opExtrude","SWEPT_FACE",FACE,{"disambiguationData":[OSD([sQuery(id+"F13.wireOp",EDGE,"E98.3.0.1")])]})]}),makeQuery(id+"F14.boolean.opBoolean","INTERSECT",EDGE,{"derivedFrom":[subQ2,makeQuery(id+"F14.opExtrude","SWEPT_FACE",FACE,{"disambiguationData":[OSD([sQuery(id+"F13.wireOp",EDGE,"E98.3.0.3")])]})]}),makeQuery(id+"F14.boolean.opBoolean","INTERSECT",EDGE,{"derivedFrom":[subQ2,makeQuery(id+"F14.opExtrude","SWEPT_FACE",FACE,{"disambiguationData":[OSD([sQuery(id+"F13.wireOp",EDGE,"E98.3.0.4")])]})]}),makeQuery(id+"F14.boolean.opBoolean","INTERSECT",EDGE,{"derivedFrom":[subQ2,makeQuery(id+"F14.opExtrude","SWEPT_FACE",FACE,{"disambiguationData":[OSD([sQuery(id+"F13.wireOp",EDGE,"E98.3.0.5")])]})]}),makeQuery(id+"F14.boolean.opBoolean","INTERSECT",EDGE,{"derivedFrom":[subQ2,makeQuery(id+"F14.opExtrude","SWEPT_FACE",FACE,{"disambiguationData":[OSD([sQuery(id+"F13.wireOp",EDGE,"E98.3.0.6")])]})]})]);}
            var Q47;
            {var subQ0=sQuery(id+"F0.wireOp",EDGE,"E61.top");var subQ2=makeQuery(id+"F4.boolean.opBoolean","MERGE",FACE,{"derivedFrom":[makeQuery(id+"F3.opExtrude","SWEPT_FACE",FACE,{"disambiguationData":[OSD([subQ0]),TDD([makeQuery(id+"F0.imprint","IMPRINT",EDGE,{"disambiguationData":[TD([[makeQuery(id+"F0.imprint","INTERSECT",VERTEX,{"derivedFrom":[subQ0,sQuery(id+"F0.wireOp",EDGE,"E77")]}),-1.0]])],"derivedFrom":subQ0}),makeQuery(id+"F0.imprint","IMPRINT",EDGE,{"disambiguationData":[TD([[makeQuery(id+"F0.imprint","INTERSECT",VERTEX,{"derivedFrom":[subQ0,sQuery(id+"F0.wireOp",EDGE,"E78")]}),1.0]])],"derivedFrom":subQ0})])]}),makeQuery(id+"F3.opExtrude","SWEPT_FACE",FACE,{"disambiguationData":[OSD([subQ0]),TDD([makeQuery(id+"F0.imprint","IMPRINT",EDGE,{"disambiguationData":[TD([[makeQuery(id+"F0.imprint","INTERSECT",VERTEX,{"derivedFrom":[subQ0,sQuery(id+"F0.wireOp",EDGE,"E62")]}),-1.0]])],"derivedFrom":subQ0})])]}),makeQuery(id+"F4.opExtrude","SWEPT_FACE",FACE,{"disambiguationData":[OSD([subQ0])]})]});Q47=qUnion([makeQuery(id+"F14.boolean.opBoolean","INTERSECT",EDGE,{"derivedFrom":[subQ2,makeQuery(id+"F14.opExtrude","SWEPT_FACE",FACE,{"disambiguationData":[OSD([sQuery(id+"F13.wireOp",EDGE,"E89")])]})]}),makeQuery(id+"F14.boolean.opBoolean","INTERSECT",EDGE,{"derivedFrom":[subQ2,makeQuery(id+"F14.opExtrude","SWEPT_FACE",FACE,{"disambiguationData":[OSD([sQuery(id+"F13.wireOp",EDGE,"E90")])]})]}),makeQuery(id+"F14.boolean.opBoolean","INTERSECT",EDGE,{"derivedFrom":[subQ2,makeQuery(id+"F14.opExtrude","SWEPT_FACE",FACE,{"disambiguationData":[OSD([sQuery(id+"F13.wireOp",EDGE,"E92")])]})]}),makeQuery(id+"F14.boolean.opBoolean","INTERSECT",EDGE,{"derivedFrom":[subQ2,makeQuery(id+"F14.opExtrude","SWEPT_FACE",FACE,{"disambiguationData":[OSD([sQuery(id+"F13.wireOp",EDGE,"E93")])]})]}),makeQuery(id+"F14.boolean.opBoolean","INTERSECT",EDGE,{"derivedFrom":[subQ2,makeQuery(id+"F14.opExtrude","SWEPT_FACE",FACE,{"disambiguationData":[OSD([sQuery(id+"F13.wireOp",EDGE,"E96")])]})]}),makeQuery(id+"F14.boolean.opBoolean","INTERSECT",EDGE,{"derivedFrom":[subQ2,makeQuery(id+"F14.opExtrude","SWEPT_FACE",FACE,{"disambiguationData":[OSD([sQuery(id+"F13.wireOp",EDGE,"E97")])]})]}),makeQuery(id+"F14.boolean.opBoolean","INTERSECT",EDGE,{"derivedFrom":[subQ2,makeQuery(id+"F14.opExtrude","SWEPT_FACE",FACE,{"disambiguationData":[OSD([sQuery(id+"F13.wireOp",EDGE,"E98.1.0.0")])]})]}),makeQuery(id+"F14.boolean.opBoolean","INTERSECT",EDGE,{"derivedFrom":[subQ2,makeQuery(id+"F14.opExtrude","SWEPT_FACE",FACE,{"disambiguationData":[OSD([sQuery(id+"F13.wireOp",EDGE,"E98.1.0.1")])]})]}),makeQuery(id+"F14.boolean.opBoolean","INTERSECT",EDGE,{"derivedFrom":[subQ2,makeQuery(id+"F14.opExtrude","SWEPT_FACE",FACE,{"disambiguationData":[OSD([sQuery(id+"F13.wireOp",EDGE,"E98.1.0.3")])]})]}),makeQuery(id+"F14.boolean.opBoolean","INTERSECT",EDGE,{"derivedFrom":[subQ2,makeQuery(id+"F14.opExtrude","SWEPT_FACE",FACE,{"disambiguationData":[OSD([sQuery(id+"F13.wireOp",EDGE,"E98.1.0.4")])]})]}),makeQuery(id+"F14.boolean.opBoolean","INTERSECT",EDGE,{"derivedFrom":[subQ2,makeQuery(id+"F14.opExtrude","SWEPT_FACE",FACE,{"disambiguationData":[OSD([sQuery(id+"F13.wireOp",EDGE,"E98.1.0.5")])]})]}),makeQuery(id+"F14.boolean.opBoolean","INTERSECT",EDGE,{"derivedFrom":[subQ2,makeQuery(id+"F14.opExtrude","SWEPT_FACE",FACE,{"disambiguationData":[OSD([sQuery(id+"F13.wireOp",EDGE,"E98.1.0.6")])]})]}),makeQuery(id+"F14.boolean.opBoolean","INTERSECT",EDGE,{"derivedFrom":[subQ2,makeQuery(id+"F14.opExtrude","SWEPT_FACE",FACE,{"disambiguationData":[OSD([sQuery(id+"F13.wireOp",EDGE,"E98.2.0.0")])]})]}),makeQuery(id+"F14.boolean.opBoolean","INTERSECT",EDGE,{"derivedFrom":[subQ2,makeQuery(id+"F14.opExtrude","SWEPT_FACE",FACE,{"disambiguationData":[OSD([sQuery(id+"F13.wireOp",EDGE,"E98.2.0.1")])]})]}),makeQuery(id+"F14.boolean.opBoolean","INTERSECT",EDGE,{"derivedFrom":[subQ2,makeQuery(id+"F14.opExtrude","SWEPT_FACE",FACE,{"disambiguationData":[OSD([sQuery(id+"F13.wireOp",EDGE,"E98.2.0.3")])]})]}),makeQuery(id+"F14.boolean.opBoolean","INTERSECT",EDGE,{"derivedFrom":[subQ2,makeQuery(id+"F14.opExtrude","SWEPT_FACE",FACE,{"disambiguationData":[OSD([sQuery(id+"F13.wireOp",EDGE,"E98.2.0.4")])]})]}),makeQuery(id+"F14.boolean.opBoolean","INTERSECT",EDGE,{"derivedFrom":[subQ2,makeQuery(id+"F14.opExtrude","SWEPT_FACE",FACE,{"disambiguationData":[OSD([sQuery(id+"F13.wireOp",EDGE,"E98.2.0.5")])]})]}),makeQuery(id+"F14.boolean.opBoolean","INTERSECT",EDGE,{"derivedFrom":[subQ2,makeQuery(id+"F14.opExtrude","SWEPT_FACE",FACE,{"disambiguationData":[OSD([sQuery(id+"F13.wireOp",EDGE,"E98.2.0.6")])]})]}),makeQuery(id+"F14.boolean.opBoolean","INTERSECT",EDGE,{"derivedFrom":[subQ2,makeQuery(id+"F14.opExtrude","SWEPT_FACE",FACE,{"disambiguationData":[OSD([sQuery(id+"F13.wireOp",EDGE,"E98.3.0.0")])]})]}),makeQuery(id+"F14.boolean.opBoolean","INTERSECT",EDGE,{"derivedFrom":[subQ2,makeQuery(id+"F14.opExtrude","SWEPT_FACE",FACE,{"disambiguationData":[OSD([sQuery(id+"F13.wireOp",EDGE,"E98.3.0.1")])]})]}),makeQuery(id+"F14.boolean.opBoolean","INTERSECT",EDGE,{"derivedFrom":[subQ2,makeQuery(id+"F14.opExtrude","SWEPT_FACE",FACE,{"disambiguationData":[OSD([sQuery(id+"F13.wireOp",EDGE,"E98.3.0.3")])]})]}),makeQuery(id+"F14.boolean.opBoolean","INTERSECT",EDGE,{"derivedFrom":[subQ2,makeQuery(id+"F14.opExtrude","SWEPT_FACE",FACE,{"disambiguationData":[OSD([sQuery(id+"F13.wireOp",EDGE,"E98.3.0.4")])]})]}),makeQuery(id+"F14.boolean.opBoolean","INTERSECT",EDGE,{"derivedFrom":[subQ2,makeQuery(id+"F14.opExtrude","SWEPT_FACE",FACE,{"disambiguationData":[OSD([sQuery(id+"F13.wireOp",EDGE,"E98.3.0.5")])]})]}),makeQuery(id+"F14.boolean.opBoolean","INTERSECT",EDGE,{"derivedFrom":[subQ2,makeQuery(id+"F14.opExtrude","SWEPT_FACE",FACE,{"disambiguationData":[OSD([sQuery(id+"F13.wireOp",EDGE,"E98.3.0.6")])]})]})]);}
            var Q48;
            {var subQ0=sQuery(id+"F0.wireOp",EDGE,"E61.top");var subQ2=makeQuery(id+"F4.boolean.opBoolean","MERGE",FACE,{"derivedFrom":[makeQuery(id+"F3.opExtrude","SWEPT_FACE",FACE,{"disambiguationData":[OSD([subQ0]),TDD([makeQuery(id+"F0.imprint","IMPRINT",EDGE,{"disambiguationData":[TD([[makeQuery(id+"F0.imprint","INTERSECT",VERTEX,{"derivedFrom":[subQ0,sQuery(id+"F0.wireOp",EDGE,"E77")]}),-1.0]])],"derivedFrom":subQ0}),makeQuery(id+"F0.imprint","IMPRINT",EDGE,{"disambiguationData":[TD([[makeQuery(id+"F0.imprint","INTERSECT",VERTEX,{"derivedFrom":[subQ0,sQuery(id+"F0.wireOp",EDGE,"E78")]}),1.0]])],"derivedFrom":subQ0})])]}),makeQuery(id+"F3.opExtrude","SWEPT_FACE",FACE,{"disambiguationData":[OSD([subQ0]),TDD([makeQuery(id+"F0.imprint","IMPRINT",EDGE,{"disambiguationData":[TD([[makeQuery(id+"F0.imprint","INTERSECT",VERTEX,{"derivedFrom":[subQ0,sQuery(id+"F0.wireOp",EDGE,"E62")]}),-1.0]])],"derivedFrom":subQ0})])]}),makeQuery(id+"F4.opExtrude","SWEPT_FACE",FACE,{"disambiguationData":[OSD([subQ0])]})]});Q48=qUnion([makeQuery(id+"F14.boolean.opBoolean","INTERSECT",EDGE,{"derivedFrom":[subQ2,makeQuery(id+"F14.opExtrude","SWEPT_FACE",FACE,{"disambiguationData":[OSD([sQuery(id+"F13.wireOp",EDGE,"E89")])]})]}),makeQuery(id+"F14.boolean.opBoolean","INTERSECT",EDGE,{"derivedFrom":[subQ2,makeQuery(id+"F14.opExtrude","SWEPT_FACE",FACE,{"disambiguationData":[OSD([sQuery(id+"F13.wireOp",EDGE,"E90")])]})]}),makeQuery(id+"F14.boolean.opBoolean","INTERSECT",EDGE,{"derivedFrom":[subQ2,makeQuery(id+"F14.opExtrude","SWEPT_FACE",FACE,{"disambiguationData":[OSD([sQuery(id+"F13.wireOp",EDGE,"E92")])]})]}),makeQuery(id+"F14.boolean.opBoolean","INTERSECT",EDGE,{"derivedFrom":[subQ2,makeQuery(id+"F14.opExtrude","SWEPT_FACE",FACE,{"disambiguationData":[OSD([sQuery(id+"F13.wireOp",EDGE,"E93")])]})]}),makeQuery(id+"F14.boolean.opBoolean","INTERSECT",EDGE,{"derivedFrom":[subQ2,makeQuery(id+"F14.opExtrude","SWEPT_FACE",FACE,{"disambiguationData":[OSD([sQuery(id+"F13.wireOp",EDGE,"E96")])]})]}),makeQuery(id+"F14.boolean.opBoolean","INTERSECT",EDGE,{"derivedFrom":[subQ2,makeQuery(id+"F14.opExtrude","SWEPT_FACE",FACE,{"disambiguationData":[OSD([sQuery(id+"F13.wireOp",EDGE,"E97")])]})]}),makeQuery(id+"F14.boolean.opBoolean","INTERSECT",EDGE,{"derivedFrom":[subQ2,makeQuery(id+"F14.opExtrude","SWEPT_FACE",FACE,{"disambiguationData":[OSD([sQuery(id+"F13.wireOp",EDGE,"E98.1.0.0")])]})]}),makeQuery(id+"F14.boolean.opBoolean","INTERSECT",EDGE,{"derivedFrom":[subQ2,makeQuery(id+"F14.opExtrude","SWEPT_FACE",FACE,{"disambiguationData":[OSD([sQuery(id+"F13.wireOp",EDGE,"E98.1.0.1")])]})]}),makeQuery(id+"F14.boolean.opBoolean","INTERSECT",EDGE,{"derivedFrom":[subQ2,makeQuery(id+"F14.opExtrude","SWEPT_FACE",FACE,{"disambiguationData":[OSD([sQuery(id+"F13.wireOp",EDGE,"E98.1.0.3")])]})]}),makeQuery(id+"F14.boolean.opBoolean","INTERSECT",EDGE,{"derivedFrom":[subQ2,makeQuery(id+"F14.opExtrude","SWEPT_FACE",FACE,{"disambiguationData":[OSD([sQuery(id+"F13.wireOp",EDGE,"E98.1.0.4")])]})]}),makeQuery(id+"F14.boolean.opBoolean","INTERSECT",EDGE,{"derivedFrom":[subQ2,makeQuery(id+"F14.opExtrude","SWEPT_FACE",FACE,{"disambiguationData":[OSD([sQuery(id+"F13.wireOp",EDGE,"E98.1.0.5")])]})]}),makeQuery(id+"F14.boolean.opBoolean","INTERSECT",EDGE,{"derivedFrom":[subQ2,makeQuery(id+"F14.opExtrude","SWEPT_FACE",FACE,{"disambiguationData":[OSD([sQuery(id+"F13.wireOp",EDGE,"E98.1.0.6")])]})]}),makeQuery(id+"F14.boolean.opBoolean","INTERSECT",EDGE,{"derivedFrom":[subQ2,makeQuery(id+"F14.opExtrude","SWEPT_FACE",FACE,{"disambiguationData":[OSD([sQuery(id+"F13.wireOp",EDGE,"E98.2.0.0")])]})]}),makeQuery(id+"F14.boolean.opBoolean","INTERSECT",EDGE,{"derivedFrom":[subQ2,makeQuery(id+"F14.opExtrude","SWEPT_FACE",FACE,{"disambiguationData":[OSD([sQuery(id+"F13.wireOp",EDGE,"E98.2.0.1")])]})]}),makeQuery(id+"F14.boolean.opBoolean","INTERSECT",EDGE,{"derivedFrom":[subQ2,makeQuery(id+"F14.opExtrude","SWEPT_FACE",FACE,{"disambiguationData":[OSD([sQuery(id+"F13.wireOp",EDGE,"E98.2.0.3")])]})]}),makeQuery(id+"F14.boolean.opBoolean","INTERSECT",EDGE,{"derivedFrom":[subQ2,makeQuery(id+"F14.opExtrude","SWEPT_FACE",FACE,{"disambiguationData":[OSD([sQuery(id+"F13.wireOp",EDGE,"E98.2.0.4")])]})]}),makeQuery(id+"F14.boolean.opBoolean","INTERSECT",EDGE,{"derivedFrom":[subQ2,makeQuery(id+"F14.opExtrude","SWEPT_FACE",FACE,{"disambiguationData":[OSD([sQuery(id+"F13.wireOp",EDGE,"E98.2.0.5")])]})]}),makeQuery(id+"F14.boolean.opBoolean","INTERSECT",EDGE,{"derivedFrom":[subQ2,makeQuery(id+"F14.opExtrude","SWEPT_FACE",FACE,{"disambiguationData":[OSD([sQuery(id+"F13.wireOp",EDGE,"E98.2.0.6")])]})]}),makeQuery(id+"F14.boolean.opBoolean","INTERSECT",EDGE,{"derivedFrom":[subQ2,makeQuery(id+"F14.opExtrude","SWEPT_FACE",FACE,{"disambiguationData":[OSD([sQuery(id+"F13.wireOp",EDGE,"E98.3.0.0")])]})]}),makeQuery(id+"F14.boolean.opBoolean","INTERSECT",EDGE,{"derivedFrom":[subQ2,makeQuery(id+"F14.opExtrude","SWEPT_FACE",FACE,{"disambiguationData":[OSD([sQuery(id+"F13.wireOp",EDGE,"E98.3.0.1")])]})]}),makeQuery(id+"F14.boolean.opBoolean","INTERSECT",EDGE,{"derivedFrom":[subQ2,makeQuery(id+"F14.opExtrude","SWEPT_FACE",FACE,{"disambiguationData":[OSD([sQuery(id+"F13.wireOp",EDGE,"E98.3.0.3")])]})]}),makeQuery(id+"F14.boolean.opBoolean","INTERSECT",EDGE,{"derivedFrom":[subQ2,makeQuery(id+"F14.opExtrude","SWEPT_FACE",FACE,{"disambiguationData":[OSD([sQuery(id+"F13.wireOp",EDGE,"E98.3.0.4")])]})]}),makeQuery(id+"F14.boolean.opBoolean","INTERSECT",EDGE,{"derivedFrom":[subQ2,makeQuery(id+"F14.opExtrude","SWEPT_FACE",FACE,{"disambiguationData":[OSD([sQuery(id+"F13.wireOp",EDGE,"E98.3.0.5")])]})]}),makeQuery(id+"F14.boolean.opBoolean","INTERSECT",EDGE,{"derivedFrom":[subQ2,makeQuery(id+"F14.opExtrude","SWEPT_FACE",FACE,{"disambiguationData":[OSD([sQuery(id+"F13.wireOp",EDGE,"E98.3.0.6")])]})]})]);}
            var Q49;
            {var subQ0=sQuery(id+"F0.wireOp",EDGE,"E61.top");var subQ2=makeQuery(id+"F4.boolean.opBoolean","MERGE",FACE,{"derivedFrom":[makeQuery(id+"F3.opExtrude","SWEPT_FACE",FACE,{"disambiguationData":[OSD([subQ0]),TDD([makeQuery(id+"F0.imprint","IMPRINT",EDGE,{"disambiguationData":[TD([[makeQuery(id+"F0.imprint","INTERSECT",VERTEX,{"derivedFrom":[subQ0,sQuery(id+"F0.wireOp",EDGE,"E77")]}),-1.0]])],"derivedFrom":subQ0}),makeQuery(id+"F0.imprint","IMPRINT",EDGE,{"disambiguationData":[TD([[makeQuery(id+"F0.imprint","INTERSECT",VERTEX,{"derivedFrom":[subQ0,sQuery(id+"F0.wireOp",EDGE,"E78")]}),1.0]])],"derivedFrom":subQ0})])]}),makeQuery(id+"F3.opExtrude","SWEPT_FACE",FACE,{"disambiguationData":[OSD([subQ0]),TDD([makeQuery(id+"F0.imprint","IMPRINT",EDGE,{"disambiguationData":[TD([[makeQuery(id+"F0.imprint","INTERSECT",VERTEX,{"derivedFrom":[subQ0,sQuery(id+"F0.wireOp",EDGE,"E62")]}),-1.0]])],"derivedFrom":subQ0})])]}),makeQuery(id+"F4.opExtrude","SWEPT_FACE",FACE,{"disambiguationData":[OSD([subQ0])]})]});Q49=qUnion([makeQuery(id+"F14.boolean.opBoolean","INTERSECT",EDGE,{"derivedFrom":[subQ2,makeQuery(id+"F14.opExtrude","SWEPT_FACE",FACE,{"disambiguationData":[OSD([sQuery(id+"F13.wireOp",EDGE,"E89")])]})]}),makeQuery(id+"F14.boolean.opBoolean","INTERSECT",EDGE,{"derivedFrom":[subQ2,makeQuery(id+"F14.opExtrude","SWEPT_FACE",FACE,{"disambiguationData":[OSD([sQuery(id+"F13.wireOp",EDGE,"E90")])]})]}),makeQuery(id+"F14.boolean.opBoolean","INTERSECT",EDGE,{"derivedFrom":[subQ2,makeQuery(id+"F14.opExtrude","SWEPT_FACE",FACE,{"disambiguationData":[OSD([sQuery(id+"F13.wireOp",EDGE,"E92")])]})]}),makeQuery(id+"F14.boolean.opBoolean","INTERSECT",EDGE,{"derivedFrom":[subQ2,makeQuery(id+"F14.opExtrude","SWEPT_FACE",FACE,{"disambiguationData":[OSD([sQuery(id+"F13.wireOp",EDGE,"E93")])]})]}),makeQuery(id+"F14.boolean.opBoolean","INTERSECT",EDGE,{"derivedFrom":[subQ2,makeQuery(id+"F14.opExtrude","SWEPT_FACE",FACE,{"disambiguationData":[OSD([sQuery(id+"F13.wireOp",EDGE,"E96")])]})]}),makeQuery(id+"F14.boolean.opBoolean","INTERSECT",EDGE,{"derivedFrom":[subQ2,makeQuery(id+"F14.opExtrude","SWEPT_FACE",FACE,{"disambiguationData":[OSD([sQuery(id+"F13.wireOp",EDGE,"E97")])]})]}),makeQuery(id+"F14.boolean.opBoolean","INTERSECT",EDGE,{"derivedFrom":[subQ2,makeQuery(id+"F14.opExtrude","SWEPT_FACE",FACE,{"disambiguationData":[OSD([sQuery(id+"F13.wireOp",EDGE,"E98.1.0.0")])]})]}),makeQuery(id+"F14.boolean.opBoolean","INTERSECT",EDGE,{"derivedFrom":[subQ2,makeQuery(id+"F14.opExtrude","SWEPT_FACE",FACE,{"disambiguationData":[OSD([sQuery(id+"F13.wireOp",EDGE,"E98.1.0.1")])]})]}),makeQuery(id+"F14.boolean.opBoolean","INTERSECT",EDGE,{"derivedFrom":[subQ2,makeQuery(id+"F14.opExtrude","SWEPT_FACE",FACE,{"disambiguationData":[OSD([sQuery(id+"F13.wireOp",EDGE,"E98.1.0.3")])]})]}),makeQuery(id+"F14.boolean.opBoolean","INTERSECT",EDGE,{"derivedFrom":[subQ2,makeQuery(id+"F14.opExtrude","SWEPT_FACE",FACE,{"disambiguationData":[OSD([sQuery(id+"F13.wireOp",EDGE,"E98.1.0.4")])]})]}),makeQuery(id+"F14.boolean.opBoolean","INTERSECT",EDGE,{"derivedFrom":[subQ2,makeQuery(id+"F14.opExtrude","SWEPT_FACE",FACE,{"disambiguationData":[OSD([sQuery(id+"F13.wireOp",EDGE,"E98.1.0.5")])]})]}),makeQuery(id+"F14.boolean.opBoolean","INTERSECT",EDGE,{"derivedFrom":[subQ2,makeQuery(id+"F14.opExtrude","SWEPT_FACE",FACE,{"disambiguationData":[OSD([sQuery(id+"F13.wireOp",EDGE,"E98.1.0.6")])]})]}),makeQuery(id+"F14.boolean.opBoolean","INTERSECT",EDGE,{"derivedFrom":[subQ2,makeQuery(id+"F14.opExtrude","SWEPT_FACE",FACE,{"disambiguationData":[OSD([sQuery(id+"F13.wireOp",EDGE,"E98.2.0.0")])]})]}),makeQuery(id+"F14.boolean.opBoolean","INTERSECT",EDGE,{"derivedFrom":[subQ2,makeQuery(id+"F14.opExtrude","SWEPT_FACE",FACE,{"disambiguationData":[OSD([sQuery(id+"F13.wireOp",EDGE,"E98.2.0.1")])]})]}),makeQuery(id+"F14.boolean.opBoolean","INTERSECT",EDGE,{"derivedFrom":[subQ2,makeQuery(id+"F14.opExtrude","SWEPT_FACE",FACE,{"disambiguationData":[OSD([sQuery(id+"F13.wireOp",EDGE,"E98.2.0.3")])]})]}),makeQuery(id+"F14.boolean.opBoolean","INTERSECT",EDGE,{"derivedFrom":[subQ2,makeQuery(id+"F14.opExtrude","SWEPT_FACE",FACE,{"disambiguationData":[OSD([sQuery(id+"F13.wireOp",EDGE,"E98.2.0.4")])]})]}),makeQuery(id+"F14.boolean.opBoolean","INTERSECT",EDGE,{"derivedFrom":[subQ2,makeQuery(id+"F14.opExtrude","SWEPT_FACE",FACE,{"disambiguationData":[OSD([sQuery(id+"F13.wireOp",EDGE,"E98.2.0.5")])]})]}),makeQuery(id+"F14.boolean.opBoolean","INTERSECT",EDGE,{"derivedFrom":[subQ2,makeQuery(id+"F14.opExtrude","SWEPT_FACE",FACE,{"disambiguationData":[OSD([sQuery(id+"F13.wireOp",EDGE,"E98.2.0.6")])]})]}),makeQuery(id+"F14.boolean.opBoolean","INTERSECT",EDGE,{"derivedFrom":[subQ2,makeQuery(id+"F14.opExtrude","SWEPT_FACE",FACE,{"disambiguationData":[OSD([sQuery(id+"F13.wireOp",EDGE,"E98.3.0.0")])]})]}),makeQuery(id+"F14.boolean.opBoolean","INTERSECT",EDGE,{"derivedFrom":[subQ2,makeQuery(id+"F14.opExtrude","SWEPT_FACE",FACE,{"disambiguationData":[OSD([sQuery(id+"F13.wireOp",EDGE,"E98.3.0.1")])]})]}),makeQuery(id+"F14.boolean.opBoolean","INTERSECT",EDGE,{"derivedFrom":[subQ2,makeQuery(id+"F14.opExtrude","SWEPT_FACE",FACE,{"disambiguationData":[OSD([sQuery(id+"F13.wireOp",EDGE,"E98.3.0.3")])]})]}),makeQuery(id+"F14.boolean.opBoolean","INTERSECT",EDGE,{"derivedFrom":[subQ2,makeQuery(id+"F14.opExtrude","SWEPT_FACE",FACE,{"disambiguationData":[OSD([sQuery(id+"F13.wireOp",EDGE,"E98.3.0.4")])]})]}),makeQuery(id+"F14.boolean.opBoolean","INTERSECT",EDGE,{"derivedFrom":[subQ2,makeQuery(id+"F14.opExtrude","SWEPT_FACE",FACE,{"disambiguationData":[OSD([sQuery(id+"F13.wireOp",EDGE,"E98.3.0.5")])]})]}),makeQuery(id+"F14.boolean.opBoolean","INTERSECT",EDGE,{"derivedFrom":[subQ2,makeQuery(id+"F14.opExtrude","SWEPT_FACE",FACE,{"disambiguationData":[OSD([sQuery(id+"F13.wireOp",EDGE,"E98.3.0.6")])]})]})]);}
            var Q50;
            {var subQ0=sQuery(id+"F0.wireOp",EDGE,"E61.top");var subQ2=makeQuery(id+"F4.boolean.opBoolean","MERGE",FACE,{"derivedFrom":[makeQuery(id+"F3.opExtrude","SWEPT_FACE",FACE,{"disambiguationData":[OSD([subQ0]),TDD([makeQuery(id+"F0.imprint","IMPRINT",EDGE,{"disambiguationData":[TD([[makeQuery(id+"F0.imprint","INTERSECT",VERTEX,{"derivedFrom":[subQ0,sQuery(id+"F0.wireOp",EDGE,"E77")]}),-1.0]])],"derivedFrom":subQ0}),makeQuery(id+"F0.imprint","IMPRINT",EDGE,{"disambiguationData":[TD([[makeQuery(id+"F0.imprint","INTERSECT",VERTEX,{"derivedFrom":[subQ0,sQuery(id+"F0.wireOp",EDGE,"E78")]}),1.0]])],"derivedFrom":subQ0})])]}),makeQuery(id+"F3.opExtrude","SWEPT_FACE",FACE,{"disambiguationData":[OSD([subQ0]),TDD([makeQuery(id+"F0.imprint","IMPRINT",EDGE,{"disambiguationData":[TD([[makeQuery(id+"F0.imprint","INTERSECT",VERTEX,{"derivedFrom":[subQ0,sQuery(id+"F0.wireOp",EDGE,"E62")]}),-1.0]])],"derivedFrom":subQ0})])]}),makeQuery(id+"F4.opExtrude","SWEPT_FACE",FACE,{"disambiguationData":[OSD([subQ0])]})]});Q50=qUnion([makeQuery(id+"F14.boolean.opBoolean","INTERSECT",EDGE,{"derivedFrom":[subQ2,makeQuery(id+"F14.opExtrude","SWEPT_FACE",FACE,{"disambiguationData":[OSD([sQuery(id+"F13.wireOp",EDGE,"E89")])]})]}),makeQuery(id+"F14.boolean.opBoolean","INTERSECT",EDGE,{"derivedFrom":[subQ2,makeQuery(id+"F14.opExtrude","SWEPT_FACE",FACE,{"disambiguationData":[OSD([sQuery(id+"F13.wireOp",EDGE,"E90")])]})]}),makeQuery(id+"F14.boolean.opBoolean","INTERSECT",EDGE,{"derivedFrom":[subQ2,makeQuery(id+"F14.opExtrude","SWEPT_FACE",FACE,{"disambiguationData":[OSD([sQuery(id+"F13.wireOp",EDGE,"E92")])]})]}),makeQuery(id+"F14.boolean.opBoolean","INTERSECT",EDGE,{"derivedFrom":[subQ2,makeQuery(id+"F14.opExtrude","SWEPT_FACE",FACE,{"disambiguationData":[OSD([sQuery(id+"F13.wireOp",EDGE,"E93")])]})]}),makeQuery(id+"F14.boolean.opBoolean","INTERSECT",EDGE,{"derivedFrom":[subQ2,makeQuery(id+"F14.opExtrude","SWEPT_FACE",FACE,{"disambiguationData":[OSD([sQuery(id+"F13.wireOp",EDGE,"E96")])]})]}),makeQuery(id+"F14.boolean.opBoolean","INTERSECT",EDGE,{"derivedFrom":[subQ2,makeQuery(id+"F14.opExtrude","SWEPT_FACE",FACE,{"disambiguationData":[OSD([sQuery(id+"F13.wireOp",EDGE,"E97")])]})]}),makeQuery(id+"F14.boolean.opBoolean","INTERSECT",EDGE,{"derivedFrom":[subQ2,makeQuery(id+"F14.opExtrude","SWEPT_FACE",FACE,{"disambiguationData":[OSD([sQuery(id+"F13.wireOp",EDGE,"E98.1.0.0")])]})]}),makeQuery(id+"F14.boolean.opBoolean","INTERSECT",EDGE,{"derivedFrom":[subQ2,makeQuery(id+"F14.opExtrude","SWEPT_FACE",FACE,{"disambiguationData":[OSD([sQuery(id+"F13.wireOp",EDGE,"E98.1.0.1")])]})]}),makeQuery(id+"F14.boolean.opBoolean","INTERSECT",EDGE,{"derivedFrom":[subQ2,makeQuery(id+"F14.opExtrude","SWEPT_FACE",FACE,{"disambiguationData":[OSD([sQuery(id+"F13.wireOp",EDGE,"E98.1.0.3")])]})]}),makeQuery(id+"F14.boolean.opBoolean","INTERSECT",EDGE,{"derivedFrom":[subQ2,makeQuery(id+"F14.opExtrude","SWEPT_FACE",FACE,{"disambiguationData":[OSD([sQuery(id+"F13.wireOp",EDGE,"E98.1.0.4")])]})]}),makeQuery(id+"F14.boolean.opBoolean","INTERSECT",EDGE,{"derivedFrom":[subQ2,makeQuery(id+"F14.opExtrude","SWEPT_FACE",FACE,{"disambiguationData":[OSD([sQuery(id+"F13.wireOp",EDGE,"E98.1.0.5")])]})]}),makeQuery(id+"F14.boolean.opBoolean","INTERSECT",EDGE,{"derivedFrom":[subQ2,makeQuery(id+"F14.opExtrude","SWEPT_FACE",FACE,{"disambiguationData":[OSD([sQuery(id+"F13.wireOp",EDGE,"E98.1.0.6")])]})]}),makeQuery(id+"F14.boolean.opBoolean","INTERSECT",EDGE,{"derivedFrom":[subQ2,makeQuery(id+"F14.opExtrude","SWEPT_FACE",FACE,{"disambiguationData":[OSD([sQuery(id+"F13.wireOp",EDGE,"E98.2.0.0")])]})]}),makeQuery(id+"F14.boolean.opBoolean","INTERSECT",EDGE,{"derivedFrom":[subQ2,makeQuery(id+"F14.opExtrude","SWEPT_FACE",FACE,{"disambiguationData":[OSD([sQuery(id+"F13.wireOp",EDGE,"E98.2.0.1")])]})]}),makeQuery(id+"F14.boolean.opBoolean","INTERSECT",EDGE,{"derivedFrom":[subQ2,makeQuery(id+"F14.opExtrude","SWEPT_FACE",FACE,{"disambiguationData":[OSD([sQuery(id+"F13.wireOp",EDGE,"E98.2.0.3")])]})]}),makeQuery(id+"F14.boolean.opBoolean","INTERSECT",EDGE,{"derivedFrom":[subQ2,makeQuery(id+"F14.opExtrude","SWEPT_FACE",FACE,{"disambiguationData":[OSD([sQuery(id+"F13.wireOp",EDGE,"E98.2.0.4")])]})]}),makeQuery(id+"F14.boolean.opBoolean","INTERSECT",EDGE,{"derivedFrom":[subQ2,makeQuery(id+"F14.opExtrude","SWEPT_FACE",FACE,{"disambiguationData":[OSD([sQuery(id+"F13.wireOp",EDGE,"E98.2.0.5")])]})]}),makeQuery(id+"F14.boolean.opBoolean","INTERSECT",EDGE,{"derivedFrom":[subQ2,makeQuery(id+"F14.opExtrude","SWEPT_FACE",FACE,{"disambiguationData":[OSD([sQuery(id+"F13.wireOp",EDGE,"E98.2.0.6")])]})]}),makeQuery(id+"F14.boolean.opBoolean","INTERSECT",EDGE,{"derivedFrom":[subQ2,makeQuery(id+"F14.opExtrude","SWEPT_FACE",FACE,{"disambiguationData":[OSD([sQuery(id+"F13.wireOp",EDGE,"E98.3.0.0")])]})]}),makeQuery(id+"F14.boolean.opBoolean","INTERSECT",EDGE,{"derivedFrom":[subQ2,makeQuery(id+"F14.opExtrude","SWEPT_FACE",FACE,{"disambiguationData":[OSD([sQuery(id+"F13.wireOp",EDGE,"E98.3.0.1")])]})]}),makeQuery(id+"F14.boolean.opBoolean","INTERSECT",EDGE,{"derivedFrom":[subQ2,makeQuery(id+"F14.opExtrude","SWEPT_FACE",FACE,{"disambiguationData":[OSD([sQuery(id+"F13.wireOp",EDGE,"E98.3.0.3")])]})]}),makeQuery(id+"F14.boolean.opBoolean","INTERSECT",EDGE,{"derivedFrom":[subQ2,makeQuery(id+"F14.opExtrude","SWEPT_FACE",FACE,{"disambiguationData":[OSD([sQuery(id+"F13.wireOp",EDGE,"E98.3.0.4")])]})]}),makeQuery(id+"F14.boolean.opBoolean","INTERSECT",EDGE,{"derivedFrom":[subQ2,makeQuery(id+"F14.opExtrude","SWEPT_FACE",FACE,{"disambiguationData":[OSD([sQuery(id+"F13.wireOp",EDGE,"E98.3.0.5")])]})]}),makeQuery(id+"F14.boolean.opBoolean","INTERSECT",EDGE,{"derivedFrom":[subQ2,makeQuery(id+"F14.opExtrude","SWEPT_FACE",FACE,{"disambiguationData":[OSD([sQuery(id+"F13.wireOp",EDGE,"E98.3.0.6")])]})]})]);}
            var Q51;
            {var subQ0=sQuery(id+"F0.wireOp",EDGE,"E61.top");var subQ2=makeQuery(id+"F4.boolean.opBoolean","MERGE",FACE,{"derivedFrom":[makeQuery(id+"F3.opExtrude","SWEPT_FACE",FACE,{"disambiguationData":[OSD([subQ0]),TDD([makeQuery(id+"F0.imprint","IMPRINT",EDGE,{"disambiguationData":[TD([[makeQuery(id+"F0.imprint","INTERSECT",VERTEX,{"derivedFrom":[subQ0,sQuery(id+"F0.wireOp",EDGE,"E77")]}),-1.0]])],"derivedFrom":subQ0}),makeQuery(id+"F0.imprint","IMPRINT",EDGE,{"disambiguationData":[TD([[makeQuery(id+"F0.imprint","INTERSECT",VERTEX,{"derivedFrom":[subQ0,sQuery(id+"F0.wireOp",EDGE,"E78")]}),1.0]])],"derivedFrom":subQ0})])]}),makeQuery(id+"F3.opExtrude","SWEPT_FACE",FACE,{"disambiguationData":[OSD([subQ0]),TDD([makeQuery(id+"F0.imprint","IMPRINT",EDGE,{"disambiguationData":[TD([[makeQuery(id+"F0.imprint","INTERSECT",VERTEX,{"derivedFrom":[subQ0,sQuery(id+"F0.wireOp",EDGE,"E62")]}),-1.0]])],"derivedFrom":subQ0})])]}),makeQuery(id+"F4.opExtrude","SWEPT_FACE",FACE,{"disambiguationData":[OSD([subQ0])]})]});Q51=qUnion([makeQuery(id+"F14.boolean.opBoolean","INTERSECT",EDGE,{"derivedFrom":[subQ2,makeQuery(id+"F14.opExtrude","SWEPT_FACE",FACE,{"disambiguationData":[OSD([sQuery(id+"F13.wireOp",EDGE,"E89")])]})]}),makeQuery(id+"F14.boolean.opBoolean","INTERSECT",EDGE,{"derivedFrom":[subQ2,makeQuery(id+"F14.opExtrude","SWEPT_FACE",FACE,{"disambiguationData":[OSD([sQuery(id+"F13.wireOp",EDGE,"E90")])]})]}),makeQuery(id+"F14.boolean.opBoolean","INTERSECT",EDGE,{"derivedFrom":[subQ2,makeQuery(id+"F14.opExtrude","SWEPT_FACE",FACE,{"disambiguationData":[OSD([sQuery(id+"F13.wireOp",EDGE,"E92")])]})]}),makeQuery(id+"F14.boolean.opBoolean","INTERSECT",EDGE,{"derivedFrom":[subQ2,makeQuery(id+"F14.opExtrude","SWEPT_FACE",FACE,{"disambiguationData":[OSD([sQuery(id+"F13.wireOp",EDGE,"E93")])]})]}),makeQuery(id+"F14.boolean.opBoolean","INTERSECT",EDGE,{"derivedFrom":[subQ2,makeQuery(id+"F14.opExtrude","SWEPT_FACE",FACE,{"disambiguationData":[OSD([sQuery(id+"F13.wireOp",EDGE,"E96")])]})]}),makeQuery(id+"F14.boolean.opBoolean","INTERSECT",EDGE,{"derivedFrom":[subQ2,makeQuery(id+"F14.opExtrude","SWEPT_FACE",FACE,{"disambiguationData":[OSD([sQuery(id+"F13.wireOp",EDGE,"E97")])]})]}),makeQuery(id+"F14.boolean.opBoolean","INTERSECT",EDGE,{"derivedFrom":[subQ2,makeQuery(id+"F14.opExtrude","SWEPT_FACE",FACE,{"disambiguationData":[OSD([sQuery(id+"F13.wireOp",EDGE,"E98.1.0.0")])]})]}),makeQuery(id+"F14.boolean.opBoolean","INTERSECT",EDGE,{"derivedFrom":[subQ2,makeQuery(id+"F14.opExtrude","SWEPT_FACE",FACE,{"disambiguationData":[OSD([sQuery(id+"F13.wireOp",EDGE,"E98.1.0.1")])]})]}),makeQuery(id+"F14.boolean.opBoolean","INTERSECT",EDGE,{"derivedFrom":[subQ2,makeQuery(id+"F14.opExtrude","SWEPT_FACE",FACE,{"disambiguationData":[OSD([sQuery(id+"F13.wireOp",EDGE,"E98.1.0.3")])]})]}),makeQuery(id+"F14.boolean.opBoolean","INTERSECT",EDGE,{"derivedFrom":[subQ2,makeQuery(id+"F14.opExtrude","SWEPT_FACE",FACE,{"disambiguationData":[OSD([sQuery(id+"F13.wireOp",EDGE,"E98.1.0.4")])]})]}),makeQuery(id+"F14.boolean.opBoolean","INTERSECT",EDGE,{"derivedFrom":[subQ2,makeQuery(id+"F14.opExtrude","SWEPT_FACE",FACE,{"disambiguationData":[OSD([sQuery(id+"F13.wireOp",EDGE,"E98.1.0.5")])]})]}),makeQuery(id+"F14.boolean.opBoolean","INTERSECT",EDGE,{"derivedFrom":[subQ2,makeQuery(id+"F14.opExtrude","SWEPT_FACE",FACE,{"disambiguationData":[OSD([sQuery(id+"F13.wireOp",EDGE,"E98.1.0.6")])]})]}),makeQuery(id+"F14.boolean.opBoolean","INTERSECT",EDGE,{"derivedFrom":[subQ2,makeQuery(id+"F14.opExtrude","SWEPT_FACE",FACE,{"disambiguationData":[OSD([sQuery(id+"F13.wireOp",EDGE,"E98.2.0.0")])]})]}),makeQuery(id+"F14.boolean.opBoolean","INTERSECT",EDGE,{"derivedFrom":[subQ2,makeQuery(id+"F14.opExtrude","SWEPT_FACE",FACE,{"disambiguationData":[OSD([sQuery(id+"F13.wireOp",EDGE,"E98.2.0.1")])]})]}),makeQuery(id+"F14.boolean.opBoolean","INTERSECT",EDGE,{"derivedFrom":[subQ2,makeQuery(id+"F14.opExtrude","SWEPT_FACE",FACE,{"disambiguationData":[OSD([sQuery(id+"F13.wireOp",EDGE,"E98.2.0.3")])]})]}),makeQuery(id+"F14.boolean.opBoolean","INTERSECT",EDGE,{"derivedFrom":[subQ2,makeQuery(id+"F14.opExtrude","SWEPT_FACE",FACE,{"disambiguationData":[OSD([sQuery(id+"F13.wireOp",EDGE,"E98.2.0.4")])]})]}),makeQuery(id+"F14.boolean.opBoolean","INTERSECT",EDGE,{"derivedFrom":[subQ2,makeQuery(id+"F14.opExtrude","SWEPT_FACE",FACE,{"disambiguationData":[OSD([sQuery(id+"F13.wireOp",EDGE,"E98.2.0.5")])]})]}),makeQuery(id+"F14.boolean.opBoolean","INTERSECT",EDGE,{"derivedFrom":[subQ2,makeQuery(id+"F14.opExtrude","SWEPT_FACE",FACE,{"disambiguationData":[OSD([sQuery(id+"F13.wireOp",EDGE,"E98.2.0.6")])]})]}),makeQuery(id+"F14.boolean.opBoolean","INTERSECT",EDGE,{"derivedFrom":[subQ2,makeQuery(id+"F14.opExtrude","SWEPT_FACE",FACE,{"disambiguationData":[OSD([sQuery(id+"F13.wireOp",EDGE,"E98.3.0.0")])]})]}),makeQuery(id+"F14.boolean.opBoolean","INTERSECT",EDGE,{"derivedFrom":[subQ2,makeQuery(id+"F14.opExtrude","SWEPT_FACE",FACE,{"disambiguationData":[OSD([sQuery(id+"F13.wireOp",EDGE,"E98.3.0.1")])]})]}),makeQuery(id+"F14.boolean.opBoolean","INTERSECT",EDGE,{"derivedFrom":[subQ2,makeQuery(id+"F14.opExtrude","SWEPT_FACE",FACE,{"disambiguationData":[OSD([sQuery(id+"F13.wireOp",EDGE,"E98.3.0.3")])]})]}),makeQuery(id+"F14.boolean.opBoolean","INTERSECT",EDGE,{"derivedFrom":[subQ2,makeQuery(id+"F14.opExtrude","SWEPT_FACE",FACE,{"disambiguationData":[OSD([sQuery(id+"F13.wireOp",EDGE,"E98.3.0.4")])]})]}),makeQuery(id+"F14.boolean.opBoolean","INTERSECT",EDGE,{"derivedFrom":[subQ2,makeQuery(id+"F14.opExtrude","SWEPT_FACE",FACE,{"disambiguationData":[OSD([sQuery(id+"F13.wireOp",EDGE,"E98.3.0.5")])]})]}),makeQuery(id+"F14.boolean.opBoolean","INTERSECT",EDGE,{"derivedFrom":[subQ2,makeQuery(id+"F14.opExtrude","SWEPT_FACE",FACE,{"disambiguationData":[OSD([sQuery(id+"F13.wireOp",EDGE,"E98.3.0.6")])]})]})]);}
            var Q52;
            {var subQ0=sQuery(id+"F0.wireOp",EDGE,"E61.top");var subQ2=makeQuery(id+"F4.boolean.opBoolean","MERGE",FACE,{"derivedFrom":[makeQuery(id+"F3.opExtrude","SWEPT_FACE",FACE,{"disambiguationData":[OSD([subQ0]),TDD([makeQuery(id+"F0.imprint","IMPRINT",EDGE,{"disambiguationData":[TD([[makeQuery(id+"F0.imprint","INTERSECT",VERTEX,{"derivedFrom":[subQ0,sQuery(id+"F0.wireOp",EDGE,"E77")]}),-1.0]])],"derivedFrom":subQ0}),makeQuery(id+"F0.imprint","IMPRINT",EDGE,{"disambiguationData":[TD([[makeQuery(id+"F0.imprint","INTERSECT",VERTEX,{"derivedFrom":[subQ0,sQuery(id+"F0.wireOp",EDGE,"E78")]}),1.0]])],"derivedFrom":subQ0})])]}),makeQuery(id+"F3.opExtrude","SWEPT_FACE",FACE,{"disambiguationData":[OSD([subQ0]),TDD([makeQuery(id+"F0.imprint","IMPRINT",EDGE,{"disambiguationData":[TD([[makeQuery(id+"F0.imprint","INTERSECT",VERTEX,{"derivedFrom":[subQ0,sQuery(id+"F0.wireOp",EDGE,"E62")]}),-1.0]])],"derivedFrom":subQ0})])]}),makeQuery(id+"F4.opExtrude","SWEPT_FACE",FACE,{"disambiguationData":[OSD([subQ0])]})]});Q52=qUnion([makeQuery(id+"F14.boolean.opBoolean","INTERSECT",EDGE,{"derivedFrom":[subQ2,makeQuery(id+"F14.opExtrude","SWEPT_FACE",FACE,{"disambiguationData":[OSD([sQuery(id+"F13.wireOp",EDGE,"E89")])]})]}),makeQuery(id+"F14.boolean.opBoolean","INTERSECT",EDGE,{"derivedFrom":[subQ2,makeQuery(id+"F14.opExtrude","SWEPT_FACE",FACE,{"disambiguationData":[OSD([sQuery(id+"F13.wireOp",EDGE,"E90")])]})]}),makeQuery(id+"F14.boolean.opBoolean","INTERSECT",EDGE,{"derivedFrom":[subQ2,makeQuery(id+"F14.opExtrude","SWEPT_FACE",FACE,{"disambiguationData":[OSD([sQuery(id+"F13.wireOp",EDGE,"E92")])]})]}),makeQuery(id+"F14.boolean.opBoolean","INTERSECT",EDGE,{"derivedFrom":[subQ2,makeQuery(id+"F14.opExtrude","SWEPT_FACE",FACE,{"disambiguationData":[OSD([sQuery(id+"F13.wireOp",EDGE,"E93")])]})]}),makeQuery(id+"F14.boolean.opBoolean","INTERSECT",EDGE,{"derivedFrom":[subQ2,makeQuery(id+"F14.opExtrude","SWEPT_FACE",FACE,{"disambiguationData":[OSD([sQuery(id+"F13.wireOp",EDGE,"E96")])]})]}),makeQuery(id+"F14.boolean.opBoolean","INTERSECT",EDGE,{"derivedFrom":[subQ2,makeQuery(id+"F14.opExtrude","SWEPT_FACE",FACE,{"disambiguationData":[OSD([sQuery(id+"F13.wireOp",EDGE,"E97")])]})]}),makeQuery(id+"F14.boolean.opBoolean","INTERSECT",EDGE,{"derivedFrom":[subQ2,makeQuery(id+"F14.opExtrude","SWEPT_FACE",FACE,{"disambiguationData":[OSD([sQuery(id+"F13.wireOp",EDGE,"E98.1.0.0")])]})]}),makeQuery(id+"F14.boolean.opBoolean","INTERSECT",EDGE,{"derivedFrom":[subQ2,makeQuery(id+"F14.opExtrude","SWEPT_FACE",FACE,{"disambiguationData":[OSD([sQuery(id+"F13.wireOp",EDGE,"E98.1.0.1")])]})]}),makeQuery(id+"F14.boolean.opBoolean","INTERSECT",EDGE,{"derivedFrom":[subQ2,makeQuery(id+"F14.opExtrude","SWEPT_FACE",FACE,{"disambiguationData":[OSD([sQuery(id+"F13.wireOp",EDGE,"E98.1.0.3")])]})]}),makeQuery(id+"F14.boolean.opBoolean","INTERSECT",EDGE,{"derivedFrom":[subQ2,makeQuery(id+"F14.opExtrude","SWEPT_FACE",FACE,{"disambiguationData":[OSD([sQuery(id+"F13.wireOp",EDGE,"E98.1.0.4")])]})]}),makeQuery(id+"F14.boolean.opBoolean","INTERSECT",EDGE,{"derivedFrom":[subQ2,makeQuery(id+"F14.opExtrude","SWEPT_FACE",FACE,{"disambiguationData":[OSD([sQuery(id+"F13.wireOp",EDGE,"E98.1.0.5")])]})]}),makeQuery(id+"F14.boolean.opBoolean","INTERSECT",EDGE,{"derivedFrom":[subQ2,makeQuery(id+"F14.opExtrude","SWEPT_FACE",FACE,{"disambiguationData":[OSD([sQuery(id+"F13.wireOp",EDGE,"E98.1.0.6")])]})]}),makeQuery(id+"F14.boolean.opBoolean","INTERSECT",EDGE,{"derivedFrom":[subQ2,makeQuery(id+"F14.opExtrude","SWEPT_FACE",FACE,{"disambiguationData":[OSD([sQuery(id+"F13.wireOp",EDGE,"E98.2.0.0")])]})]}),makeQuery(id+"F14.boolean.opBoolean","INTERSECT",EDGE,{"derivedFrom":[subQ2,makeQuery(id+"F14.opExtrude","SWEPT_FACE",FACE,{"disambiguationData":[OSD([sQuery(id+"F13.wireOp",EDGE,"E98.2.0.1")])]})]}),makeQuery(id+"F14.boolean.opBoolean","INTERSECT",EDGE,{"derivedFrom":[subQ2,makeQuery(id+"F14.opExtrude","SWEPT_FACE",FACE,{"disambiguationData":[OSD([sQuery(id+"F13.wireOp",EDGE,"E98.2.0.3")])]})]}),makeQuery(id+"F14.boolean.opBoolean","INTERSECT",EDGE,{"derivedFrom":[subQ2,makeQuery(id+"F14.opExtrude","SWEPT_FACE",FACE,{"disambiguationData":[OSD([sQuery(id+"F13.wireOp",EDGE,"E98.2.0.4")])]})]}),makeQuery(id+"F14.boolean.opBoolean","INTERSECT",EDGE,{"derivedFrom":[subQ2,makeQuery(id+"F14.opExtrude","SWEPT_FACE",FACE,{"disambiguationData":[OSD([sQuery(id+"F13.wireOp",EDGE,"E98.2.0.5")])]})]}),makeQuery(id+"F14.boolean.opBoolean","INTERSECT",EDGE,{"derivedFrom":[subQ2,makeQuery(id+"F14.opExtrude","SWEPT_FACE",FACE,{"disambiguationData":[OSD([sQuery(id+"F13.wireOp",EDGE,"E98.2.0.6")])]})]}),makeQuery(id+"F14.boolean.opBoolean","INTERSECT",EDGE,{"derivedFrom":[subQ2,makeQuery(id+"F14.opExtrude","SWEPT_FACE",FACE,{"disambiguationData":[OSD([sQuery(id+"F13.wireOp",EDGE,"E98.3.0.0")])]})]}),makeQuery(id+"F14.boolean.opBoolean","INTERSECT",EDGE,{"derivedFrom":[subQ2,makeQuery(id+"F14.opExtrude","SWEPT_FACE",FACE,{"disambiguationData":[OSD([sQuery(id+"F13.wireOp",EDGE,"E98.3.0.1")])]})]}),makeQuery(id+"F14.boolean.opBoolean","INTERSECT",EDGE,{"derivedFrom":[subQ2,makeQuery(id+"F14.opExtrude","SWEPT_FACE",FACE,{"disambiguationData":[OSD([sQuery(id+"F13.wireOp",EDGE,"E98.3.0.3")])]})]}),makeQuery(id+"F14.boolean.opBoolean","INTERSECT",EDGE,{"derivedFrom":[subQ2,makeQuery(id+"F14.opExtrude","SWEPT_FACE",FACE,{"disambiguationData":[OSD([sQuery(id+"F13.wireOp",EDGE,"E98.3.0.4")])]})]}),makeQuery(id+"F14.boolean.opBoolean","INTERSECT",EDGE,{"derivedFrom":[subQ2,makeQuery(id+"F14.opExtrude","SWEPT_FACE",FACE,{"disambiguationData":[OSD([sQuery(id+"F13.wireOp",EDGE,"E98.3.0.5")])]})]}),makeQuery(id+"F14.boolean.opBoolean","INTERSECT",EDGE,{"derivedFrom":[subQ2,makeQuery(id+"F14.opExtrude","SWEPT_FACE",FACE,{"disambiguationData":[OSD([sQuery(id+"F13.wireOp",EDGE,"E98.3.0.6")])]})]})]);}
            var Q53;
            {var subQ0=sQuery(id+"F0.wireOp",EDGE,"E61.top");var subQ2=makeQuery(id+"F4.boolean.opBoolean","MERGE",FACE,{"derivedFrom":[makeQuery(id+"F3.opExtrude","SWEPT_FACE",FACE,{"disambiguationData":[OSD([subQ0]),TDD([makeQuery(id+"F0.imprint","IMPRINT",EDGE,{"disambiguationData":[TD([[makeQuery(id+"F0.imprint","INTERSECT",VERTEX,{"derivedFrom":[subQ0,sQuery(id+"F0.wireOp",EDGE,"E77")]}),-1.0]])],"derivedFrom":subQ0}),makeQuery(id+"F0.imprint","IMPRINT",EDGE,{"disambiguationData":[TD([[makeQuery(id+"F0.imprint","INTERSECT",VERTEX,{"derivedFrom":[subQ0,sQuery(id+"F0.wireOp",EDGE,"E78")]}),1.0]])],"derivedFrom":subQ0})])]}),makeQuery(id+"F3.opExtrude","SWEPT_FACE",FACE,{"disambiguationData":[OSD([subQ0]),TDD([makeQuery(id+"F0.imprint","IMPRINT",EDGE,{"disambiguationData":[TD([[makeQuery(id+"F0.imprint","INTERSECT",VERTEX,{"derivedFrom":[subQ0,sQuery(id+"F0.wireOp",EDGE,"E62")]}),-1.0]])],"derivedFrom":subQ0})])]}),makeQuery(id+"F4.opExtrude","SWEPT_FACE",FACE,{"disambiguationData":[OSD([subQ0])]})]});Q53=qUnion([makeQuery(id+"F14.boolean.opBoolean","INTERSECT",EDGE,{"derivedFrom":[subQ2,makeQuery(id+"F14.opExtrude","SWEPT_FACE",FACE,{"disambiguationData":[OSD([sQuery(id+"F13.wireOp",EDGE,"E89")])]})]}),makeQuery(id+"F14.boolean.opBoolean","INTERSECT",EDGE,{"derivedFrom":[subQ2,makeQuery(id+"F14.opExtrude","SWEPT_FACE",FACE,{"disambiguationData":[OSD([sQuery(id+"F13.wireOp",EDGE,"E90")])]})]}),makeQuery(id+"F14.boolean.opBoolean","INTERSECT",EDGE,{"derivedFrom":[subQ2,makeQuery(id+"F14.opExtrude","SWEPT_FACE",FACE,{"disambiguationData":[OSD([sQuery(id+"F13.wireOp",EDGE,"E92")])]})]}),makeQuery(id+"F14.boolean.opBoolean","INTERSECT",EDGE,{"derivedFrom":[subQ2,makeQuery(id+"F14.opExtrude","SWEPT_FACE",FACE,{"disambiguationData":[OSD([sQuery(id+"F13.wireOp",EDGE,"E93")])]})]}),makeQuery(id+"F14.boolean.opBoolean","INTERSECT",EDGE,{"derivedFrom":[subQ2,makeQuery(id+"F14.opExtrude","SWEPT_FACE",FACE,{"disambiguationData":[OSD([sQuery(id+"F13.wireOp",EDGE,"E96")])]})]}),makeQuery(id+"F14.boolean.opBoolean","INTERSECT",EDGE,{"derivedFrom":[subQ2,makeQuery(id+"F14.opExtrude","SWEPT_FACE",FACE,{"disambiguationData":[OSD([sQuery(id+"F13.wireOp",EDGE,"E97")])]})]}),makeQuery(id+"F14.boolean.opBoolean","INTERSECT",EDGE,{"derivedFrom":[subQ2,makeQuery(id+"F14.opExtrude","SWEPT_FACE",FACE,{"disambiguationData":[OSD([sQuery(id+"F13.wireOp",EDGE,"E98.1.0.0")])]})]}),makeQuery(id+"F14.boolean.opBoolean","INTERSECT",EDGE,{"derivedFrom":[subQ2,makeQuery(id+"F14.opExtrude","SWEPT_FACE",FACE,{"disambiguationData":[OSD([sQuery(id+"F13.wireOp",EDGE,"E98.1.0.1")])]})]}),makeQuery(id+"F14.boolean.opBoolean","INTERSECT",EDGE,{"derivedFrom":[subQ2,makeQuery(id+"F14.opExtrude","SWEPT_FACE",FACE,{"disambiguationData":[OSD([sQuery(id+"F13.wireOp",EDGE,"E98.1.0.3")])]})]}),makeQuery(id+"F14.boolean.opBoolean","INTERSECT",EDGE,{"derivedFrom":[subQ2,makeQuery(id+"F14.opExtrude","SWEPT_FACE",FACE,{"disambiguationData":[OSD([sQuery(id+"F13.wireOp",EDGE,"E98.1.0.4")])]})]}),makeQuery(id+"F14.boolean.opBoolean","INTERSECT",EDGE,{"derivedFrom":[subQ2,makeQuery(id+"F14.opExtrude","SWEPT_FACE",FACE,{"disambiguationData":[OSD([sQuery(id+"F13.wireOp",EDGE,"E98.1.0.5")])]})]}),makeQuery(id+"F14.boolean.opBoolean","INTERSECT",EDGE,{"derivedFrom":[subQ2,makeQuery(id+"F14.opExtrude","SWEPT_FACE",FACE,{"disambiguationData":[OSD([sQuery(id+"F13.wireOp",EDGE,"E98.1.0.6")])]})]}),makeQuery(id+"F14.boolean.opBoolean","INTERSECT",EDGE,{"derivedFrom":[subQ2,makeQuery(id+"F14.opExtrude","SWEPT_FACE",FACE,{"disambiguationData":[OSD([sQuery(id+"F13.wireOp",EDGE,"E98.2.0.0")])]})]}),makeQuery(id+"F14.boolean.opBoolean","INTERSECT",EDGE,{"derivedFrom":[subQ2,makeQuery(id+"F14.opExtrude","SWEPT_FACE",FACE,{"disambiguationData":[OSD([sQuery(id+"F13.wireOp",EDGE,"E98.2.0.1")])]})]}),makeQuery(id+"F14.boolean.opBoolean","INTERSECT",EDGE,{"derivedFrom":[subQ2,makeQuery(id+"F14.opExtrude","SWEPT_FACE",FACE,{"disambiguationData":[OSD([sQuery(id+"F13.wireOp",EDGE,"E98.2.0.3")])]})]}),makeQuery(id+"F14.boolean.opBoolean","INTERSECT",EDGE,{"derivedFrom":[subQ2,makeQuery(id+"F14.opExtrude","SWEPT_FACE",FACE,{"disambiguationData":[OSD([sQuery(id+"F13.wireOp",EDGE,"E98.2.0.4")])]})]}),makeQuery(id+"F14.boolean.opBoolean","INTERSECT",EDGE,{"derivedFrom":[subQ2,makeQuery(id+"F14.opExtrude","SWEPT_FACE",FACE,{"disambiguationData":[OSD([sQuery(id+"F13.wireOp",EDGE,"E98.2.0.5")])]})]}),makeQuery(id+"F14.boolean.opBoolean","INTERSECT",EDGE,{"derivedFrom":[subQ2,makeQuery(id+"F14.opExtrude","SWEPT_FACE",FACE,{"disambiguationData":[OSD([sQuery(id+"F13.wireOp",EDGE,"E98.2.0.6")])]})]}),makeQuery(id+"F14.boolean.opBoolean","INTERSECT",EDGE,{"derivedFrom":[subQ2,makeQuery(id+"F14.opExtrude","SWEPT_FACE",FACE,{"disambiguationData":[OSD([sQuery(id+"F13.wireOp",EDGE,"E98.3.0.0")])]})]}),makeQuery(id+"F14.boolean.opBoolean","INTERSECT",EDGE,{"derivedFrom":[subQ2,makeQuery(id+"F14.opExtrude","SWEPT_FACE",FACE,{"disambiguationData":[OSD([sQuery(id+"F13.wireOp",EDGE,"E98.3.0.1")])]})]}),makeQuery(id+"F14.boolean.opBoolean","INTERSECT",EDGE,{"derivedFrom":[subQ2,makeQuery(id+"F14.opExtrude","SWEPT_FACE",FACE,{"disambiguationData":[OSD([sQuery(id+"F13.wireOp",EDGE,"E98.3.0.3")])]})]}),makeQuery(id+"F14.boolean.opBoolean","INTERSECT",EDGE,{"derivedFrom":[subQ2,makeQuery(id+"F14.opExtrude","SWEPT_FACE",FACE,{"disambiguationData":[OSD([sQuery(id+"F13.wireOp",EDGE,"E98.3.0.4")])]})]}),makeQuery(id+"F14.boolean.opBoolean","INTERSECT",EDGE,{"derivedFrom":[subQ2,makeQuery(id+"F14.opExtrude","SWEPT_FACE",FACE,{"disambiguationData":[OSD([sQuery(id+"F13.wireOp",EDGE,"E98.3.0.5")])]})]}),makeQuery(id+"F14.boolean.opBoolean","INTERSECT",EDGE,{"derivedFrom":[subQ2,makeQuery(id+"F14.opExtrude","SWEPT_FACE",FACE,{"disambiguationData":[OSD([sQuery(id+"F13.wireOp",EDGE,"E98.3.0.6")])]})]})]);}
            var Q54;
            {var subQ0=sQuery(id+"F0.wireOp",EDGE,"E61.top");var subQ2=makeQuery(id+"F4.boolean.opBoolean","MERGE",FACE,{"derivedFrom":[makeQuery(id+"F3.opExtrude","SWEPT_FACE",FACE,{"disambiguationData":[OSD([subQ0]),TDD([makeQuery(id+"F0.imprint","IMPRINT",EDGE,{"disambiguationData":[TD([[makeQuery(id+"F0.imprint","INTERSECT",VERTEX,{"derivedFrom":[subQ0,sQuery(id+"F0.wireOp",EDGE,"E77")]}),-1.0]])],"derivedFrom":subQ0}),makeQuery(id+"F0.imprint","IMPRINT",EDGE,{"disambiguationData":[TD([[makeQuery(id+"F0.imprint","INTERSECT",VERTEX,{"derivedFrom":[subQ0,sQuery(id+"F0.wireOp",EDGE,"E78")]}),1.0]])],"derivedFrom":subQ0})])]}),makeQuery(id+"F3.opExtrude","SWEPT_FACE",FACE,{"disambiguationData":[OSD([subQ0]),TDD([makeQuery(id+"F0.imprint","IMPRINT",EDGE,{"disambiguationData":[TD([[makeQuery(id+"F0.imprint","INTERSECT",VERTEX,{"derivedFrom":[subQ0,sQuery(id+"F0.wireOp",EDGE,"E62")]}),-1.0]])],"derivedFrom":subQ0})])]}),makeQuery(id+"F4.opExtrude","SWEPT_FACE",FACE,{"disambiguationData":[OSD([subQ0])]})]});Q54=qUnion([makeQuery(id+"F14.boolean.opBoolean","INTERSECT",EDGE,{"derivedFrom":[subQ2,makeQuery(id+"F14.opExtrude","SWEPT_FACE",FACE,{"disambiguationData":[OSD([sQuery(id+"F13.wireOp",EDGE,"E89")])]})]}),makeQuery(id+"F14.boolean.opBoolean","INTERSECT",EDGE,{"derivedFrom":[subQ2,makeQuery(id+"F14.opExtrude","SWEPT_FACE",FACE,{"disambiguationData":[OSD([sQuery(id+"F13.wireOp",EDGE,"E90")])]})]}),makeQuery(id+"F14.boolean.opBoolean","INTERSECT",EDGE,{"derivedFrom":[subQ2,makeQuery(id+"F14.opExtrude","SWEPT_FACE",FACE,{"disambiguationData":[OSD([sQuery(id+"F13.wireOp",EDGE,"E92")])]})]}),makeQuery(id+"F14.boolean.opBoolean","INTERSECT",EDGE,{"derivedFrom":[subQ2,makeQuery(id+"F14.opExtrude","SWEPT_FACE",FACE,{"disambiguationData":[OSD([sQuery(id+"F13.wireOp",EDGE,"E93")])]})]}),makeQuery(id+"F14.boolean.opBoolean","INTERSECT",EDGE,{"derivedFrom":[subQ2,makeQuery(id+"F14.opExtrude","SWEPT_FACE",FACE,{"disambiguationData":[OSD([sQuery(id+"F13.wireOp",EDGE,"E96")])]})]}),makeQuery(id+"F14.boolean.opBoolean","INTERSECT",EDGE,{"derivedFrom":[subQ2,makeQuery(id+"F14.opExtrude","SWEPT_FACE",FACE,{"disambiguationData":[OSD([sQuery(id+"F13.wireOp",EDGE,"E97")])]})]}),makeQuery(id+"F14.boolean.opBoolean","INTERSECT",EDGE,{"derivedFrom":[subQ2,makeQuery(id+"F14.opExtrude","SWEPT_FACE",FACE,{"disambiguationData":[OSD([sQuery(id+"F13.wireOp",EDGE,"E98.1.0.0")])]})]}),makeQuery(id+"F14.boolean.opBoolean","INTERSECT",EDGE,{"derivedFrom":[subQ2,makeQuery(id+"F14.opExtrude","SWEPT_FACE",FACE,{"disambiguationData":[OSD([sQuery(id+"F13.wireOp",EDGE,"E98.1.0.1")])]})]}),makeQuery(id+"F14.boolean.opBoolean","INTERSECT",EDGE,{"derivedFrom":[subQ2,makeQuery(id+"F14.opExtrude","SWEPT_FACE",FACE,{"disambiguationData":[OSD([sQuery(id+"F13.wireOp",EDGE,"E98.1.0.3")])]})]}),makeQuery(id+"F14.boolean.opBoolean","INTERSECT",EDGE,{"derivedFrom":[subQ2,makeQuery(id+"F14.opExtrude","SWEPT_FACE",FACE,{"disambiguationData":[OSD([sQuery(id+"F13.wireOp",EDGE,"E98.1.0.4")])]})]}),makeQuery(id+"F14.boolean.opBoolean","INTERSECT",EDGE,{"derivedFrom":[subQ2,makeQuery(id+"F14.opExtrude","SWEPT_FACE",FACE,{"disambiguationData":[OSD([sQuery(id+"F13.wireOp",EDGE,"E98.1.0.5")])]})]}),makeQuery(id+"F14.boolean.opBoolean","INTERSECT",EDGE,{"derivedFrom":[subQ2,makeQuery(id+"F14.opExtrude","SWEPT_FACE",FACE,{"disambiguationData":[OSD([sQuery(id+"F13.wireOp",EDGE,"E98.1.0.6")])]})]}),makeQuery(id+"F14.boolean.opBoolean","INTERSECT",EDGE,{"derivedFrom":[subQ2,makeQuery(id+"F14.opExtrude","SWEPT_FACE",FACE,{"disambiguationData":[OSD([sQuery(id+"F13.wireOp",EDGE,"E98.2.0.0")])]})]}),makeQuery(id+"F14.boolean.opBoolean","INTERSECT",EDGE,{"derivedFrom":[subQ2,makeQuery(id+"F14.opExtrude","SWEPT_FACE",FACE,{"disambiguationData":[OSD([sQuery(id+"F13.wireOp",EDGE,"E98.2.0.1")])]})]}),makeQuery(id+"F14.boolean.opBoolean","INTERSECT",EDGE,{"derivedFrom":[subQ2,makeQuery(id+"F14.opExtrude","SWEPT_FACE",FACE,{"disambiguationData":[OSD([sQuery(id+"F13.wireOp",EDGE,"E98.2.0.3")])]})]}),makeQuery(id+"F14.boolean.opBoolean","INTERSECT",EDGE,{"derivedFrom":[subQ2,makeQuery(id+"F14.opExtrude","SWEPT_FACE",FACE,{"disambiguationData":[OSD([sQuery(id+"F13.wireOp",EDGE,"E98.2.0.4")])]})]}),makeQuery(id+"F14.boolean.opBoolean","INTERSECT",EDGE,{"derivedFrom":[subQ2,makeQuery(id+"F14.opExtrude","SWEPT_FACE",FACE,{"disambiguationData":[OSD([sQuery(id+"F13.wireOp",EDGE,"E98.2.0.5")])]})]}),makeQuery(id+"F14.boolean.opBoolean","INTERSECT",EDGE,{"derivedFrom":[subQ2,makeQuery(id+"F14.opExtrude","SWEPT_FACE",FACE,{"disambiguationData":[OSD([sQuery(id+"F13.wireOp",EDGE,"E98.2.0.6")])]})]}),makeQuery(id+"F14.boolean.opBoolean","INTERSECT",EDGE,{"derivedFrom":[subQ2,makeQuery(id+"F14.opExtrude","SWEPT_FACE",FACE,{"disambiguationData":[OSD([sQuery(id+"F13.wireOp",EDGE,"E98.3.0.0")])]})]}),makeQuery(id+"F14.boolean.opBoolean","INTERSECT",EDGE,{"derivedFrom":[subQ2,makeQuery(id+"F14.opExtrude","SWEPT_FACE",FACE,{"disambiguationData":[OSD([sQuery(id+"F13.wireOp",EDGE,"E98.3.0.1")])]})]}),makeQuery(id+"F14.boolean.opBoolean","INTERSECT",EDGE,{"derivedFrom":[subQ2,makeQuery(id+"F14.opExtrude","SWEPT_FACE",FACE,{"disambiguationData":[OSD([sQuery(id+"F13.wireOp",EDGE,"E98.3.0.3")])]})]}),makeQuery(id+"F14.boolean.opBoolean","INTERSECT",EDGE,{"derivedFrom":[subQ2,makeQuery(id+"F14.opExtrude","SWEPT_FACE",FACE,{"disambiguationData":[OSD([sQuery(id+"F13.wireOp",EDGE,"E98.3.0.4")])]})]}),makeQuery(id+"F14.boolean.opBoolean","INTERSECT",EDGE,{"derivedFrom":[subQ2,makeQuery(id+"F14.opExtrude","SWEPT_FACE",FACE,{"disambiguationData":[OSD([sQuery(id+"F13.wireOp",EDGE,"E98.3.0.5")])]})]}),makeQuery(id+"F14.boolean.opBoolean","INTERSECT",EDGE,{"derivedFrom":[subQ2,makeQuery(id+"F14.opExtrude","SWEPT_FACE",FACE,{"disambiguationData":[OSD([sQuery(id+"F13.wireOp",EDGE,"E98.3.0.6")])]})]})]);}
            var Q55;
            {var subQ0=sQuery(id+"F0.wireOp",EDGE,"E61.top");var subQ2=makeQuery(id+"F4.boolean.opBoolean","MERGE",FACE,{"derivedFrom":[makeQuery(id+"F3.opExtrude","SWEPT_FACE",FACE,{"disambiguationData":[OSD([subQ0]),TDD([makeQuery(id+"F0.imprint","IMPRINT",EDGE,{"disambiguationData":[TD([[makeQuery(id+"F0.imprint","INTERSECT",VERTEX,{"derivedFrom":[subQ0,sQuery(id+"F0.wireOp",EDGE,"E77")]}),-1.0]])],"derivedFrom":subQ0}),makeQuery(id+"F0.imprint","IMPRINT",EDGE,{"disambiguationData":[TD([[makeQuery(id+"F0.imprint","INTERSECT",VERTEX,{"derivedFrom":[subQ0,sQuery(id+"F0.wireOp",EDGE,"E78")]}),1.0]])],"derivedFrom":subQ0})])]}),makeQuery(id+"F3.opExtrude","SWEPT_FACE",FACE,{"disambiguationData":[OSD([subQ0]),TDD([makeQuery(id+"F0.imprint","IMPRINT",EDGE,{"disambiguationData":[TD([[makeQuery(id+"F0.imprint","INTERSECT",VERTEX,{"derivedFrom":[subQ0,sQuery(id+"F0.wireOp",EDGE,"E62")]}),-1.0]])],"derivedFrom":subQ0})])]}),makeQuery(id+"F4.opExtrude","SWEPT_FACE",FACE,{"disambiguationData":[OSD([subQ0])]})]});Q55=qUnion([makeQuery(id+"F14.boolean.opBoolean","INTERSECT",EDGE,{"derivedFrom":[subQ2,makeQuery(id+"F14.opExtrude","SWEPT_FACE",FACE,{"disambiguationData":[OSD([sQuery(id+"F13.wireOp",EDGE,"E89")])]})]}),makeQuery(id+"F14.boolean.opBoolean","INTERSECT",EDGE,{"derivedFrom":[subQ2,makeQuery(id+"F14.opExtrude","SWEPT_FACE",FACE,{"disambiguationData":[OSD([sQuery(id+"F13.wireOp",EDGE,"E90")])]})]}),makeQuery(id+"F14.boolean.opBoolean","INTERSECT",EDGE,{"derivedFrom":[subQ2,makeQuery(id+"F14.opExtrude","SWEPT_FACE",FACE,{"disambiguationData":[OSD([sQuery(id+"F13.wireOp",EDGE,"E92")])]})]}),makeQuery(id+"F14.boolean.opBoolean","INTERSECT",EDGE,{"derivedFrom":[subQ2,makeQuery(id+"F14.opExtrude","SWEPT_FACE",FACE,{"disambiguationData":[OSD([sQuery(id+"F13.wireOp",EDGE,"E93")])]})]}),makeQuery(id+"F14.boolean.opBoolean","INTERSECT",EDGE,{"derivedFrom":[subQ2,makeQuery(id+"F14.opExtrude","SWEPT_FACE",FACE,{"disambiguationData":[OSD([sQuery(id+"F13.wireOp",EDGE,"E96")])]})]}),makeQuery(id+"F14.boolean.opBoolean","INTERSECT",EDGE,{"derivedFrom":[subQ2,makeQuery(id+"F14.opExtrude","SWEPT_FACE",FACE,{"disambiguationData":[OSD([sQuery(id+"F13.wireOp",EDGE,"E97")])]})]}),makeQuery(id+"F14.boolean.opBoolean","INTERSECT",EDGE,{"derivedFrom":[subQ2,makeQuery(id+"F14.opExtrude","SWEPT_FACE",FACE,{"disambiguationData":[OSD([sQuery(id+"F13.wireOp",EDGE,"E98.1.0.0")])]})]}),makeQuery(id+"F14.boolean.opBoolean","INTERSECT",EDGE,{"derivedFrom":[subQ2,makeQuery(id+"F14.opExtrude","SWEPT_FACE",FACE,{"disambiguationData":[OSD([sQuery(id+"F13.wireOp",EDGE,"E98.1.0.1")])]})]}),makeQuery(id+"F14.boolean.opBoolean","INTERSECT",EDGE,{"derivedFrom":[subQ2,makeQuery(id+"F14.opExtrude","SWEPT_FACE",FACE,{"disambiguationData":[OSD([sQuery(id+"F13.wireOp",EDGE,"E98.1.0.3")])]})]}),makeQuery(id+"F14.boolean.opBoolean","INTERSECT",EDGE,{"derivedFrom":[subQ2,makeQuery(id+"F14.opExtrude","SWEPT_FACE",FACE,{"disambiguationData":[OSD([sQuery(id+"F13.wireOp",EDGE,"E98.1.0.4")])]})]}),makeQuery(id+"F14.boolean.opBoolean","INTERSECT",EDGE,{"derivedFrom":[subQ2,makeQuery(id+"F14.opExtrude","SWEPT_FACE",FACE,{"disambiguationData":[OSD([sQuery(id+"F13.wireOp",EDGE,"E98.1.0.5")])]})]}),makeQuery(id+"F14.boolean.opBoolean","INTERSECT",EDGE,{"derivedFrom":[subQ2,makeQuery(id+"F14.opExtrude","SWEPT_FACE",FACE,{"disambiguationData":[OSD([sQuery(id+"F13.wireOp",EDGE,"E98.1.0.6")])]})]}),makeQuery(id+"F14.boolean.opBoolean","INTERSECT",EDGE,{"derivedFrom":[subQ2,makeQuery(id+"F14.opExtrude","SWEPT_FACE",FACE,{"disambiguationData":[OSD([sQuery(id+"F13.wireOp",EDGE,"E98.2.0.0")])]})]}),makeQuery(id+"F14.boolean.opBoolean","INTERSECT",EDGE,{"derivedFrom":[subQ2,makeQuery(id+"F14.opExtrude","SWEPT_FACE",FACE,{"disambiguationData":[OSD([sQuery(id+"F13.wireOp",EDGE,"E98.2.0.1")])]})]}),makeQuery(id+"F14.boolean.opBoolean","INTERSECT",EDGE,{"derivedFrom":[subQ2,makeQuery(id+"F14.opExtrude","SWEPT_FACE",FACE,{"disambiguationData":[OSD([sQuery(id+"F13.wireOp",EDGE,"E98.2.0.3")])]})]}),makeQuery(id+"F14.boolean.opBoolean","INTERSECT",EDGE,{"derivedFrom":[subQ2,makeQuery(id+"F14.opExtrude","SWEPT_FACE",FACE,{"disambiguationData":[OSD([sQuery(id+"F13.wireOp",EDGE,"E98.2.0.4")])]})]}),makeQuery(id+"F14.boolean.opBoolean","INTERSECT",EDGE,{"derivedFrom":[subQ2,makeQuery(id+"F14.opExtrude","SWEPT_FACE",FACE,{"disambiguationData":[OSD([sQuery(id+"F13.wireOp",EDGE,"E98.2.0.5")])]})]}),makeQuery(id+"F14.boolean.opBoolean","INTERSECT",EDGE,{"derivedFrom":[subQ2,makeQuery(id+"F14.opExtrude","SWEPT_FACE",FACE,{"disambiguationData":[OSD([sQuery(id+"F13.wireOp",EDGE,"E98.2.0.6")])]})]}),makeQuery(id+"F14.boolean.opBoolean","INTERSECT",EDGE,{"derivedFrom":[subQ2,makeQuery(id+"F14.opExtrude","SWEPT_FACE",FACE,{"disambiguationData":[OSD([sQuery(id+"F13.wireOp",EDGE,"E98.3.0.0")])]})]}),makeQuery(id+"F14.boolean.opBoolean","INTERSECT",EDGE,{"derivedFrom":[subQ2,makeQuery(id+"F14.opExtrude","SWEPT_FACE",FACE,{"disambiguationData":[OSD([sQuery(id+"F13.wireOp",EDGE,"E98.3.0.1")])]})]}),makeQuery(id+"F14.boolean.opBoolean","INTERSECT",EDGE,{"derivedFrom":[subQ2,makeQuery(id+"F14.opExtrude","SWEPT_FACE",FACE,{"disambiguationData":[OSD([sQuery(id+"F13.wireOp",EDGE,"E98.3.0.3")])]})]}),makeQuery(id+"F14.boolean.opBoolean","INTERSECT",EDGE,{"derivedFrom":[subQ2,makeQuery(id+"F14.opExtrude","SWEPT_FACE",FACE,{"disambiguationData":[OSD([sQuery(id+"F13.wireOp",EDGE,"E98.3.0.4")])]})]}),makeQuery(id+"F14.boolean.opBoolean","INTERSECT",EDGE,{"derivedFrom":[subQ2,makeQuery(id+"F14.opExtrude","SWEPT_FACE",FACE,{"disambiguationData":[OSD([sQuery(id+"F13.wireOp",EDGE,"E98.3.0.5")])]})]}),makeQuery(id+"F14.boolean.opBoolean","INTERSECT",EDGE,{"derivedFrom":[subQ2,makeQuery(id+"F14.opExtrude","SWEPT_FACE",FACE,{"disambiguationData":[OSD([sQuery(id+"F13.wireOp",EDGE,"E98.3.0.6")])]})]})]);}
            var Q56;
            {var subQ0=sQuery(id+"F0.wireOp",EDGE,"E61.top");var subQ2=makeQuery(id+"F4.boolean.opBoolean","MERGE",FACE,{"derivedFrom":[makeQuery(id+"F3.opExtrude","SWEPT_FACE",FACE,{"disambiguationData":[OSD([subQ0]),TDD([makeQuery(id+"F0.imprint","IMPRINT",EDGE,{"disambiguationData":[TD([[makeQuery(id+"F0.imprint","INTERSECT",VERTEX,{"derivedFrom":[subQ0,sQuery(id+"F0.wireOp",EDGE,"E77")]}),-1.0]])],"derivedFrom":subQ0}),makeQuery(id+"F0.imprint","IMPRINT",EDGE,{"disambiguationData":[TD([[makeQuery(id+"F0.imprint","INTERSECT",VERTEX,{"derivedFrom":[subQ0,sQuery(id+"F0.wireOp",EDGE,"E78")]}),1.0]])],"derivedFrom":subQ0})])]}),makeQuery(id+"F3.opExtrude","SWEPT_FACE",FACE,{"disambiguationData":[OSD([subQ0]),TDD([makeQuery(id+"F0.imprint","IMPRINT",EDGE,{"disambiguationData":[TD([[makeQuery(id+"F0.imprint","INTERSECT",VERTEX,{"derivedFrom":[subQ0,sQuery(id+"F0.wireOp",EDGE,"E62")]}),-1.0]])],"derivedFrom":subQ0})])]}),makeQuery(id+"F4.opExtrude","SWEPT_FACE",FACE,{"disambiguationData":[OSD([subQ0])]})]});Q56=qUnion([makeQuery(id+"F14.boolean.opBoolean","INTERSECT",EDGE,{"derivedFrom":[subQ2,makeQuery(id+"F14.opExtrude","SWEPT_FACE",FACE,{"disambiguationData":[OSD([sQuery(id+"F13.wireOp",EDGE,"E89")])]})]}),makeQuery(id+"F14.boolean.opBoolean","INTERSECT",EDGE,{"derivedFrom":[subQ2,makeQuery(id+"F14.opExtrude","SWEPT_FACE",FACE,{"disambiguationData":[OSD([sQuery(id+"F13.wireOp",EDGE,"E90")])]})]}),makeQuery(id+"F14.boolean.opBoolean","INTERSECT",EDGE,{"derivedFrom":[subQ2,makeQuery(id+"F14.opExtrude","SWEPT_FACE",FACE,{"disambiguationData":[OSD([sQuery(id+"F13.wireOp",EDGE,"E92")])]})]}),makeQuery(id+"F14.boolean.opBoolean","INTERSECT",EDGE,{"derivedFrom":[subQ2,makeQuery(id+"F14.opExtrude","SWEPT_FACE",FACE,{"disambiguationData":[OSD([sQuery(id+"F13.wireOp",EDGE,"E93")])]})]}),makeQuery(id+"F14.boolean.opBoolean","INTERSECT",EDGE,{"derivedFrom":[subQ2,makeQuery(id+"F14.opExtrude","SWEPT_FACE",FACE,{"disambiguationData":[OSD([sQuery(id+"F13.wireOp",EDGE,"E96")])]})]}),makeQuery(id+"F14.boolean.opBoolean","INTERSECT",EDGE,{"derivedFrom":[subQ2,makeQuery(id+"F14.opExtrude","SWEPT_FACE",FACE,{"disambiguationData":[OSD([sQuery(id+"F13.wireOp",EDGE,"E97")])]})]}),makeQuery(id+"F14.boolean.opBoolean","INTERSECT",EDGE,{"derivedFrom":[subQ2,makeQuery(id+"F14.opExtrude","SWEPT_FACE",FACE,{"disambiguationData":[OSD([sQuery(id+"F13.wireOp",EDGE,"E98.1.0.0")])]})]}),makeQuery(id+"F14.boolean.opBoolean","INTERSECT",EDGE,{"derivedFrom":[subQ2,makeQuery(id+"F14.opExtrude","SWEPT_FACE",FACE,{"disambiguationData":[OSD([sQuery(id+"F13.wireOp",EDGE,"E98.1.0.1")])]})]}),makeQuery(id+"F14.boolean.opBoolean","INTERSECT",EDGE,{"derivedFrom":[subQ2,makeQuery(id+"F14.opExtrude","SWEPT_FACE",FACE,{"disambiguationData":[OSD([sQuery(id+"F13.wireOp",EDGE,"E98.1.0.3")])]})]}),makeQuery(id+"F14.boolean.opBoolean","INTERSECT",EDGE,{"derivedFrom":[subQ2,makeQuery(id+"F14.opExtrude","SWEPT_FACE",FACE,{"disambiguationData":[OSD([sQuery(id+"F13.wireOp",EDGE,"E98.1.0.4")])]})]}),makeQuery(id+"F14.boolean.opBoolean","INTERSECT",EDGE,{"derivedFrom":[subQ2,makeQuery(id+"F14.opExtrude","SWEPT_FACE",FACE,{"disambiguationData":[OSD([sQuery(id+"F13.wireOp",EDGE,"E98.1.0.5")])]})]}),makeQuery(id+"F14.boolean.opBoolean","INTERSECT",EDGE,{"derivedFrom":[subQ2,makeQuery(id+"F14.opExtrude","SWEPT_FACE",FACE,{"disambiguationData":[OSD([sQuery(id+"F13.wireOp",EDGE,"E98.1.0.6")])]})]}),makeQuery(id+"F14.boolean.opBoolean","INTERSECT",EDGE,{"derivedFrom":[subQ2,makeQuery(id+"F14.opExtrude","SWEPT_FACE",FACE,{"disambiguationData":[OSD([sQuery(id+"F13.wireOp",EDGE,"E98.2.0.0")])]})]}),makeQuery(id+"F14.boolean.opBoolean","INTERSECT",EDGE,{"derivedFrom":[subQ2,makeQuery(id+"F14.opExtrude","SWEPT_FACE",FACE,{"disambiguationData":[OSD([sQuery(id+"F13.wireOp",EDGE,"E98.2.0.1")])]})]}),makeQuery(id+"F14.boolean.opBoolean","INTERSECT",EDGE,{"derivedFrom":[subQ2,makeQuery(id+"F14.opExtrude","SWEPT_FACE",FACE,{"disambiguationData":[OSD([sQuery(id+"F13.wireOp",EDGE,"E98.2.0.3")])]})]}),makeQuery(id+"F14.boolean.opBoolean","INTERSECT",EDGE,{"derivedFrom":[subQ2,makeQuery(id+"F14.opExtrude","SWEPT_FACE",FACE,{"disambiguationData":[OSD([sQuery(id+"F13.wireOp",EDGE,"E98.2.0.4")])]})]}),makeQuery(id+"F14.boolean.opBoolean","INTERSECT",EDGE,{"derivedFrom":[subQ2,makeQuery(id+"F14.opExtrude","SWEPT_FACE",FACE,{"disambiguationData":[OSD([sQuery(id+"F13.wireOp",EDGE,"E98.2.0.5")])]})]}),makeQuery(id+"F14.boolean.opBoolean","INTERSECT",EDGE,{"derivedFrom":[subQ2,makeQuery(id+"F14.opExtrude","SWEPT_FACE",FACE,{"disambiguationData":[OSD([sQuery(id+"F13.wireOp",EDGE,"E98.2.0.6")])]})]}),makeQuery(id+"F14.boolean.opBoolean","INTERSECT",EDGE,{"derivedFrom":[subQ2,makeQuery(id+"F14.opExtrude","SWEPT_FACE",FACE,{"disambiguationData":[OSD([sQuery(id+"F13.wireOp",EDGE,"E98.3.0.0")])]})]}),makeQuery(id+"F14.boolean.opBoolean","INTERSECT",EDGE,{"derivedFrom":[subQ2,makeQuery(id+"F14.opExtrude","SWEPT_FACE",FACE,{"disambiguationData":[OSD([sQuery(id+"F13.wireOp",EDGE,"E98.3.0.1")])]})]}),makeQuery(id+"F14.boolean.opBoolean","INTERSECT",EDGE,{"derivedFrom":[subQ2,makeQuery(id+"F14.opExtrude","SWEPT_FACE",FACE,{"disambiguationData":[OSD([sQuery(id+"F13.wireOp",EDGE,"E98.3.0.3")])]})]}),makeQuery(id+"F14.boolean.opBoolean","INTERSECT",EDGE,{"derivedFrom":[subQ2,makeQuery(id+"F14.opExtrude","SWEPT_FACE",FACE,{"disambiguationData":[OSD([sQuery(id+"F13.wireOp",EDGE,"E98.3.0.4")])]})]}),makeQuery(id+"F14.boolean.opBoolean","INTERSECT",EDGE,{"derivedFrom":[subQ2,makeQuery(id+"F14.opExtrude","SWEPT_FACE",FACE,{"disambiguationData":[OSD([sQuery(id+"F13.wireOp",EDGE,"E98.3.0.5")])]})]}),makeQuery(id+"F14.boolean.opBoolean","INTERSECT",EDGE,{"derivedFrom":[subQ2,makeQuery(id+"F14.opExtrude","SWEPT_FACE",FACE,{"disambiguationData":[OSD([sQuery(id+"F13.wireOp",EDGE,"E98.3.0.6")])]})]})]);}
            var Q57;
            {var subQ0=sQuery(id+"F0.wireOp",EDGE,"E61.top");var subQ2=makeQuery(id+"F4.boolean.opBoolean","MERGE",FACE,{"derivedFrom":[makeQuery(id+"F3.opExtrude","SWEPT_FACE",FACE,{"disambiguationData":[OSD([subQ0]),TDD([makeQuery(id+"F0.imprint","IMPRINT",EDGE,{"disambiguationData":[TD([[makeQuery(id+"F0.imprint","INTERSECT",VERTEX,{"derivedFrom":[subQ0,sQuery(id+"F0.wireOp",EDGE,"E77")]}),-1.0]])],"derivedFrom":subQ0}),makeQuery(id+"F0.imprint","IMPRINT",EDGE,{"disambiguationData":[TD([[makeQuery(id+"F0.imprint","INTERSECT",VERTEX,{"derivedFrom":[subQ0,sQuery(id+"F0.wireOp",EDGE,"E78")]}),1.0]])],"derivedFrom":subQ0})])]}),makeQuery(id+"F3.opExtrude","SWEPT_FACE",FACE,{"disambiguationData":[OSD([subQ0]),TDD([makeQuery(id+"F0.imprint","IMPRINT",EDGE,{"disambiguationData":[TD([[makeQuery(id+"F0.imprint","INTERSECT",VERTEX,{"derivedFrom":[subQ0,sQuery(id+"F0.wireOp",EDGE,"E62")]}),-1.0]])],"derivedFrom":subQ0})])]}),makeQuery(id+"F4.opExtrude","SWEPT_FACE",FACE,{"disambiguationData":[OSD([subQ0])]})]});Q57=qUnion([makeQuery(id+"F14.boolean.opBoolean","INTERSECT",EDGE,{"derivedFrom":[subQ2,makeQuery(id+"F14.opExtrude","SWEPT_FACE",FACE,{"disambiguationData":[OSD([sQuery(id+"F13.wireOp",EDGE,"E89")])]})]}),makeQuery(id+"F14.boolean.opBoolean","INTERSECT",EDGE,{"derivedFrom":[subQ2,makeQuery(id+"F14.opExtrude","SWEPT_FACE",FACE,{"disambiguationData":[OSD([sQuery(id+"F13.wireOp",EDGE,"E90")])]})]}),makeQuery(id+"F14.boolean.opBoolean","INTERSECT",EDGE,{"derivedFrom":[subQ2,makeQuery(id+"F14.opExtrude","SWEPT_FACE",FACE,{"disambiguationData":[OSD([sQuery(id+"F13.wireOp",EDGE,"E92")])]})]}),makeQuery(id+"F14.boolean.opBoolean","INTERSECT",EDGE,{"derivedFrom":[subQ2,makeQuery(id+"F14.opExtrude","SWEPT_FACE",FACE,{"disambiguationData":[OSD([sQuery(id+"F13.wireOp",EDGE,"E93")])]})]}),makeQuery(id+"F14.boolean.opBoolean","INTERSECT",EDGE,{"derivedFrom":[subQ2,makeQuery(id+"F14.opExtrude","SWEPT_FACE",FACE,{"disambiguationData":[OSD([sQuery(id+"F13.wireOp",EDGE,"E96")])]})]}),makeQuery(id+"F14.boolean.opBoolean","INTERSECT",EDGE,{"derivedFrom":[subQ2,makeQuery(id+"F14.opExtrude","SWEPT_FACE",FACE,{"disambiguationData":[OSD([sQuery(id+"F13.wireOp",EDGE,"E97")])]})]}),makeQuery(id+"F14.boolean.opBoolean","INTERSECT",EDGE,{"derivedFrom":[subQ2,makeQuery(id+"F14.opExtrude","SWEPT_FACE",FACE,{"disambiguationData":[OSD([sQuery(id+"F13.wireOp",EDGE,"E98.1.0.0")])]})]}),makeQuery(id+"F14.boolean.opBoolean","INTERSECT",EDGE,{"derivedFrom":[subQ2,makeQuery(id+"F14.opExtrude","SWEPT_FACE",FACE,{"disambiguationData":[OSD([sQuery(id+"F13.wireOp",EDGE,"E98.1.0.1")])]})]}),makeQuery(id+"F14.boolean.opBoolean","INTERSECT",EDGE,{"derivedFrom":[subQ2,makeQuery(id+"F14.opExtrude","SWEPT_FACE",FACE,{"disambiguationData":[OSD([sQuery(id+"F13.wireOp",EDGE,"E98.1.0.3")])]})]}),makeQuery(id+"F14.boolean.opBoolean","INTERSECT",EDGE,{"derivedFrom":[subQ2,makeQuery(id+"F14.opExtrude","SWEPT_FACE",FACE,{"disambiguationData":[OSD([sQuery(id+"F13.wireOp",EDGE,"E98.1.0.4")])]})]}),makeQuery(id+"F14.boolean.opBoolean","INTERSECT",EDGE,{"derivedFrom":[subQ2,makeQuery(id+"F14.opExtrude","SWEPT_FACE",FACE,{"disambiguationData":[OSD([sQuery(id+"F13.wireOp",EDGE,"E98.1.0.5")])]})]}),makeQuery(id+"F14.boolean.opBoolean","INTERSECT",EDGE,{"derivedFrom":[subQ2,makeQuery(id+"F14.opExtrude","SWEPT_FACE",FACE,{"disambiguationData":[OSD([sQuery(id+"F13.wireOp",EDGE,"E98.1.0.6")])]})]}),makeQuery(id+"F14.boolean.opBoolean","INTERSECT",EDGE,{"derivedFrom":[subQ2,makeQuery(id+"F14.opExtrude","SWEPT_FACE",FACE,{"disambiguationData":[OSD([sQuery(id+"F13.wireOp",EDGE,"E98.2.0.0")])]})]}),makeQuery(id+"F14.boolean.opBoolean","INTERSECT",EDGE,{"derivedFrom":[subQ2,makeQuery(id+"F14.opExtrude","SWEPT_FACE",FACE,{"disambiguationData":[OSD([sQuery(id+"F13.wireOp",EDGE,"E98.2.0.1")])]})]}),makeQuery(id+"F14.boolean.opBoolean","INTERSECT",EDGE,{"derivedFrom":[subQ2,makeQuery(id+"F14.opExtrude","SWEPT_FACE",FACE,{"disambiguationData":[OSD([sQuery(id+"F13.wireOp",EDGE,"E98.2.0.3")])]})]}),makeQuery(id+"F14.boolean.opBoolean","INTERSECT",EDGE,{"derivedFrom":[subQ2,makeQuery(id+"F14.opExtrude","SWEPT_FACE",FACE,{"disambiguationData":[OSD([sQuery(id+"F13.wireOp",EDGE,"E98.2.0.4")])]})]}),makeQuery(id+"F14.boolean.opBoolean","INTERSECT",EDGE,{"derivedFrom":[subQ2,makeQuery(id+"F14.opExtrude","SWEPT_FACE",FACE,{"disambiguationData":[OSD([sQuery(id+"F13.wireOp",EDGE,"E98.2.0.5")])]})]}),makeQuery(id+"F14.boolean.opBoolean","INTERSECT",EDGE,{"derivedFrom":[subQ2,makeQuery(id+"F14.opExtrude","SWEPT_FACE",FACE,{"disambiguationData":[OSD([sQuery(id+"F13.wireOp",EDGE,"E98.2.0.6")])]})]}),makeQuery(id+"F14.boolean.opBoolean","INTERSECT",EDGE,{"derivedFrom":[subQ2,makeQuery(id+"F14.opExtrude","SWEPT_FACE",FACE,{"disambiguationData":[OSD([sQuery(id+"F13.wireOp",EDGE,"E98.3.0.0")])]})]}),makeQuery(id+"F14.boolean.opBoolean","INTERSECT",EDGE,{"derivedFrom":[subQ2,makeQuery(id+"F14.opExtrude","SWEPT_FACE",FACE,{"disambiguationData":[OSD([sQuery(id+"F13.wireOp",EDGE,"E98.3.0.1")])]})]}),makeQuery(id+"F14.boolean.opBoolean","INTERSECT",EDGE,{"derivedFrom":[subQ2,makeQuery(id+"F14.opExtrude","SWEPT_FACE",FACE,{"disambiguationData":[OSD([sQuery(id+"F13.wireOp",EDGE,"E98.3.0.3")])]})]}),makeQuery(id+"F14.boolean.opBoolean","INTERSECT",EDGE,{"derivedFrom":[subQ2,makeQuery(id+"F14.opExtrude","SWEPT_FACE",FACE,{"disambiguationData":[OSD([sQuery(id+"F13.wireOp",EDGE,"E98.3.0.4")])]})]}),makeQuery(id+"F14.boolean.opBoolean","INTERSECT",EDGE,{"derivedFrom":[subQ2,makeQuery(id+"F14.opExtrude","SWEPT_FACE",FACE,{"disambiguationData":[OSD([sQuery(id+"F13.wireOp",EDGE,"E98.3.0.5")])]})]}),makeQuery(id+"F14.boolean.opBoolean","INTERSECT",EDGE,{"derivedFrom":[subQ2,makeQuery(id+"F14.opExtrude","SWEPT_FACE",FACE,{"disambiguationData":[OSD([sQuery(id+"F13.wireOp",EDGE,"E98.3.0.6")])]})]})]);}
            var Q58;
            {var subQ0=sQuery(id+"F0.wireOp",EDGE,"E61.top");var subQ2=makeQuery(id+"F4.boolean.opBoolean","MERGE",FACE,{"derivedFrom":[makeQuery(id+"F3.opExtrude","SWEPT_FACE",FACE,{"disambiguationData":[OSD([subQ0]),TDD([makeQuery(id+"F0.imprint","IMPRINT",EDGE,{"disambiguationData":[TD([[makeQuery(id+"F0.imprint","INTERSECT",VERTEX,{"derivedFrom":[subQ0,sQuery(id+"F0.wireOp",EDGE,"E77")]}),-1.0]])],"derivedFrom":subQ0}),makeQuery(id+"F0.imprint","IMPRINT",EDGE,{"disambiguationData":[TD([[makeQuery(id+"F0.imprint","INTERSECT",VERTEX,{"derivedFrom":[subQ0,sQuery(id+"F0.wireOp",EDGE,"E78")]}),1.0]])],"derivedFrom":subQ0})])]}),makeQuery(id+"F3.opExtrude","SWEPT_FACE",FACE,{"disambiguationData":[OSD([subQ0]),TDD([makeQuery(id+"F0.imprint","IMPRINT",EDGE,{"disambiguationData":[TD([[makeQuery(id+"F0.imprint","INTERSECT",VERTEX,{"derivedFrom":[subQ0,sQuery(id+"F0.wireOp",EDGE,"E62")]}),-1.0]])],"derivedFrom":subQ0})])]}),makeQuery(id+"F4.opExtrude","SWEPT_FACE",FACE,{"disambiguationData":[OSD([subQ0])]})]});Q58=qUnion([makeQuery(id+"F14.boolean.opBoolean","INTERSECT",EDGE,{"derivedFrom":[subQ2,makeQuery(id+"F14.opExtrude","SWEPT_FACE",FACE,{"disambiguationData":[OSD([sQuery(id+"F13.wireOp",EDGE,"E89")])]})]}),makeQuery(id+"F14.boolean.opBoolean","INTERSECT",EDGE,{"derivedFrom":[subQ2,makeQuery(id+"F14.opExtrude","SWEPT_FACE",FACE,{"disambiguationData":[OSD([sQuery(id+"F13.wireOp",EDGE,"E90")])]})]}),makeQuery(id+"F14.boolean.opBoolean","INTERSECT",EDGE,{"derivedFrom":[subQ2,makeQuery(id+"F14.opExtrude","SWEPT_FACE",FACE,{"disambiguationData":[OSD([sQuery(id+"F13.wireOp",EDGE,"E92")])]})]}),makeQuery(id+"F14.boolean.opBoolean","INTERSECT",EDGE,{"derivedFrom":[subQ2,makeQuery(id+"F14.opExtrude","SWEPT_FACE",FACE,{"disambiguationData":[OSD([sQuery(id+"F13.wireOp",EDGE,"E93")])]})]}),makeQuery(id+"F14.boolean.opBoolean","INTERSECT",EDGE,{"derivedFrom":[subQ2,makeQuery(id+"F14.opExtrude","SWEPT_FACE",FACE,{"disambiguationData":[OSD([sQuery(id+"F13.wireOp",EDGE,"E96")])]})]}),makeQuery(id+"F14.boolean.opBoolean","INTERSECT",EDGE,{"derivedFrom":[subQ2,makeQuery(id+"F14.opExtrude","SWEPT_FACE",FACE,{"disambiguationData":[OSD([sQuery(id+"F13.wireOp",EDGE,"E97")])]})]}),makeQuery(id+"F14.boolean.opBoolean","INTERSECT",EDGE,{"derivedFrom":[subQ2,makeQuery(id+"F14.opExtrude","SWEPT_FACE",FACE,{"disambiguationData":[OSD([sQuery(id+"F13.wireOp",EDGE,"E98.1.0.0")])]})]}),makeQuery(id+"F14.boolean.opBoolean","INTERSECT",EDGE,{"derivedFrom":[subQ2,makeQuery(id+"F14.opExtrude","SWEPT_FACE",FACE,{"disambiguationData":[OSD([sQuery(id+"F13.wireOp",EDGE,"E98.1.0.1")])]})]}),makeQuery(id+"F14.boolean.opBoolean","INTERSECT",EDGE,{"derivedFrom":[subQ2,makeQuery(id+"F14.opExtrude","SWEPT_FACE",FACE,{"disambiguationData":[OSD([sQuery(id+"F13.wireOp",EDGE,"E98.1.0.3")])]})]}),makeQuery(id+"F14.boolean.opBoolean","INTERSECT",EDGE,{"derivedFrom":[subQ2,makeQuery(id+"F14.opExtrude","SWEPT_FACE",FACE,{"disambiguationData":[OSD([sQuery(id+"F13.wireOp",EDGE,"E98.1.0.4")])]})]}),makeQuery(id+"F14.boolean.opBoolean","INTERSECT",EDGE,{"derivedFrom":[subQ2,makeQuery(id+"F14.opExtrude","SWEPT_FACE",FACE,{"disambiguationData":[OSD([sQuery(id+"F13.wireOp",EDGE,"E98.1.0.5")])]})]}),makeQuery(id+"F14.boolean.opBoolean","INTERSECT",EDGE,{"derivedFrom":[subQ2,makeQuery(id+"F14.opExtrude","SWEPT_FACE",FACE,{"disambiguationData":[OSD([sQuery(id+"F13.wireOp",EDGE,"E98.1.0.6")])]})]}),makeQuery(id+"F14.boolean.opBoolean","INTERSECT",EDGE,{"derivedFrom":[subQ2,makeQuery(id+"F14.opExtrude","SWEPT_FACE",FACE,{"disambiguationData":[OSD([sQuery(id+"F13.wireOp",EDGE,"E98.2.0.0")])]})]}),makeQuery(id+"F14.boolean.opBoolean","INTERSECT",EDGE,{"derivedFrom":[subQ2,makeQuery(id+"F14.opExtrude","SWEPT_FACE",FACE,{"disambiguationData":[OSD([sQuery(id+"F13.wireOp",EDGE,"E98.2.0.1")])]})]}),makeQuery(id+"F14.boolean.opBoolean","INTERSECT",EDGE,{"derivedFrom":[subQ2,makeQuery(id+"F14.opExtrude","SWEPT_FACE",FACE,{"disambiguationData":[OSD([sQuery(id+"F13.wireOp",EDGE,"E98.2.0.3")])]})]}),makeQuery(id+"F14.boolean.opBoolean","INTERSECT",EDGE,{"derivedFrom":[subQ2,makeQuery(id+"F14.opExtrude","SWEPT_FACE",FACE,{"disambiguationData":[OSD([sQuery(id+"F13.wireOp",EDGE,"E98.2.0.4")])]})]}),makeQuery(id+"F14.boolean.opBoolean","INTERSECT",EDGE,{"derivedFrom":[subQ2,makeQuery(id+"F14.opExtrude","SWEPT_FACE",FACE,{"disambiguationData":[OSD([sQuery(id+"F13.wireOp",EDGE,"E98.2.0.5")])]})]}),makeQuery(id+"F14.boolean.opBoolean","INTERSECT",EDGE,{"derivedFrom":[subQ2,makeQuery(id+"F14.opExtrude","SWEPT_FACE",FACE,{"disambiguationData":[OSD([sQuery(id+"F13.wireOp",EDGE,"E98.2.0.6")])]})]}),makeQuery(id+"F14.boolean.opBoolean","INTERSECT",EDGE,{"derivedFrom":[subQ2,makeQuery(id+"F14.opExtrude","SWEPT_FACE",FACE,{"disambiguationData":[OSD([sQuery(id+"F13.wireOp",EDGE,"E98.3.0.0")])]})]}),makeQuery(id+"F14.boolean.opBoolean","INTERSECT",EDGE,{"derivedFrom":[subQ2,makeQuery(id+"F14.opExtrude","SWEPT_FACE",FACE,{"disambiguationData":[OSD([sQuery(id+"F13.wireOp",EDGE,"E98.3.0.1")])]})]}),makeQuery(id+"F14.boolean.opBoolean","INTERSECT",EDGE,{"derivedFrom":[subQ2,makeQuery(id+"F14.opExtrude","SWEPT_FACE",FACE,{"disambiguationData":[OSD([sQuery(id+"F13.wireOp",EDGE,"E98.3.0.3")])]})]}),makeQuery(id+"F14.boolean.opBoolean","INTERSECT",EDGE,{"derivedFrom":[subQ2,makeQuery(id+"F14.opExtrude","SWEPT_FACE",FACE,{"disambiguationData":[OSD([sQuery(id+"F13.wireOp",EDGE,"E98.3.0.4")])]})]}),makeQuery(id+"F14.boolean.opBoolean","INTERSECT",EDGE,{"derivedFrom":[subQ2,makeQuery(id+"F14.opExtrude","SWEPT_FACE",FACE,{"disambiguationData":[OSD([sQuery(id+"F13.wireOp",EDGE,"E98.3.0.5")])]})]}),makeQuery(id+"F14.boolean.opBoolean","INTERSECT",EDGE,{"derivedFrom":[subQ2,makeQuery(id+"F14.opExtrude","SWEPT_FACE",FACE,{"disambiguationData":[OSD([sQuery(id+"F13.wireOp",EDGE,"E98.3.0.6")])]})]})]);}
            var Q59;
            {var subQ0=sQuery(id+"F0.wireOp",EDGE,"E61.top");var subQ2=makeQuery(id+"F4.boolean.opBoolean","MERGE",FACE,{"derivedFrom":[makeQuery(id+"F3.opExtrude","SWEPT_FACE",FACE,{"disambiguationData":[OSD([subQ0]),TDD([makeQuery(id+"F0.imprint","IMPRINT",EDGE,{"disambiguationData":[TD([[makeQuery(id+"F0.imprint","INTERSECT",VERTEX,{"derivedFrom":[subQ0,sQuery(id+"F0.wireOp",EDGE,"E77")]}),-1.0]])],"derivedFrom":subQ0}),makeQuery(id+"F0.imprint","IMPRINT",EDGE,{"disambiguationData":[TD([[makeQuery(id+"F0.imprint","INTERSECT",VERTEX,{"derivedFrom":[subQ0,sQuery(id+"F0.wireOp",EDGE,"E78")]}),1.0]])],"derivedFrom":subQ0})])]}),makeQuery(id+"F3.opExtrude","SWEPT_FACE",FACE,{"disambiguationData":[OSD([subQ0]),TDD([makeQuery(id+"F0.imprint","IMPRINT",EDGE,{"disambiguationData":[TD([[makeQuery(id+"F0.imprint","INTERSECT",VERTEX,{"derivedFrom":[subQ0,sQuery(id+"F0.wireOp",EDGE,"E62")]}),-1.0]])],"derivedFrom":subQ0})])]}),makeQuery(id+"F4.opExtrude","SWEPT_FACE",FACE,{"disambiguationData":[OSD([subQ0])]})]});Q59=qUnion([makeQuery(id+"F14.boolean.opBoolean","INTERSECT",EDGE,{"derivedFrom":[subQ2,makeQuery(id+"F14.opExtrude","SWEPT_FACE",FACE,{"disambiguationData":[OSD([sQuery(id+"F13.wireOp",EDGE,"E89")])]})]}),makeQuery(id+"F14.boolean.opBoolean","INTERSECT",EDGE,{"derivedFrom":[subQ2,makeQuery(id+"F14.opExtrude","SWEPT_FACE",FACE,{"disambiguationData":[OSD([sQuery(id+"F13.wireOp",EDGE,"E90")])]})]}),makeQuery(id+"F14.boolean.opBoolean","INTERSECT",EDGE,{"derivedFrom":[subQ2,makeQuery(id+"F14.opExtrude","SWEPT_FACE",FACE,{"disambiguationData":[OSD([sQuery(id+"F13.wireOp",EDGE,"E92")])]})]}),makeQuery(id+"F14.boolean.opBoolean","INTERSECT",EDGE,{"derivedFrom":[subQ2,makeQuery(id+"F14.opExtrude","SWEPT_FACE",FACE,{"disambiguationData":[OSD([sQuery(id+"F13.wireOp",EDGE,"E93")])]})]}),makeQuery(id+"F14.boolean.opBoolean","INTERSECT",EDGE,{"derivedFrom":[subQ2,makeQuery(id+"F14.opExtrude","SWEPT_FACE",FACE,{"disambiguationData":[OSD([sQuery(id+"F13.wireOp",EDGE,"E96")])]})]}),makeQuery(id+"F14.boolean.opBoolean","INTERSECT",EDGE,{"derivedFrom":[subQ2,makeQuery(id+"F14.opExtrude","SWEPT_FACE",FACE,{"disambiguationData":[OSD([sQuery(id+"F13.wireOp",EDGE,"E97")])]})]}),makeQuery(id+"F14.boolean.opBoolean","INTERSECT",EDGE,{"derivedFrom":[subQ2,makeQuery(id+"F14.opExtrude","SWEPT_FACE",FACE,{"disambiguationData":[OSD([sQuery(id+"F13.wireOp",EDGE,"E98.1.0.0")])]})]}),makeQuery(id+"F14.boolean.opBoolean","INTERSECT",EDGE,{"derivedFrom":[subQ2,makeQuery(id+"F14.opExtrude","SWEPT_FACE",FACE,{"disambiguationData":[OSD([sQuery(id+"F13.wireOp",EDGE,"E98.1.0.1")])]})]}),makeQuery(id+"F14.boolean.opBoolean","INTERSECT",EDGE,{"derivedFrom":[subQ2,makeQuery(id+"F14.opExtrude","SWEPT_FACE",FACE,{"disambiguationData":[OSD([sQuery(id+"F13.wireOp",EDGE,"E98.1.0.3")])]})]}),makeQuery(id+"F14.boolean.opBoolean","INTERSECT",EDGE,{"derivedFrom":[subQ2,makeQuery(id+"F14.opExtrude","SWEPT_FACE",FACE,{"disambiguationData":[OSD([sQuery(id+"F13.wireOp",EDGE,"E98.1.0.4")])]})]}),makeQuery(id+"F14.boolean.opBoolean","INTERSECT",EDGE,{"derivedFrom":[subQ2,makeQuery(id+"F14.opExtrude","SWEPT_FACE",FACE,{"disambiguationData":[OSD([sQuery(id+"F13.wireOp",EDGE,"E98.1.0.5")])]})]}),makeQuery(id+"F14.boolean.opBoolean","INTERSECT",EDGE,{"derivedFrom":[subQ2,makeQuery(id+"F14.opExtrude","SWEPT_FACE",FACE,{"disambiguationData":[OSD([sQuery(id+"F13.wireOp",EDGE,"E98.1.0.6")])]})]}),makeQuery(id+"F14.boolean.opBoolean","INTERSECT",EDGE,{"derivedFrom":[subQ2,makeQuery(id+"F14.opExtrude","SWEPT_FACE",FACE,{"disambiguationData":[OSD([sQuery(id+"F13.wireOp",EDGE,"E98.2.0.0")])]})]}),makeQuery(id+"F14.boolean.opBoolean","INTERSECT",EDGE,{"derivedFrom":[subQ2,makeQuery(id+"F14.opExtrude","SWEPT_FACE",FACE,{"disambiguationData":[OSD([sQuery(id+"F13.wireOp",EDGE,"E98.2.0.1")])]})]}),makeQuery(id+"F14.boolean.opBoolean","INTERSECT",EDGE,{"derivedFrom":[subQ2,makeQuery(id+"F14.opExtrude","SWEPT_FACE",FACE,{"disambiguationData":[OSD([sQuery(id+"F13.wireOp",EDGE,"E98.2.0.3")])]})]}),makeQuery(id+"F14.boolean.opBoolean","INTERSECT",EDGE,{"derivedFrom":[subQ2,makeQuery(id+"F14.opExtrude","SWEPT_FACE",FACE,{"disambiguationData":[OSD([sQuery(id+"F13.wireOp",EDGE,"E98.2.0.4")])]})]}),makeQuery(id+"F14.boolean.opBoolean","INTERSECT",EDGE,{"derivedFrom":[subQ2,makeQuery(id+"F14.opExtrude","SWEPT_FACE",FACE,{"disambiguationData":[OSD([sQuery(id+"F13.wireOp",EDGE,"E98.2.0.5")])]})]}),makeQuery(id+"F14.boolean.opBoolean","INTERSECT",EDGE,{"derivedFrom":[subQ2,makeQuery(id+"F14.opExtrude","SWEPT_FACE",FACE,{"disambiguationData":[OSD([sQuery(id+"F13.wireOp",EDGE,"E98.2.0.6")])]})]}),makeQuery(id+"F14.boolean.opBoolean","INTERSECT",EDGE,{"derivedFrom":[subQ2,makeQuery(id+"F14.opExtrude","SWEPT_FACE",FACE,{"disambiguationData":[OSD([sQuery(id+"F13.wireOp",EDGE,"E98.3.0.0")])]})]}),makeQuery(id+"F14.boolean.opBoolean","INTERSECT",EDGE,{"derivedFrom":[subQ2,makeQuery(id+"F14.opExtrude","SWEPT_FACE",FACE,{"disambiguationData":[OSD([sQuery(id+"F13.wireOp",EDGE,"E98.3.0.1")])]})]}),makeQuery(id+"F14.boolean.opBoolean","INTERSECT",EDGE,{"derivedFrom":[subQ2,makeQuery(id+"F14.opExtrude","SWEPT_FACE",FACE,{"disambiguationData":[OSD([sQuery(id+"F13.wireOp",EDGE,"E98.3.0.3")])]})]}),makeQuery(id+"F14.boolean.opBoolean","INTERSECT",EDGE,{"derivedFrom":[subQ2,makeQuery(id+"F14.opExtrude","SWEPT_FACE",FACE,{"disambiguationData":[OSD([sQuery(id+"F13.wireOp",EDGE,"E98.3.0.4")])]})]}),makeQuery(id+"F14.boolean.opBoolean","INTERSECT",EDGE,{"derivedFrom":[subQ2,makeQuery(id+"F14.opExtrude","SWEPT_FACE",FACE,{"disambiguationData":[OSD([sQuery(id+"F13.wireOp",EDGE,"E98.3.0.5")])]})]}),makeQuery(id+"F14.boolean.opBoolean","INTERSECT",EDGE,{"derivedFrom":[subQ2,makeQuery(id+"F14.opExtrude","SWEPT_FACE",FACE,{"disambiguationData":[OSD([sQuery(id+"F13.wireOp",EDGE,"E98.3.0.6")])]})]})]);}
            var Q60;
            Q60=makeQuery(id+"F14.boolean.opBoolean","COPY",EDGE,{"derivedFrom":makeQuery(id+"F14.opExtrude","CAP_EDGE",EDGE,{"disambiguationData":[OSD([sQuery(id+"F13.wireOp",EDGE,"E98.1.0.0")])],"isStart":true})});
            var Q61;
            Q61=makeQuery(id+"F14.boolean.opBoolean","COPY",EDGE,{"derivedFrom":makeQuery(id+"F14.opExtrude","CAP_EDGE",EDGE,{"disambiguationData":[OSD([sQuery(id+"F13.wireOp",EDGE,"E98.1.0.4")])],"isStart":true})});
            var Q62;
            Q62=makeQuery(id+"F14.boolean.opBoolean","COPY",EDGE,{"derivedFrom":makeQuery(id+"F14.opExtrude","CAP_EDGE",EDGE,{"disambiguationData":[OSD([sQuery(id+"F13.wireOp",EDGE,"E98.1.0.3")])],"isStart":true})});
            var Q63;
            Q63=makeQuery(id+"F14.boolean.opBoolean","COPY",EDGE,{"derivedFrom":makeQuery(id+"F14.opExtrude","CAP_EDGE",EDGE,{"disambiguationData":[OSD([sQuery(id+"F13.wireOp",EDGE,"E98.1.0.5")])],"isStart":true})});
            var Q64;
            Q64=makeQuery(id+"F14.boolean.opBoolean","COPY",EDGE,{"derivedFrom":makeQuery(id+"F14.opExtrude","CAP_EDGE",EDGE,{"disambiguationData":[OSD([sQuery(id+"F13.wireOp",EDGE,"E98.1.0.1")])],"isStart":true})});
            var Q65;
            Q65=makeQuery(id+"F14.boolean.opBoolean","COPY",EDGE,{"derivedFrom":makeQuery(id+"F14.opExtrude","CAP_EDGE",EDGE,{"disambiguationData":[OSD([sQuery(id+"F13.wireOp",EDGE,"E98.1.0.6")])],"isStart":true})});
            var Q66;
            Q66=makeQuery(id+"F14.boolean.opBoolean","COPY",EDGE,{"derivedFrom":makeQuery(id+"F14.opExtrude","CAP_EDGE",EDGE,{"disambiguationData":[OSD([sQuery(id+"F13.wireOp",EDGE,"E98.2.0.4")])],"isStart":true})});
            var Q67;
            Q67=makeQuery(id+"F14.boolean.opBoolean","COPY",EDGE,{"derivedFrom":makeQuery(id+"F14.opExtrude","CAP_EDGE",EDGE,{"disambiguationData":[OSD([sQuery(id+"F13.wireOp",EDGE,"E98.2.0.0")])],"isStart":true})});
            var Q68;
            Q68=makeQuery(id+"F14.boolean.opBoolean","COPY",EDGE,{"derivedFrom":makeQuery(id+"F14.opExtrude","CAP_EDGE",EDGE,{"disambiguationData":[OSD([sQuery(id+"F13.wireOp",EDGE,"E98.2.0.1")])],"isStart":true})});
            var Q69;
            Q69=makeQuery(id+"F14.boolean.opBoolean","COPY",EDGE,{"derivedFrom":makeQuery(id+"F14.opExtrude","CAP_EDGE",EDGE,{"disambiguationData":[OSD([sQuery(id+"F13.wireOp",EDGE,"E98.3.0.0")])],"isStart":true})});
            var Q70;
            Q70=makeQuery(id+"F14.boolean.opBoolean","COPY",EDGE,{"derivedFrom":makeQuery(id+"F14.opExtrude","CAP_EDGE",EDGE,{"disambiguationData":[OSD([sQuery(id+"F13.wireOp",EDGE,"E98.3.0.1")])],"isStart":true})});
            var Q71;
            Q71=makeQuery(id+"F14.boolean.opBoolean","COPY",EDGE,{"derivedFrom":makeQuery(id+"F14.opExtrude","CAP_EDGE",EDGE,{"disambiguationData":[OSD([sQuery(id+"F13.wireOp",EDGE,"E98.4.0.0")])],"isStart":true})});
            var Q72;
            Q72=makeQuery(id+"F14.boolean.opBoolean","COPY",EDGE,{"derivedFrom":makeQuery(id+"F14.opExtrude","CAP_EDGE",EDGE,{"disambiguationData":[OSD([sQuery(id+"F13.wireOp",EDGE,"E98.4.0.1")])],"isStart":true})});
            var Q73;
            Q73=makeQuery(id+"F14.boolean.opBoolean","COPY",EDGE,{"derivedFrom":makeQuery(id+"F14.opExtrude","CAP_EDGE",EDGE,{"disambiguationData":[OSD([sQuery(id+"F13.wireOp",EDGE,"E98.4.0.4")])],"isStart":true})});
            var Q74;
            Q74=makeQuery(id+"F14.boolean.opBoolean","COPY",EDGE,{"derivedFrom":makeQuery(id+"F14.opExtrude","CAP_EDGE",EDGE,{"disambiguationData":[OSD([sQuery(id+"F13.wireOp",EDGE,"E98.3.0.4")])],"isStart":true})});
            var Q75;
            Q75=makeQuery(id+"F14.boolean.opBoolean","COPY",EDGE,{"derivedFrom":makeQuery(id+"F14.opExtrude","CAP_EDGE",EDGE,{"disambiguationData":[OSD([sQuery(id+"F13.wireOp",EDGE,"E98.2.0.3")])],"isStart":true})});
            var Q76;
            Q76=makeQuery(id+"F14.boolean.opBoolean","COPY",EDGE,{"derivedFrom":makeQuery(id+"F14.opExtrude","CAP_EDGE",EDGE,{"disambiguationData":[OSD([sQuery(id+"F13.wireOp",EDGE,"E98.3.0.3")])],"isStart":true})});
            var Q77;
            Q77=makeQuery(id+"F14.boolean.opBoolean","COPY",EDGE,{"derivedFrom":makeQuery(id+"F14.opExtrude","CAP_EDGE",EDGE,{"disambiguationData":[OSD([sQuery(id+"F13.wireOp",EDGE,"E98.4.0.3")])],"isStart":true})});
            var Q78;
            Q78=makeQuery(id+"F14.boolean.opBoolean","COPY",EDGE,{"derivedFrom":makeQuery(id+"F14.opExtrude","CAP_EDGE",EDGE,{"disambiguationData":[OSD([sQuery(id+"F13.wireOp",EDGE,"E98.3.0.5")])],"isStart":true})});
            var Q79;
            Q79=makeQuery(id+"F14.boolean.opBoolean","COPY",EDGE,{"derivedFrom":makeQuery(id+"F14.opExtrude","CAP_EDGE",EDGE,{"disambiguationData":[OSD([sQuery(id+"F13.wireOp",EDGE,"E98.4.0.5")])],"isStart":true})});
            var Q80;
            Q80=makeQuery(id+"F14.boolean.opBoolean","COPY",EDGE,{"derivedFrom":makeQuery(id+"F14.opExtrude","CAP_EDGE",EDGE,{"disambiguationData":[OSD([sQuery(id+"F13.wireOp",EDGE,"E98.4.0.6")])],"isStart":true})});
            var Q81;
            Q81=makeQuery(id+"F14.boolean.opBoolean","COPY",EDGE,{"derivedFrom":makeQuery(id+"F14.opExtrude","CAP_EDGE",EDGE,{"disambiguationData":[OSD([sQuery(id+"F13.wireOp",EDGE,"E98.3.0.6")])],"isStart":true})});
            var Q82;
            Q82=makeQuery(id+"F14.boolean.opBoolean","COPY",EDGE,{"derivedFrom":makeQuery(id+"F14.opExtrude","CAP_EDGE",EDGE,{"disambiguationData":[OSD([sQuery(id+"F13.wireOp",EDGE,"E98.2.0.6")])],"isStart":true})});
            var Q83;
            Q83=makeQuery(id+"F14.boolean.opBoolean","COPY",EDGE,{"derivedFrom":makeQuery(id+"F14.opExtrude","CAP_EDGE",EDGE,{"disambiguationData":[OSD([sQuery(id+"F13.wireOp",EDGE,"E98.2.0.5")])],"isStart":true})});
            fillet(context, id + "F15", {"entities" : qUnion([Q0, Q1, Q2, Q3, Q4, Q5, Q6, Q7, Q8, Q9, Q10, Q11, Q12, Q13, Q14, Q15, Q16, Q17, Q18, Q19, Q20, Q21, Q22, Q23, Q24, Q25, Q26, Q27, Q28, Q29, Q30, Q31, Q32, Q33, Q34, Q35, Q36, Q37, Q38, Q39, Q40, Q41, Q42, Q43, Q44, Q45, Q46, Q47, Q48, Q49, Q50, Q51, Q52, Q53, Q54, Q55, Q56, Q57, Q58, Q59, Q60, Q61, Q62, Q63, Q64, Q65, Q66, Q67, Q68, Q69, Q70, Q71, Q72, Q73, Q74, Q75, Q76, Q77, Q78, Q79, Q80, Q81, Q82, Q83]), "radius" : .4 * mm, "tangentPropagation" : true, "allowEdgeOverflow" : false});
        }
        {
            var Q0;
            {var subQ1=sQuery(id+"F0.wireOp",EDGE,"E64");var subQ2=sQuery(id+"F0.wireOp",EDGE,"E3.filletArc");Q0=makeQuery(id+"F12.boolean.opBoolean","INTERSECT",EDGE,{"derivedFrom":[makeQuery(id+"F6.boolean.opBoolean","SPLIT",FACE,{"disambiguationData":[TD([makeQuery(id+"F2.opExtrude","SWEPT_FACE",FACE,{"disambiguationData":[OSD([subQ2])]})])],"derivedFrom":makeQuery(id+"F3.opExtrude","SWEPT_FACE",FACE,{"disambiguationData":[OSD([subQ1])]})}),makeQuery(id+"F12.opExtrude","SWEPT_FACE",FACE,{"disambiguationData":[OSD([sQuery(id+"F11.wireOp",EDGE,"E88")])]})]});}
            var Q1;
            Q1=makeQuery(id+"F12.boolean.opBoolean","COPY",EDGE,{"derivedFrom":makeQuery(id+"F12.opExtrude","CAP_EDGE",EDGE,{"disambiguationData":[OSD([sQuery(id+"F11.wireOp",EDGE,"E88")])],"isStart":true})});
            var Q2;
            Q2=makeQuery(id+"F12.boolean.opBoolean","INTERSECT",EDGE,{"derivedFrom":[makeQuery(id+"F9.opFillet","BLEND_FACE",FACE,{"disambiguationData":[OSD([sQuery(id+"F0.wireOp",EDGE,"E3.filletArc")])]}),makeQuery(id+"F12.opExtrude","SWEPT_FACE",FACE,{"disambiguationData":[OSD([sQuery(id+"F11.wireOp",EDGE,"E88")])]})]});
            var Q3;
            Q3=makeQuery(id+"F12.boolean.opBoolean","INTERSECT",EDGE,{"derivedFrom":[makeQuery(id+"F2.opExtrude","SWEPT_FACE",FACE,{"disambiguationData":[OSD([sQuery(id+"F0.wireOp",EDGE,"E3.filletArc")])]}),makeQuery(id+"F12.opExtrude","SWEPT_FACE",FACE,{"disambiguationData":[OSD([sQuery(id+"F11.wireOp",EDGE,"E88")])]})]});
            var Q4;
            {var subQ0=sQuery(id+"F0.wireOp",EDGE,"E61.top");Q4=makeQuery(id+"F3.opExtrude","CAP_EDGE",EDGE,{"disambiguationData":[OSD([subQ0]),TDD([makeQuery(id+"F0.imprint","IMPRINT",EDGE,{"disambiguationData":[TD([[makeQuery(id+"F0.imprint","INTERSECT",VERTEX,{"derivedFrom":[subQ0,sQuery(id+"F0.wireOp",EDGE,"E77")]}),-1.0]])],"derivedFrom":subQ0}),makeQuery(id+"F0.imprint","IMPRINT",EDGE,{"disambiguationData":[TD([[makeQuery(id+"F0.imprint","INTERSECT",VERTEX,{"derivedFrom":[subQ0,sQuery(id+"F0.wireOp",EDGE,"E78")]}),1.0]])],"derivedFrom":subQ0})])],"isStart":false});}
            fillet(context, id + "F16", {"entities" : qUnion([Q0, Q1, Q2, Q3, Q4]), "radius" : .5 * mm, "tangentPropagation" : true, "allowEdgeOverflow" : false});
        }
        {
            var Q0;
            Q0=makeQuery(id+"F2.opExtrude","SWEPT_BODY",BODY,{"disambiguationData":[OSD([sQuery(id+"F0.wireOp",EDGE,"E0.5"),sQuery(id+"F0.wireOp",EDGE,"E3.filletArc"),sQuery(id+"F0.wireOp",EDGE,"E6.filletArc"),sQuery(id+"F0.wireOp",EDGE,"E62"),sQuery(id+"F0.wireOp",EDGE,"E64"),sQuery(id+"F0.wireOp",EDGE,"E73"),sQuery(id+"F0.wireOp",EDGE,"E74")])]});
            var Q1;
            Q1=qCreatedBy(makeId("Front.planeOp"),FACE);
            mirror(context, id + "F17", {"entities" : qUnion([Q0]), "mirrorPlane" : qUnion([Q1])});
        }
        {
            var Q0;
            Q0=makeQuery(id+"F2.opExtrude","SWEPT_BODY",BODY,{"disambiguationData":[OSD([sQuery(id+"F0.wireOp",EDGE,"E0.5"),sQuery(id+"F0.wireOp",EDGE,"E3.filletArc"),sQuery(id+"F0.wireOp",EDGE,"E6.filletArc"),sQuery(id+"F0.wireOp",EDGE,"E62"),sQuery(id+"F0.wireOp",EDGE,"E64"),sQuery(id+"F0.wireOp",EDGE,"E73"),sQuery(id+"F0.wireOp",EDGE,"E74")])]});
            var Q1;
            Q1=makeQuery(id+"F17.opPattern","COPY",BODY,{"derivedFrom":makeQuery(id+"F2.opExtrude","SWEPT_BODY",BODY,{"disambiguationData":[OSD([sQuery(id+"F0.wireOp",EDGE,"E0.5"),sQuery(id+"F0.wireOp",EDGE,"E3.filletArc"),sQuery(id+"F0.wireOp",EDGE,"E6.filletArc"),sQuery(id+"F0.wireOp",EDGE,"E62"),sQuery(id+"F0.wireOp",EDGE,"E64"),sQuery(id+"F0.wireOp",EDGE,"E73"),sQuery(id+"F0.wireOp",EDGE,"E74")])]}),"instanceName":"1"});
            var Q2;
            Q2=qCreatedBy(makeId("Right.planeOp"),FACE);
            mirror(context, id + "F18", {"entities" : qUnion([Q0, Q1]), "mirrorPlane" : qUnion([Q2])});
        }
    });
